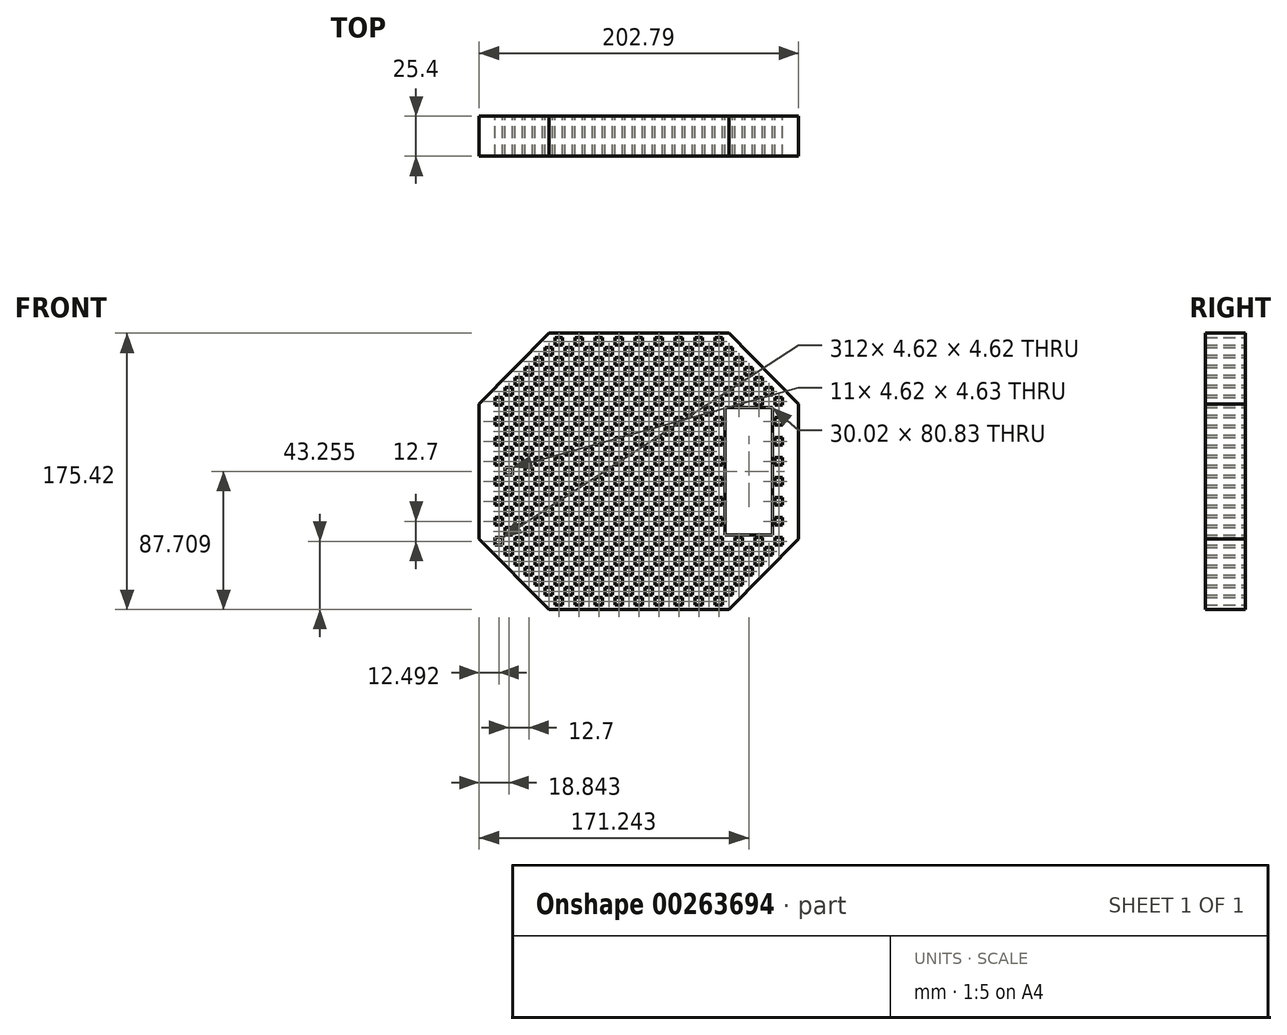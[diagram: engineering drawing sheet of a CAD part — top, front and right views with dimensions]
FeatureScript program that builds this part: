
annotation { "Feature Type Name" : "Feature", "Feature Type Description" : "" }
export const myFeature = defineFeature(function(context is Context, id is Id, definition is map)
    precondition{}
    {
        {
            var Q0;
            Q0=qCreatedBy(makeId("Front.planeOp"),FACE);
            var sketch = newSketch(context, id + "F0", { "sketchPlane" : qUnion([Q0])});
            skPoint(sketch, "E0.orphan", {"position": v(23.5, -32.04) * mm});
            skPoint(sketch, "E1.start.orphan", {"position": v(0, -32.04) * mm});
            skLineSegment(sketch, "E2.2.0.0", {"start": v(51.26, 13.82) * mm, "end": v(51.26, 9.2) * mm});
            skPoint(sketch, "E2.2.0.1", {"position": v(40.87, 11.5) * mm});
            skLineSegment(sketch, "E2.2.0.2", {"start": v(49.53, 2.84) * mm, "end": v(44.91, 2.84) * mm});
            skPoint(sketch, "E2.2.0.3", {"position": v(53.57, 11.5) * mm});
            skLineSegment(sketch, "E2.2.0.4", {"start": v(49.53, 7.47) * mm, "end": v(49.53, 2.84) * mm});
            skPoint(sketch, "E2.2.0.6", {"position": v(40.87, 7.47) * mm});
            skLineSegment(sketch, "E2.2.0.7", {"start": v(38.56, 13.82) * mm, "end": v(38.56, 9.2) * mm});
            skLineSegment(sketch, "E2.2.0.8", {"start": v(47.22, 7.47) * mm, "end": v(49.53, 7.47) * mm});
            skLineSegment(sketch, "E2.2.0.9", {"start": v(55.88, 13.82) * mm, "end": v(55.88, 9.2) * mm});
            skLineSegment(sketch, "E2.2.0.11", {"start": v(43.18, 13.82) * mm, "end": v(38.56, 13.82) * mm});
            skLineSegment(sketch, "E2.2.0.13", {"start": v(43.18, 9.2) * mm, "end": v(38.56, 9.2) * mm});
            skLineSegment(sketch, "E2.2.0.14", {"start": v(51.26, 9.2) * mm, "end": v(55.88, 9.2) * mm});
            skLineSegment(sketch, "E2.2.0.15", {"start": v(43.18, 13.82) * mm, "end": v(43.18, 9.2) * mm});
            skLineSegment(sketch, "E2.2.0.17", {"start": v(44.91, 2.84) * mm, "end": v(44.91, 7.47) * mm});
            skPoint(sketch, "E2.2.0.18", {"position": v(40.87, 15.54) * mm});
            skLineSegment(sketch, "E2.2.0.19", {"start": v(44.91, 7.47) * mm, "end": v(47.22, 7.47) * mm});
            skLineSegment(sketch, "E2.2.0.20", {"start": v(51.26, 13.82) * mm, "end": v(55.88, 13.82) * mm});
            skLineSegment(sketch, "E2.3.0.0", {"start": v(76.66, 13.82) * mm, "end": v(76.66, 9.2) * mm});
            skPoint(sketch, "E2.3.0.1", {"position": v(66.27, 11.5) * mm});
            skLineSegment(sketch, "E2.3.0.2", {"start": v(74.93, 2.84) * mm, "end": v(70.31, 2.84) * mm});
            skPoint(sketch, "E2.3.0.3", {"position": v(78.97, 11.5) * mm});
            skLineSegment(sketch, "E2.3.0.4", {"start": v(74.93, 7.47) * mm, "end": v(74.93, 2.84) * mm});
            skLineSegment(sketch, "E2.3.0.5", {"start": v(59.92, 7.47) * mm, "end": v(62.23, 7.47) * mm});
            skPoint(sketch, "E2.3.0.6", {"position": v(66.27, 7.47) * mm});
            skLineSegment(sketch, "E2.3.0.7", {"start": v(63.96, 13.82) * mm, "end": v(63.96, 9.2) * mm});
            skLineSegment(sketch, "E2.3.0.8", {"start": v(72.62, 7.47) * mm, "end": v(74.93, 7.47) * mm});
            skLineSegment(sketch, "E2.3.0.9", {"start": v(81.28, 13.82) * mm, "end": v(81.28, 9.2) * mm});
            skLineSegment(sketch, "E2.3.0.10", {"start": v(62.23, 2.84) * mm, "end": v(62.23, 7.47) * mm});
            skLineSegment(sketch, "E2.3.0.11", {"start": v(68.58, 13.82) * mm, "end": v(63.96, 13.82) * mm});
            skLineSegment(sketch, "E2.3.0.12", {"start": v(57.61, 2.84) * mm, "end": v(57.61, 7.47) * mm});
            skLineSegment(sketch, "E2.3.0.13", {"start": v(68.58, 9.2) * mm, "end": v(63.96, 9.2) * mm});
            skLineSegment(sketch, "E2.3.0.14", {"start": v(76.66, 9.2) * mm, "end": v(81.28, 9.2) * mm});
            skLineSegment(sketch, "E2.3.0.15", {"start": v(68.58, 13.82) * mm, "end": v(68.58, 9.2) * mm});
            skLineSegment(sketch, "E2.3.0.16", {"start": v(57.61, 2.84) * mm, "end": v(62.23, 2.84) * mm});
            skLineSegment(sketch, "E2.3.0.17", {"start": v(70.31, 2.84) * mm, "end": v(70.31, 7.47) * mm});
            skPoint(sketch, "E2.3.0.18", {"position": v(66.27, 15.54) * mm});
            skLineSegment(sketch, "E2.3.0.19", {"start": v(70.31, 7.47) * mm, "end": v(72.62, 7.47) * mm});
            skLineSegment(sketch, "E2.3.0.20", {"start": v(76.66, 13.82) * mm, "end": v(81.28, 13.82) * mm});
            skLineSegment(sketch, "E2.3.0.21", {"start": v(57.61, 7.47) * mm, "end": v(59.92, 7.47) * mm});
            skPoint(sketch, "E2.4.0.1", {"position": v(91.67, 11.5) * mm});
            skLineSegment(sketch, "E2.4.0.2", {"start": v(100.33, 2.84) * mm, "end": v(95.71, 2.84) * mm});
            skLineSegment(sketch, "E2.4.0.4", {"start": v(100.33, 7.47) * mm, "end": v(100.33, 2.84) * mm});
            skLineSegment(sketch, "E2.4.0.5", {"start": v(85.32, 7.47) * mm, "end": v(87.63, 7.47) * mm});
            skPoint(sketch, "E2.4.0.6", {"position": v(91.67, 7.47) * mm});
            skLineSegment(sketch, "E2.4.0.7", {"start": v(89.36, 13.82) * mm, "end": v(89.36, 9.2) * mm});
            skLineSegment(sketch, "E2.4.0.8", {"start": v(98.02, 7.47) * mm, "end": v(100.33, 7.47) * mm});
            skLineSegment(sketch, "E2.4.0.10", {"start": v(87.63, 2.84) * mm, "end": v(87.63, 7.47) * mm});
            skLineSegment(sketch, "E2.4.0.11", {"start": v(93.98, 13.82) * mm, "end": v(89.36, 13.82) * mm});
            skLineSegment(sketch, "E2.4.0.12", {"start": v(83.01, 2.84) * mm, "end": v(83.01, 7.47) * mm});
            skLineSegment(sketch, "E2.4.0.13", {"start": v(93.98, 9.2) * mm, "end": v(89.36, 9.2) * mm});
            skLineSegment(sketch, "E2.4.0.15", {"start": v(93.98, 13.82) * mm, "end": v(93.98, 9.2) * mm});
            skLineSegment(sketch, "E2.4.0.16", {"start": v(83.01, 2.84) * mm, "end": v(87.63, 2.84) * mm});
            skLineSegment(sketch, "E2.4.0.17", {"start": v(95.71, 2.84) * mm, "end": v(95.71, 7.47) * mm});
            skPoint(sketch, "E2.4.0.18", {"position": v(91.67, 15.54) * mm});
            skLineSegment(sketch, "E2.4.0.19", {"start": v(95.71, 7.47) * mm, "end": v(98.02, 7.47) * mm});
            skLineSegment(sketch, "E2.4.0.21", {"start": v(83.01, 7.47) * mm, "end": v(85.32, 7.47) * mm});
            skPoint(sketch, "E2.9.0.3", {"position": v(231.37, 11.5) * mm});
            skLineSegment(sketch, "E2.direction1", {"start": v(-18.59, 2.84) * mm, "end": v(6.81, 2.84) * mm, "construction": true});
            skPoint(sketch, "E3.0.1.0", {"position": v(40.87, 24.2) * mm});
            skPoint(sketch, "E3.0.1.12", {"position": v(40.87, 20.17) * mm});
            skLineSegment(sketch, "E3.0.1.14", {"start": v(-18.59, 15.54) * mm, "end": v(6.81, 15.54) * mm, "construction": true});
            skLineSegment(sketch, "E3.0.1.15", {"start": v(83.01, 15.54) * mm, "end": v(87.63, 15.54) * mm});
            skLineSegment(sketch, "E3.0.1.17", {"start": v(70.31, 15.54) * mm, "end": v(70.31, 20.17) * mm});
            skLineSegment(sketch, "E3.0.1.18", {"start": v(95.71, 15.54) * mm, "end": v(95.71, 20.17) * mm});
            skLineSegment(sketch, "E3.0.1.19", {"start": v(49.53, 15.54) * mm, "end": v(44.91, 15.54) * mm});
            skLineSegment(sketch, "E3.0.1.21", {"start": v(49.53, 20.17) * mm, "end": v(49.53, 15.54) * mm});
            skPoint(sketch, "E3.0.1.29", {"position": v(40.87, 28.24) * mm});
            skLineSegment(sketch, "E3.0.1.30", {"start": v(74.93, 20.17) * mm, "end": v(74.93, 15.54) * mm});
            skPoint(sketch, "E3.0.1.34", {"position": v(66.27, 24.2) * mm});
            skLineSegment(sketch, "E3.0.1.37", {"start": v(100.33, 15.54) * mm, "end": v(95.71, 15.54) * mm});
            skPoint(sketch, "E3.0.1.41", {"position": v(78.97, 24.2) * mm});
            skLineSegment(sketch, "E3.0.1.43", {"start": v(100.33, 20.17) * mm, "end": v(100.33, 15.54) * mm});
            skPoint(sketch, "E3.0.1.45", {"position": v(66.27, 20.17) * mm});
            skLineSegment(sketch, "E3.0.1.46", {"start": v(36.83, 15.54) * mm, "end": v(36.83, 20.17) * mm});
            skPoint(sketch, "E3.0.1.49", {"position": v(91.67, 24.2) * mm});
            skLineSegment(sketch, "E3.0.1.51", {"start": v(62.23, 15.54) * mm, "end": v(62.23, 20.17) * mm});
            skLineSegment(sketch, "E3.0.1.52", {"start": v(32.21, 15.54) * mm, "end": v(32.21, 20.17) * mm});
            skLineSegment(sketch, "E3.0.1.58", {"start": v(89.36, 26.52) * mm, "end": v(89.36, 21.9) * mm});
            skPoint(sketch, "E3.0.1.65", {"position": v(66.27, 28.24) * mm});
            skPoint(sketch, "E3.0.1.66", {"position": v(91.67, 20.17) * mm});
            skLineSegment(sketch, "E3.0.1.68", {"start": v(87.63, 15.54) * mm, "end": v(87.63, 20.17) * mm});
            skLineSegment(sketch, "E3.0.1.69", {"start": v(57.61, 15.54) * mm, "end": v(57.61, 20.17) * mm});
            skPoint(sketch, "E3.0.1.79", {"position": v(91.67, 28.24) * mm});
            skLineSegment(sketch, "E3.0.1.82", {"start": v(43.18, 26.52) * mm, "end": v(43.18, 21.9) * mm});
            skLineSegment(sketch, "E3.0.1.87", {"start": v(83.01, 15.54) * mm, "end": v(83.01, 20.17) * mm});
            skLineSegment(sketch, "E3.0.1.88", {"start": v(32.21, 15.54) * mm, "end": v(36.83, 15.54) * mm});
            skPoint(sketch, "E3.0.1.92", {"position": v(231.37, 24.2) * mm});
            skLineSegment(sketch, "E3.0.1.93", {"start": v(25.86, 26.52) * mm, "end": v(25.86, 21.9) * mm});
            skLineSegment(sketch, "E3.0.1.94", {"start": v(44.91, 15.54) * mm, "end": v(44.91, 20.17) * mm});
            skLineSegment(sketch, "E3.0.1.95", {"start": v(25.86, 26.52) * mm, "end": v(30.48, 26.52) * mm});
            skLineSegment(sketch, "E3.0.1.99", {"start": v(93.98, 26.52) * mm, "end": v(93.98, 21.9) * mm});
            skLineSegment(sketch, "E3.0.1.105", {"start": v(51.26, 26.52) * mm, "end": v(51.26, 21.9) * mm});
            skLineSegment(sketch, "E3.0.1.106", {"start": v(76.66, 26.52) * mm, "end": v(76.66, 21.9) * mm});
            skLineSegment(sketch, "E3.0.1.109", {"start": v(38.56, 26.52) * mm, "end": v(38.56, 21.9) * mm});
            skLineSegment(sketch, "E3.0.1.110", {"start": v(30.48, 26.52) * mm, "end": v(30.48, 21.9) * mm});
            skLineSegment(sketch, "E3.0.1.115", {"start": v(63.96, 26.52) * mm, "end": v(63.96, 21.9) * mm});
            skLineSegment(sketch, "E3.0.1.116", {"start": v(55.88, 26.52) * mm, "end": v(55.88, 21.9) * mm});
            skLineSegment(sketch, "E3.0.1.122", {"start": v(25.86, 21.9) * mm, "end": v(30.48, 21.9) * mm});
            skLineSegment(sketch, "E3.0.1.123", {"start": v(81.28, 26.52) * mm, "end": v(81.28, 21.9) * mm});
            skLineSegment(sketch, "E3.0.1.124", {"start": v(43.18, 26.52) * mm, "end": v(38.56, 26.52) * mm});
            skLineSegment(sketch, "E3.0.1.127", {"start": v(43.18, 21.9) * mm, "end": v(38.56, 21.9) * mm});
            skLineSegment(sketch, "E3.0.1.139", {"start": v(93.98, 26.52) * mm, "end": v(89.36, 26.52) * mm});
            skLineSegment(sketch, "E3.0.1.141", {"start": v(93.98, 21.9) * mm, "end": v(89.36, 21.9) * mm});
            skLineSegment(sketch, "E3.0.1.142", {"start": v(68.58, 26.52) * mm, "end": v(68.58, 21.9) * mm});
            skLineSegment(sketch, "E3.0.1.146", {"start": v(57.61, 15.54) * mm, "end": v(62.23, 15.54) * mm});
            skLineSegment(sketch, "E3.0.1.151", {"start": v(51.26, 26.52) * mm, "end": v(55.88, 26.52) * mm});
            skLineSegment(sketch, "E3.0.1.152", {"start": v(76.66, 26.52) * mm, "end": v(81.28, 26.52) * mm});
            skLineSegment(sketch, "E3.0.1.153", {"start": v(32.21, 20.17) * mm, "end": v(34.52, 20.17) * mm});
            skLineSegment(sketch, "E3.0.1.154", {"start": v(70.31, 20.17) * mm, "end": v(72.62, 20.17) * mm});
            skLineSegment(sketch, "E3.0.1.156", {"start": v(44.91, 20.17) * mm, "end": v(47.22, 20.17) * mm});
            skLineSegment(sketch, "E3.0.1.162", {"start": v(74.93, 15.54) * mm, "end": v(70.31, 15.54) * mm});
            skLineSegment(sketch, "E3.0.1.163", {"start": v(34.52, 20.17) * mm, "end": v(36.83, 20.17) * mm});
            skLineSegment(sketch, "E3.0.1.166", {"start": v(95.71, 20.17) * mm, "end": v(98.02, 20.17) * mm});
            skLineSegment(sketch, "E3.0.1.167", {"start": v(57.61, 20.17) * mm, "end": v(59.92, 20.17) * mm});
            skLineSegment(sketch, "E3.0.1.170", {"start": v(59.92, 20.17) * mm, "end": v(62.23, 20.17) * mm});
            skLineSegment(sketch, "E3.0.1.171", {"start": v(47.22, 20.17) * mm, "end": v(49.53, 20.17) * mm});
            skLineSegment(sketch, "E3.0.1.173", {"start": v(83.01, 20.17) * mm, "end": v(85.32, 20.17) * mm});
            skLineSegment(sketch, "E3.0.1.178", {"start": v(72.62, 20.17) * mm, "end": v(74.93, 20.17) * mm});
            skLineSegment(sketch, "E3.0.1.182", {"start": v(85.32, 20.17) * mm, "end": v(87.63, 20.17) * mm});
            skLineSegment(sketch, "E3.0.1.184", {"start": v(98.02, 20.17) * mm, "end": v(100.33, 20.17) * mm});
            skLineSegment(sketch, "E3.0.1.192", {"start": v(68.58, 26.52) * mm, "end": v(63.96, 26.52) * mm});
            skLineSegment(sketch, "E3.0.1.194", {"start": v(51.26, 21.9) * mm, "end": v(55.88, 21.9) * mm});
            skLineSegment(sketch, "E3.0.1.208", {"start": v(68.58, 21.9) * mm, "end": v(63.96, 21.9) * mm});
            skLineSegment(sketch, "E3.0.1.211", {"start": v(76.66, 21.9) * mm, "end": v(81.28, 21.9) * mm});
            skPoint(sketch, "E3.0.2.0", {"position": v(40.87, 36.9) * mm});
            skPoint(sketch, "E3.0.2.7", {"position": v(53.57, 36.9) * mm});
            skLineSegment(sketch, "E3.0.2.8", {"start": v(24.13, 32.87) * mm, "end": v(24.13, 28.24) * mm});
            skPoint(sketch, "E3.0.2.11", {"position": v(15.47, 40.94) * mm});
            skPoint(sketch, "E3.0.2.12", {"position": v(40.87, 32.87) * mm});
            skLineSegment(sketch, "E3.0.2.14", {"start": v(-18.59, 28.24) * mm, "end": v(6.81, 28.24) * mm, "construction": true});
            skLineSegment(sketch, "E3.0.2.15", {"start": v(83.01, 28.24) * mm, "end": v(87.63, 28.24) * mm});
            skLineSegment(sketch, "E3.0.2.17", {"start": v(70.31, 28.24) * mm, "end": v(70.31, 32.87) * mm});
            skLineSegment(sketch, "E3.0.2.18", {"start": v(95.71, 28.24) * mm, "end": v(95.71, 32.87) * mm});
            skLineSegment(sketch, "E3.0.2.19", {"start": v(49.53, 28.24) * mm, "end": v(44.91, 28.24) * mm});
            skLineSegment(sketch, "E3.0.2.21", {"start": v(49.53, 32.87) * mm, "end": v(49.53, 28.24) * mm});
            skPoint(sketch, "E3.0.2.29", {"position": v(40.87, 40.94) * mm});
            skLineSegment(sketch, "E3.0.2.30", {"start": v(74.93, 32.87) * mm, "end": v(74.93, 28.24) * mm});
            skLineSegment(sketch, "E3.0.2.37", {"start": v(100.33, 28.24) * mm, "end": v(95.71, 28.24) * mm});
            skPoint(sketch, "E3.0.2.41", {"position": v(78.97, 36.9) * mm});
            skLineSegment(sketch, "E3.0.2.43", {"start": v(100.33, 32.87) * mm, "end": v(100.33, 28.24) * mm});
            skPoint(sketch, "E3.0.2.45", {"position": v(66.27, 32.87) * mm});
            skLineSegment(sketch, "E3.0.2.46", {"start": v(36.83, 28.24) * mm, "end": v(36.83, 32.87) * mm});
            skPoint(sketch, "E3.0.2.49", {"position": v(91.67, 36.9) * mm});
            skLineSegment(sketch, "E3.0.2.51", {"start": v(62.23, 28.24) * mm, "end": v(62.23, 32.87) * mm});
            skLineSegment(sketch, "E3.0.2.52", {"start": v(32.21, 28.24) * mm, "end": v(32.21, 32.87) * mm});
            skLineSegment(sketch, "E3.0.2.58", {"start": v(89.36, 39.22) * mm, "end": v(89.36, 34.6) * mm});
            skPoint(sketch, "E3.0.2.65", {"position": v(66.27, 40.94) * mm});
            skPoint(sketch, "E3.0.2.66", {"position": v(91.67, 32.87) * mm});
            skLineSegment(sketch, "E3.0.2.68", {"start": v(87.63, 28.24) * mm, "end": v(87.63, 32.87) * mm});
            skLineSegment(sketch, "E3.0.2.69", {"start": v(57.61, 28.24) * mm, "end": v(57.61, 32.87) * mm});
            skPoint(sketch, "E3.0.2.79", {"position": v(91.67, 40.94) * mm});
            skLineSegment(sketch, "E3.0.2.82", {"start": v(43.18, 39.22) * mm, "end": v(43.18, 34.6) * mm});
            skLineSegment(sketch, "E3.0.2.83", {"start": v(19.51, 28.24) * mm, "end": v(19.51, 32.87) * mm});
            skPoint(sketch, "E3.0.2.85", {"position": v(15.47, 36.9) * mm});
            skLineSegment(sketch, "E3.0.2.87", {"start": v(83.01, 28.24) * mm, "end": v(83.01, 32.87) * mm});
            skLineSegment(sketch, "E3.0.2.88", {"start": v(32.21, 28.24) * mm, "end": v(36.83, 28.24) * mm});
            skPoint(sketch, "E3.0.2.92", {"position": v(231.37, 36.9) * mm});
            skLineSegment(sketch, "E3.0.2.93", {"start": v(25.86, 39.22) * mm, "end": v(25.86, 34.6) * mm});
            skLineSegment(sketch, "E3.0.2.94", {"start": v(44.91, 28.24) * mm, "end": v(44.91, 32.87) * mm});
            skLineSegment(sketch, "E3.0.2.95", {"start": v(25.86, 39.22) * mm, "end": v(30.48, 39.22) * mm});
            skLineSegment(sketch, "E3.0.2.99", {"start": v(93.98, 39.22) * mm, "end": v(93.98, 34.6) * mm});
            skLineSegment(sketch, "E3.0.2.104", {"start": v(13.16, 39.22) * mm, "end": v(13.16, 34.6) * mm});
            skLineSegment(sketch, "E3.0.2.105", {"start": v(51.26, 39.22) * mm, "end": v(51.26, 34.6) * mm});
            skLineSegment(sketch, "E3.0.2.106", {"start": v(76.66, 39.22) * mm, "end": v(76.66, 34.6) * mm});
            skLineSegment(sketch, "E3.0.2.109", {"start": v(38.56, 39.22) * mm, "end": v(38.56, 34.6) * mm});
            skLineSegment(sketch, "E3.0.2.110", {"start": v(30.48, 39.22) * mm, "end": v(30.48, 34.6) * mm});
            skLineSegment(sketch, "E3.0.2.115", {"start": v(63.96, 39.22) * mm, "end": v(63.96, 34.6) * mm});
            skLineSegment(sketch, "E3.0.2.116", {"start": v(55.88, 39.22) * mm, "end": v(55.88, 34.6) * mm});
            skLineSegment(sketch, "E3.0.2.122", {"start": v(25.86, 34.6) * mm, "end": v(30.48, 34.6) * mm});
            skLineSegment(sketch, "E3.0.2.123", {"start": v(81.28, 39.22) * mm, "end": v(81.28, 34.6) * mm});
            skLineSegment(sketch, "E3.0.2.124", {"start": v(43.18, 39.22) * mm, "end": v(38.56, 39.22) * mm});
            skLineSegment(sketch, "E3.0.2.127", {"start": v(43.18, 34.6) * mm, "end": v(38.56, 34.6) * mm});
            skLineSegment(sketch, "E3.0.2.128", {"start": v(17.78, 39.22) * mm, "end": v(17.78, 34.6) * mm});
            skLineSegment(sketch, "E3.0.2.139", {"start": v(93.98, 39.22) * mm, "end": v(89.36, 39.22) * mm});
            skLineSegment(sketch, "E3.0.2.141", {"start": v(93.98, 34.6) * mm, "end": v(89.36, 34.6) * mm});
            skLineSegment(sketch, "E3.0.2.142", {"start": v(68.58, 39.22) * mm, "end": v(68.58, 34.6) * mm});
            skLineSegment(sketch, "E3.0.2.145", {"start": v(24.13, 28.24) * mm, "end": v(19.51, 28.24) * mm});
            skLineSegment(sketch, "E3.0.2.146", {"start": v(57.61, 28.24) * mm, "end": v(62.23, 28.24) * mm});
            skLineSegment(sketch, "E3.0.2.151", {"start": v(51.26, 39.22) * mm, "end": v(55.88, 39.22) * mm});
            skLineSegment(sketch, "E3.0.2.152", {"start": v(76.66, 39.22) * mm, "end": v(81.28, 39.22) * mm});
            skLineSegment(sketch, "E3.0.2.153", {"start": v(32.21, 32.87) * mm, "end": v(34.52, 32.87) * mm});
            skLineSegment(sketch, "E3.0.2.154", {"start": v(70.31, 32.87) * mm, "end": v(72.62, 32.87) * mm});
            skLineSegment(sketch, "E3.0.2.156", {"start": v(44.91, 32.87) * mm, "end": v(47.22, 32.87) * mm});
            skLineSegment(sketch, "E3.0.2.162", {"start": v(74.93, 28.24) * mm, "end": v(70.31, 28.24) * mm});
            skLineSegment(sketch, "E3.0.2.163", {"start": v(34.52, 32.87) * mm, "end": v(36.83, 32.87) * mm});
            skLineSegment(sketch, "E3.0.2.164", {"start": v(21.82, 32.87) * mm, "end": v(24.13, 32.87) * mm});
            skLineSegment(sketch, "E3.0.2.166", {"start": v(95.71, 32.87) * mm, "end": v(98.02, 32.87) * mm});
            skLineSegment(sketch, "E3.0.2.167", {"start": v(57.61, 32.87) * mm, "end": v(59.92, 32.87) * mm});
            skLineSegment(sketch, "E3.0.2.170", {"start": v(59.92, 32.87) * mm, "end": v(62.23, 32.87) * mm});
            skLineSegment(sketch, "E3.0.2.171", {"start": v(47.22, 32.87) * mm, "end": v(49.53, 32.87) * mm});
            skLineSegment(sketch, "E3.0.2.173", {"start": v(83.01, 32.87) * mm, "end": v(85.32, 32.87) * mm});
            skLineSegment(sketch, "E3.0.2.175", {"start": v(17.78, 39.22) * mm, "end": v(13.16, 39.22) * mm});
            skLineSegment(sketch, "E3.0.2.178", {"start": v(72.62, 32.87) * mm, "end": v(74.93, 32.87) * mm});
            skLineSegment(sketch, "E3.0.2.182", {"start": v(85.32, 32.87) * mm, "end": v(87.63, 32.87) * mm});
            skLineSegment(sketch, "E3.0.2.184", {"start": v(98.02, 32.87) * mm, "end": v(100.33, 32.87) * mm});
            skLineSegment(sketch, "E3.0.2.190", {"start": v(17.78, 34.6) * mm, "end": v(13.16, 34.6) * mm});
            skLineSegment(sketch, "E3.0.2.192", {"start": v(68.58, 39.22) * mm, "end": v(63.96, 39.22) * mm});
            skLineSegment(sketch, "E3.0.2.194", {"start": v(51.26, 34.6) * mm, "end": v(55.88, 34.6) * mm});
            skLineSegment(sketch, "E3.0.2.208", {"start": v(68.58, 34.6) * mm, "end": v(63.96, 34.6) * mm});
            skLineSegment(sketch, "E3.0.2.211", {"start": v(76.66, 34.6) * mm, "end": v(81.28, 34.6) * mm});
            skLineSegment(sketch, "E3.0.2.212", {"start": v(19.51, 32.87) * mm, "end": v(21.82, 32.87) * mm});
            skPoint(sketch, "E3.0.3.0", {"position": v(40.87, 49.6) * mm});
            skPoint(sketch, "E3.0.3.5", {"position": v(15.47, 45.57) * mm});
            skPoint(sketch, "E3.0.3.7", {"position": v(53.57, 49.6) * mm});
            skLineSegment(sketch, "E3.0.3.8", {"start": v(24.13, 45.57) * mm, "end": v(24.13, 40.94) * mm});
            skPoint(sketch, "E3.0.3.11", {"position": v(15.47, 53.64) * mm});
            skPoint(sketch, "E3.0.3.12", {"position": v(40.87, 45.57) * mm});
            skLineSegment(sketch, "E3.0.3.14", {"start": v(-18.59, 40.94) * mm, "end": v(6.81, 40.94) * mm, "construction": true});
            skLineSegment(sketch, "E3.0.3.15", {"start": v(83.01, 40.94) * mm, "end": v(87.63, 40.94) * mm});
            skLineSegment(sketch, "E3.0.3.17", {"start": v(70.31, 40.94) * mm, "end": v(70.31, 45.57) * mm});
            skLineSegment(sketch, "E3.0.3.18", {"start": v(95.71, 40.94) * mm, "end": v(95.71, 45.57) * mm});
            skLineSegment(sketch, "E3.0.3.19", {"start": v(49.53, 40.94) * mm, "end": v(44.91, 40.94) * mm});
            skLineSegment(sketch, "E3.0.3.21", {"start": v(49.53, 45.57) * mm, "end": v(49.53, 40.94) * mm});
            skPoint(sketch, "E3.0.3.29", {"position": v(40.87, 53.64) * mm});
            skLineSegment(sketch, "E3.0.3.30", {"start": v(74.93, 45.57) * mm, "end": v(74.93, 40.94) * mm});
            skPoint(sketch, "E3.0.3.34", {"position": v(66.27, 49.6) * mm});
            skLineSegment(sketch, "E3.0.3.35", {"start": v(11.43, 40.94) * mm, "end": v(11.43, 45.57) * mm});
            skLineSegment(sketch, "E3.0.3.37", {"start": v(100.33, 40.94) * mm, "end": v(95.71, 40.94) * mm});
            skLineSegment(sketch, "E3.0.3.43", {"start": v(100.33, 45.57) * mm, "end": v(100.33, 40.94) * mm});
            skPoint(sketch, "E3.0.3.45", {"position": v(66.27, 45.57) * mm});
            skLineSegment(sketch, "E3.0.3.46", {"start": v(36.83, 40.94) * mm, "end": v(36.83, 45.57) * mm});
            skLineSegment(sketch, "E3.0.3.47", {"start": v(6.81, 40.94) * mm, "end": v(6.81, 45.57) * mm});
            skPoint(sketch, "E3.0.3.49", {"position": v(91.67, 49.6) * mm});
            skLineSegment(sketch, "E3.0.3.51", {"start": v(62.23, 40.94) * mm, "end": v(62.23, 45.57) * mm});
            skLineSegment(sketch, "E3.0.3.52", {"start": v(32.21, 40.94) * mm, "end": v(32.21, 45.57) * mm});
            skLineSegment(sketch, "E3.0.3.58", {"start": v(89.36, 51.92) * mm, "end": v(89.36, 47.3) * mm});
            skPoint(sketch, "E3.0.3.65", {"position": v(66.27, 53.64) * mm});
            skPoint(sketch, "E3.0.3.66", {"position": v(91.67, 45.57) * mm});
            skLineSegment(sketch, "E3.0.3.68", {"start": v(87.63, 40.94) * mm, "end": v(87.63, 45.57) * mm});
            skLineSegment(sketch, "E3.0.3.69", {"start": v(57.61, 40.94) * mm, "end": v(57.61, 45.57) * mm});
            skPoint(sketch, "E3.0.3.79", {"position": v(91.67, 53.64) * mm});
            skLineSegment(sketch, "E3.0.3.82", {"start": v(43.18, 51.92) * mm, "end": v(43.18, 47.3) * mm});
            skLineSegment(sketch, "E3.0.3.83", {"start": v(19.51, 40.94) * mm, "end": v(19.51, 45.57) * mm});
            skPoint(sketch, "E3.0.3.85", {"position": v(15.47, 49.6) * mm});
            skLineSegment(sketch, "E3.0.3.87", {"start": v(83.01, 40.94) * mm, "end": v(83.01, 45.57) * mm});
            skLineSegment(sketch, "E3.0.3.88", {"start": v(32.21, 40.94) * mm, "end": v(36.83, 40.94) * mm});
            skPoint(sketch, "E3.0.3.92", {"position": v(231.37, 49.6) * mm});
            skLineSegment(sketch, "E3.0.3.93", {"start": v(25.86, 51.92) * mm, "end": v(25.86, 47.3) * mm});
            skLineSegment(sketch, "E3.0.3.94", {"start": v(44.91, 40.94) * mm, "end": v(44.91, 45.57) * mm});
            skLineSegment(sketch, "E3.0.3.95", {"start": v(25.86, 51.92) * mm, "end": v(30.48, 51.92) * mm});
            skLineSegment(sketch, "E3.0.3.99", {"start": v(93.98, 51.92) * mm, "end": v(93.98, 47.3) * mm});
            skLineSegment(sketch, "E3.0.3.104", {"start": v(13.16, 51.92) * mm, "end": v(13.16, 47.3) * mm});
            skLineSegment(sketch, "E3.0.3.105", {"start": v(51.26, 51.92) * mm, "end": v(51.26, 47.3) * mm});
            skLineSegment(sketch, "E3.0.3.106", {"start": v(76.66, 51.92) * mm, "end": v(76.66, 47.3) * mm});
            skLineSegment(sketch, "E3.0.3.109", {"start": v(38.56, 51.92) * mm, "end": v(38.56, 47.3) * mm});
            skLineSegment(sketch, "E3.0.3.110", {"start": v(30.48, 51.92) * mm, "end": v(30.48, 47.3) * mm});
            skLineSegment(sketch, "E3.0.3.115", {"start": v(63.96, 51.92) * mm, "end": v(63.96, 47.3) * mm});
            skLineSegment(sketch, "E3.0.3.116", {"start": v(55.88, 51.92) * mm, "end": v(55.88, 47.3) * mm});
            skLineSegment(sketch, "E3.0.3.122", {"start": v(25.86, 47.3) * mm, "end": v(30.48, 47.3) * mm});
            skLineSegment(sketch, "E3.0.3.123", {"start": v(81.28, 51.92) * mm, "end": v(81.28, 47.3) * mm});
            skLineSegment(sketch, "E3.0.3.124", {"start": v(43.18, 51.92) * mm, "end": v(38.56, 51.92) * mm});
            skLineSegment(sketch, "E3.0.3.127", {"start": v(43.18, 47.3) * mm, "end": v(38.56, 47.3) * mm});
            skLineSegment(sketch, "E3.0.3.128", {"start": v(17.78, 51.92) * mm, "end": v(17.78, 47.3) * mm});
            skLineSegment(sketch, "E3.0.3.139", {"start": v(93.98, 51.92) * mm, "end": v(89.36, 51.92) * mm});
            skLineSegment(sketch, "E3.0.3.141", {"start": v(93.98, 47.3) * mm, "end": v(89.36, 47.3) * mm});
            skLineSegment(sketch, "E3.0.3.142", {"start": v(68.58, 51.92) * mm, "end": v(68.58, 47.3) * mm});
            skLineSegment(sketch, "E3.0.3.145", {"start": v(24.13, 40.94) * mm, "end": v(19.51, 40.94) * mm});
            skLineSegment(sketch, "E3.0.3.146", {"start": v(57.61, 40.94) * mm, "end": v(62.23, 40.94) * mm});
            skLineSegment(sketch, "E3.0.3.147", {"start": v(9.12, 45.57) * mm, "end": v(11.43, 45.57) * mm});
            skLineSegment(sketch, "E3.0.3.149", {"start": v(6.81, 45.57) * mm, "end": v(9.12, 45.57) * mm});
            skLineSegment(sketch, "E3.0.3.151", {"start": v(51.26, 51.92) * mm, "end": v(55.88, 51.92) * mm});
            skLineSegment(sketch, "E3.0.3.152", {"start": v(76.66, 51.92) * mm, "end": v(81.28, 51.92) * mm});
            skLineSegment(sketch, "E3.0.3.153", {"start": v(32.21, 45.57) * mm, "end": v(34.52, 45.57) * mm});
            skLineSegment(sketch, "E3.0.3.154", {"start": v(70.31, 45.57) * mm, "end": v(72.62, 45.57) * mm});
            skLineSegment(sketch, "E3.0.3.156", {"start": v(44.91, 45.57) * mm, "end": v(47.22, 45.57) * mm});
            skLineSegment(sketch, "E3.0.3.162", {"start": v(74.93, 40.94) * mm, "end": v(70.31, 40.94) * mm});
            skLineSegment(sketch, "E3.0.3.163", {"start": v(34.52, 45.57) * mm, "end": v(36.83, 45.57) * mm});
            skLineSegment(sketch, "E3.0.3.164", {"start": v(21.82, 45.57) * mm, "end": v(24.13, 45.57) * mm});
            skLineSegment(sketch, "E3.0.3.166", {"start": v(95.71, 45.57) * mm, "end": v(98.02, 45.57) * mm});
            skLineSegment(sketch, "E3.0.3.167", {"start": v(57.61, 45.57) * mm, "end": v(59.92, 45.57) * mm});
            skLineSegment(sketch, "E3.0.3.170", {"start": v(59.92, 45.57) * mm, "end": v(62.23, 45.57) * mm});
            skLineSegment(sketch, "E3.0.3.171", {"start": v(47.22, 45.57) * mm, "end": v(49.53, 45.57) * mm});
            skLineSegment(sketch, "E3.0.3.173", {"start": v(83.01, 45.57) * mm, "end": v(85.32, 45.57) * mm});
            skLineSegment(sketch, "E3.0.3.175", {"start": v(17.78, 51.92) * mm, "end": v(13.16, 51.92) * mm});
            skLineSegment(sketch, "E3.0.3.178", {"start": v(72.62, 45.57) * mm, "end": v(74.93, 45.57) * mm});
            skLineSegment(sketch, "E3.0.3.182", {"start": v(85.32, 45.57) * mm, "end": v(87.63, 45.57) * mm});
            skLineSegment(sketch, "E3.0.3.184", {"start": v(98.02, 45.57) * mm, "end": v(100.33, 45.57) * mm});
            skLineSegment(sketch, "E3.0.3.190", {"start": v(17.78, 47.3) * mm, "end": v(13.16, 47.3) * mm});
            skLineSegment(sketch, "E3.0.3.192", {"start": v(68.58, 51.92) * mm, "end": v(63.96, 51.92) * mm});
            skLineSegment(sketch, "E3.0.3.194", {"start": v(51.26, 47.3) * mm, "end": v(55.88, 47.3) * mm});
            skLineSegment(sketch, "E3.0.3.195", {"start": v(6.81, 40.94) * mm, "end": v(11.43, 40.94) * mm});
            skLineSegment(sketch, "E3.0.3.208", {"start": v(68.58, 47.3) * mm, "end": v(63.96, 47.3) * mm});
            skLineSegment(sketch, "E3.0.3.211", {"start": v(76.66, 47.3) * mm, "end": v(81.28, 47.3) * mm});
            skLineSegment(sketch, "E3.0.3.212", {"start": v(19.51, 45.57) * mm, "end": v(21.82, 45.57) * mm});
            skPoint(sketch, "E3.0.4.0", {"position": v(40.87, 62.3) * mm});
            skPoint(sketch, "E3.0.4.5", {"position": v(15.47, 58.27) * mm});
            skPoint(sketch, "E3.0.4.7", {"position": v(53.57, 62.3) * mm});
            skLineSegment(sketch, "E3.0.4.8", {"start": v(24.13, 58.27) * mm, "end": v(24.13, 53.64) * mm});
            skLineSegment(sketch, "E3.0.4.14", {"start": v(-18.59, 53.64) * mm, "end": v(6.81, 53.64) * mm, "construction": true});
            skLineSegment(sketch, "E3.0.4.15", {"start": v(83.01, 53.64) * mm, "end": v(87.63, 53.64) * mm});
            skLineSegment(sketch, "E3.0.4.17", {"start": v(70.31, 53.64) * mm, "end": v(70.31, 58.27) * mm});
            skLineSegment(sketch, "E3.0.4.18", {"start": v(95.71, 53.64) * mm, "end": v(95.71, 58.27) * mm});
            skLineSegment(sketch, "E3.0.4.19", {"start": v(49.53, 53.64) * mm, "end": v(44.91, 53.64) * mm});
            skLineSegment(sketch, "E3.0.4.21", {"start": v(49.53, 58.27) * mm, "end": v(49.53, 53.64) * mm});
            skLineSegment(sketch, "E3.0.4.30", {"start": v(74.93, 58.27) * mm, "end": v(74.93, 53.64) * mm});
            skLineSegment(sketch, "E3.0.4.35", {"start": v(11.43, 53.64) * mm, "end": v(11.43, 58.27) * mm});
            skLineSegment(sketch, "E3.0.4.37", {"start": v(100.33, 53.64) * mm, "end": v(95.71, 53.64) * mm});
            skPoint(sketch, "E3.0.4.41", {"position": v(78.97, 62.3) * mm});
            skLineSegment(sketch, "E3.0.4.43", {"start": v(100.33, 58.27) * mm, "end": v(100.33, 53.64) * mm});
            skPoint(sketch, "E3.0.4.45", {"position": v(66.27, 58.27) * mm});
            skLineSegment(sketch, "E3.0.4.46", {"start": v(36.83, 53.64) * mm, "end": v(36.83, 58.27) * mm});
            skLineSegment(sketch, "E3.0.4.47", {"start": v(6.81, 53.64) * mm, "end": v(6.81, 58.27) * mm});
            skPoint(sketch, "E3.0.4.49", {"position": v(91.67, 62.3) * mm});
            skLineSegment(sketch, "E3.0.4.51", {"start": v(62.23, 53.64) * mm, "end": v(62.23, 58.27) * mm});
            skLineSegment(sketch, "E3.0.4.52", {"start": v(32.21, 53.64) * mm, "end": v(32.21, 58.27) * mm});
            skLineSegment(sketch, "E3.0.4.58", {"start": v(89.36, 64.62) * mm, "end": v(89.36, 60) * mm});
            skPoint(sketch, "E3.0.4.65", {"position": v(66.27, 66.34) * mm});
            skPoint(sketch, "E3.0.4.66", {"position": v(91.67, 58.27) * mm});
            skLineSegment(sketch, "E3.0.4.68", {"start": v(87.63, 53.64) * mm, "end": v(87.63, 58.27) * mm});
            skLineSegment(sketch, "E3.0.4.69", {"start": v(57.61, 53.64) * mm, "end": v(57.61, 58.27) * mm});
            skPoint(sketch, "E3.0.4.79", {"position": v(91.67, 66.34) * mm});
            skLineSegment(sketch, "E3.0.4.82", {"start": v(43.18, 64.62) * mm, "end": v(43.18, 60) * mm});
            skLineSegment(sketch, "E3.0.4.83", {"start": v(19.51, 53.64) * mm, "end": v(19.51, 58.27) * mm});
            skPoint(sketch, "E3.0.4.85", {"position": v(15.47, 62.3) * mm});
            skLineSegment(sketch, "E3.0.4.87", {"start": v(83.01, 53.64) * mm, "end": v(83.01, 58.27) * mm});
            skLineSegment(sketch, "E3.0.4.88", {"start": v(32.21, 53.64) * mm, "end": v(36.83, 53.64) * mm});
            skPoint(sketch, "E3.0.4.92", {"position": v(231.37, 62.3) * mm});
            skLineSegment(sketch, "E3.0.4.93", {"start": v(25.86, 64.62) * mm, "end": v(25.86, 60) * mm});
            skLineSegment(sketch, "E3.0.4.94", {"start": v(44.91, 53.64) * mm, "end": v(44.91, 58.27) * mm});
            skLineSegment(sketch, "E3.0.4.95", {"start": v(25.86, 64.62) * mm, "end": v(30.48, 64.62) * mm});
            skLineSegment(sketch, "E3.0.4.99", {"start": v(93.98, 64.62) * mm, "end": v(93.98, 60) * mm});
            skLineSegment(sketch, "E3.0.4.104", {"start": v(13.16, 64.62) * mm, "end": v(13.16, 60) * mm});
            skLineSegment(sketch, "E3.0.4.105", {"start": v(51.26, 64.62) * mm, "end": v(51.26, 60) * mm});
            skLineSegment(sketch, "E3.0.4.106", {"start": v(76.66, 64.62) * mm, "end": v(76.66, 60) * mm});
            skLineSegment(sketch, "E3.0.4.109", {"start": v(38.56, 64.62) * mm, "end": v(38.56, 60) * mm});
            skLineSegment(sketch, "E3.0.4.110", {"start": v(30.48, 64.62) * mm, "end": v(30.48, 60) * mm});
            skLineSegment(sketch, "E3.0.4.115", {"start": v(63.96, 64.62) * mm, "end": v(63.96, 60) * mm});
            skLineSegment(sketch, "E3.0.4.116", {"start": v(55.88, 64.62) * mm, "end": v(55.88, 60) * mm});
            skLineSegment(sketch, "E3.0.4.122", {"start": v(25.86, 60) * mm, "end": v(30.48, 60) * mm});
            skLineSegment(sketch, "E3.0.4.123", {"start": v(81.28, 64.62) * mm, "end": v(81.28, 60) * mm});
            skLineSegment(sketch, "E3.0.4.124", {"start": v(43.18, 64.62) * mm, "end": v(38.56, 64.62) * mm});
            skLineSegment(sketch, "E3.0.4.127", {"start": v(43.18, 60) * mm, "end": v(38.56, 60) * mm});
            skLineSegment(sketch, "E3.0.4.128", {"start": v(17.78, 64.62) * mm, "end": v(17.78, 60) * mm});
            skLineSegment(sketch, "E3.0.4.139", {"start": v(93.98, 64.62) * mm, "end": v(89.36, 64.62) * mm});
            skLineSegment(sketch, "E3.0.4.141", {"start": v(93.98, 60) * mm, "end": v(89.36, 60) * mm});
            skLineSegment(sketch, "E3.0.4.142", {"start": v(68.58, 64.62) * mm, "end": v(68.58, 60) * mm});
            skLineSegment(sketch, "E3.0.4.145", {"start": v(24.13, 53.64) * mm, "end": v(19.51, 53.64) * mm});
            skLineSegment(sketch, "E3.0.4.146", {"start": v(57.61, 53.64) * mm, "end": v(62.23, 53.64) * mm});
            skLineSegment(sketch, "E3.0.4.147", {"start": v(9.12, 58.27) * mm, "end": v(11.43, 58.27) * mm});
            skLineSegment(sketch, "E3.0.4.149", {"start": v(6.81, 58.27) * mm, "end": v(9.12, 58.27) * mm});
            skLineSegment(sketch, "E3.0.4.151", {"start": v(51.26, 64.62) * mm, "end": v(55.88, 64.62) * mm});
            skLineSegment(sketch, "E3.0.4.152", {"start": v(76.66, 64.62) * mm, "end": v(81.28, 64.62) * mm});
            skLineSegment(sketch, "E3.0.4.153", {"start": v(32.21, 58.27) * mm, "end": v(34.52, 58.27) * mm});
            skLineSegment(sketch, "E3.0.4.154", {"start": v(70.31, 58.27) * mm, "end": v(72.62, 58.27) * mm});
            skLineSegment(sketch, "E3.0.4.156", {"start": v(44.91, 58.27) * mm, "end": v(47.22, 58.27) * mm});
            skLineSegment(sketch, "E3.0.4.162", {"start": v(74.93, 53.64) * mm, "end": v(70.31, 53.64) * mm});
            skLineSegment(sketch, "E3.0.4.163", {"start": v(34.52, 58.27) * mm, "end": v(36.83, 58.27) * mm});
            skLineSegment(sketch, "E3.0.4.164", {"start": v(21.82, 58.27) * mm, "end": v(24.13, 58.27) * mm});
            skLineSegment(sketch, "E3.0.4.166", {"start": v(95.71, 58.27) * mm, "end": v(98.02, 58.27) * mm});
            skLineSegment(sketch, "E3.0.4.167", {"start": v(57.61, 58.27) * mm, "end": v(59.92, 58.27) * mm});
            skLineSegment(sketch, "E3.0.4.170", {"start": v(59.92, 58.27) * mm, "end": v(62.23, 58.27) * mm});
            skLineSegment(sketch, "E3.0.4.171", {"start": v(47.22, 58.27) * mm, "end": v(49.53, 58.27) * mm});
            skLineSegment(sketch, "E3.0.4.173", {"start": v(83.01, 58.27) * mm, "end": v(85.32, 58.27) * mm});
            skLineSegment(sketch, "E3.0.4.175", {"start": v(17.78, 64.62) * mm, "end": v(13.16, 64.62) * mm});
            skLineSegment(sketch, "E3.0.4.178", {"start": v(72.62, 58.27) * mm, "end": v(74.93, 58.27) * mm});
            skLineSegment(sketch, "E3.0.4.182", {"start": v(85.32, 58.27) * mm, "end": v(87.63, 58.27) * mm});
            skLineSegment(sketch, "E3.0.4.184", {"start": v(98.02, 58.27) * mm, "end": v(100.33, 58.27) * mm});
            skLineSegment(sketch, "E3.0.4.190", {"start": v(17.78, 60) * mm, "end": v(13.16, 60) * mm});
            skLineSegment(sketch, "E3.0.4.192", {"start": v(68.58, 64.62) * mm, "end": v(63.96, 64.62) * mm});
            skLineSegment(sketch, "E3.0.4.194", {"start": v(51.26, 60) * mm, "end": v(55.88, 60) * mm});
            skLineSegment(sketch, "E3.0.4.195", {"start": v(6.81, 53.64) * mm, "end": v(11.43, 53.64) * mm});
            skLineSegment(sketch, "E3.0.4.208", {"start": v(68.58, 60) * mm, "end": v(63.96, 60) * mm});
            skLineSegment(sketch, "E3.0.4.211", {"start": v(76.66, 60) * mm, "end": v(81.28, 60) * mm});
            skLineSegment(sketch, "E3.0.4.212", {"start": v(19.51, 58.27) * mm, "end": v(21.82, 58.27) * mm});
            skPoint(sketch, "E3.0.5.0", {"position": v(40.87, 75) * mm});
            skPoint(sketch, "E3.0.5.5", {"position": v(15.47, 70.97) * mm});
            skPoint(sketch, "E3.0.5.7", {"position": v(53.57, 75) * mm});
            skLineSegment(sketch, "E3.0.5.8", {"start": v(24.13, 70.97) * mm, "end": v(24.13, 66.34) * mm});
            skPoint(sketch, "E3.0.5.11", {"position": v(15.47, 79.04) * mm});
            skPoint(sketch, "E3.0.5.12", {"position": v(40.87, 70.97) * mm});
            skLineSegment(sketch, "E3.0.5.14", {"start": v(-18.59, 66.34) * mm, "end": v(6.81, 66.34) * mm, "construction": true});
            skLineSegment(sketch, "E3.0.5.15", {"start": v(83.01, 66.34) * mm, "end": v(87.63, 66.34) * mm});
            skLineSegment(sketch, "E3.0.5.17", {"start": v(70.31, 66.34) * mm, "end": v(70.31, 70.97) * mm});
            skLineSegment(sketch, "E3.0.5.18", {"start": v(95.71, 66.34) * mm, "end": v(95.71, 70.97) * mm});
            skLineSegment(sketch, "E3.0.5.19", {"start": v(49.53, 66.34) * mm, "end": v(44.91, 66.34) * mm});
            skLineSegment(sketch, "E3.0.5.21", {"start": v(49.53, 70.97) * mm, "end": v(49.53, 66.34) * mm});
            skPoint(sketch, "E3.0.5.29", {"position": v(40.87, 79.04) * mm});
            skLineSegment(sketch, "E3.0.5.30", {"start": v(74.93, 70.97) * mm, "end": v(74.93, 66.34) * mm});
            skPoint(sketch, "E3.0.5.34", {"position": v(66.27, 75) * mm});
            skLineSegment(sketch, "E3.0.5.35", {"start": v(11.43, 66.34) * mm, "end": v(11.43, 70.97) * mm});
            skLineSegment(sketch, "E3.0.5.37", {"start": v(100.33, 66.34) * mm, "end": v(95.71, 66.34) * mm});
            skPoint(sketch, "E3.0.5.41", {"position": v(78.97, 75) * mm});
            skLineSegment(sketch, "E3.0.5.43", {"start": v(100.33, 70.97) * mm, "end": v(100.33, 66.34) * mm});
            skPoint(sketch, "E3.0.5.45", {"position": v(66.27, 70.97) * mm});
            skLineSegment(sketch, "E3.0.5.46", {"start": v(36.83, 66.34) * mm, "end": v(36.83, 70.97) * mm});
            skLineSegment(sketch, "E3.0.5.47", {"start": v(6.81, 66.34) * mm, "end": v(6.81, 70.97) * mm});
            skPoint(sketch, "E3.0.5.49", {"position": v(91.67, 75) * mm});
            skLineSegment(sketch, "E3.0.5.51", {"start": v(62.23, 66.34) * mm, "end": v(62.23, 70.97) * mm});
            skLineSegment(sketch, "E3.0.5.52", {"start": v(32.21, 66.34) * mm, "end": v(32.21, 70.97) * mm});
            skLineSegment(sketch, "E3.0.5.58", {"start": v(89.36, 77.32) * mm, "end": v(89.36, 72.7) * mm});
            skPoint(sketch, "E3.0.5.65", {"position": v(66.27, 79.04) * mm});
            skPoint(sketch, "E3.0.5.66", {"position": v(91.67, 70.97) * mm});
            skLineSegment(sketch, "E3.0.5.68", {"start": v(87.63, 66.34) * mm, "end": v(87.63, 70.97) * mm});
            skLineSegment(sketch, "E3.0.5.69", {"start": v(57.61, 66.34) * mm, "end": v(57.61, 70.97) * mm});
            skPoint(sketch, "E3.0.5.79", {"position": v(91.67, 79.04) * mm});
            skLineSegment(sketch, "E3.0.5.82", {"start": v(43.18, 77.32) * mm, "end": v(43.18, 72.7) * mm});
            skLineSegment(sketch, "E3.0.5.83", {"start": v(19.51, 66.34) * mm, "end": v(19.51, 70.97) * mm});
            skPoint(sketch, "E3.0.5.85", {"position": v(15.47, 75) * mm});
            skLineSegment(sketch, "E3.0.5.87", {"start": v(83.01, 66.34) * mm, "end": v(83.01, 70.97) * mm});
            skLineSegment(sketch, "E3.0.5.88", {"start": v(32.21, 66.34) * mm, "end": v(36.83, 66.34) * mm});
            skPoint(sketch, "E3.0.5.92", {"position": v(231.37, 75) * mm});
            skLineSegment(sketch, "E3.0.5.93", {"start": v(25.86, 77.32) * mm, "end": v(25.86, 72.7) * mm});
            skLineSegment(sketch, "E3.0.5.94", {"start": v(44.91, 66.34) * mm, "end": v(44.91, 70.97) * mm});
            skLineSegment(sketch, "E3.0.5.95", {"start": v(25.86, 77.32) * mm, "end": v(30.48, 77.32) * mm});
            skLineSegment(sketch, "E3.0.5.99", {"start": v(93.98, 77.32) * mm, "end": v(93.98, 72.7) * mm});
            skLineSegment(sketch, "E3.0.5.104", {"start": v(13.16, 77.32) * mm, "end": v(13.16, 72.7) * mm});
            skLineSegment(sketch, "E3.0.5.105", {"start": v(51.26, 77.32) * mm, "end": v(51.26, 72.7) * mm});
            skLineSegment(sketch, "E3.0.5.106", {"start": v(76.66, 77.32) * mm, "end": v(76.66, 72.7) * mm});
            skLineSegment(sketch, "E3.0.5.109", {"start": v(38.56, 77.32) * mm, "end": v(38.56, 72.7) * mm});
            skLineSegment(sketch, "E3.0.5.110", {"start": v(30.48, 77.32) * mm, "end": v(30.48, 72.7) * mm});
            skLineSegment(sketch, "E3.0.5.115", {"start": v(63.96, 77.32) * mm, "end": v(63.96, 72.7) * mm});
            skLineSegment(sketch, "E3.0.5.116", {"start": v(55.88, 77.32) * mm, "end": v(55.88, 72.7) * mm});
            skLineSegment(sketch, "E3.0.5.122", {"start": v(25.86, 72.7) * mm, "end": v(30.48, 72.7) * mm});
            skLineSegment(sketch, "E3.0.5.123", {"start": v(81.28, 77.32) * mm, "end": v(81.28, 72.7) * mm});
            skLineSegment(sketch, "E3.0.5.124", {"start": v(43.18, 77.32) * mm, "end": v(38.56, 77.32) * mm});
            skLineSegment(sketch, "E3.0.5.127", {"start": v(43.18, 72.7) * mm, "end": v(38.56, 72.7) * mm});
            skLineSegment(sketch, "E3.0.5.128", {"start": v(17.78, 77.32) * mm, "end": v(17.78, 72.7) * mm});
            skLineSegment(sketch, "E3.0.5.139", {"start": v(93.98, 77.32) * mm, "end": v(89.36, 77.32) * mm});
            skLineSegment(sketch, "E3.0.5.141", {"start": v(93.98, 72.7) * mm, "end": v(89.36, 72.7) * mm});
            skLineSegment(sketch, "E3.0.5.142", {"start": v(68.58, 77.32) * mm, "end": v(68.58, 72.7) * mm});
            skLineSegment(sketch, "E3.0.5.145", {"start": v(24.13, 66.34) * mm, "end": v(19.51, 66.34) * mm});
            skLineSegment(sketch, "E3.0.5.146", {"start": v(57.61, 66.34) * mm, "end": v(62.23, 66.34) * mm});
            skLineSegment(sketch, "E3.0.5.147", {"start": v(9.12, 70.97) * mm, "end": v(11.43, 70.97) * mm});
            skLineSegment(sketch, "E3.0.5.149", {"start": v(6.81, 70.97) * mm, "end": v(9.12, 70.97) * mm});
            skLineSegment(sketch, "E3.0.5.151", {"start": v(51.26, 77.32) * mm, "end": v(55.88, 77.32) * mm});
            skLineSegment(sketch, "E3.0.5.152", {"start": v(76.66, 77.32) * mm, "end": v(81.28, 77.32) * mm});
            skLineSegment(sketch, "E3.0.5.153", {"start": v(32.21, 70.97) * mm, "end": v(34.52, 70.97) * mm});
            skLineSegment(sketch, "E3.0.5.154", {"start": v(70.31, 70.97) * mm, "end": v(72.62, 70.97) * mm});
            skLineSegment(sketch, "E3.0.5.156", {"start": v(44.91, 70.97) * mm, "end": v(47.22, 70.97) * mm});
            skLineSegment(sketch, "E3.0.5.162", {"start": v(74.93, 66.34) * mm, "end": v(70.31, 66.34) * mm});
            skLineSegment(sketch, "E3.0.5.163", {"start": v(34.52, 70.97) * mm, "end": v(36.83, 70.97) * mm});
            skLineSegment(sketch, "E3.0.5.164", {"start": v(21.82, 70.97) * mm, "end": v(24.13, 70.97) * mm});
            skLineSegment(sketch, "E3.0.5.166", {"start": v(95.71, 70.97) * mm, "end": v(98.02, 70.97) * mm});
            skLineSegment(sketch, "E3.0.5.167", {"start": v(57.61, 70.97) * mm, "end": v(59.92, 70.97) * mm});
            skLineSegment(sketch, "E3.0.5.170", {"start": v(59.92, 70.97) * mm, "end": v(62.23, 70.97) * mm});
            skLineSegment(sketch, "E3.0.5.171", {"start": v(47.22, 70.97) * mm, "end": v(49.53, 70.97) * mm});
            skLineSegment(sketch, "E3.0.5.173", {"start": v(83.01, 70.97) * mm, "end": v(85.32, 70.97) * mm});
            skLineSegment(sketch, "E3.0.5.175", {"start": v(17.78, 77.32) * mm, "end": v(13.16, 77.32) * mm});
            skLineSegment(sketch, "E3.0.5.178", {"start": v(72.62, 70.97) * mm, "end": v(74.93, 70.97) * mm});
            skLineSegment(sketch, "E3.0.5.182", {"start": v(85.32, 70.97) * mm, "end": v(87.63, 70.97) * mm});
            skLineSegment(sketch, "E3.0.5.184", {"start": v(98.02, 70.97) * mm, "end": v(100.33, 70.97) * mm});
            skLineSegment(sketch, "E3.0.5.190", {"start": v(17.78, 72.7) * mm, "end": v(13.16, 72.7) * mm});
            skLineSegment(sketch, "E3.0.5.192", {"start": v(68.58, 77.32) * mm, "end": v(63.96, 77.32) * mm});
            skLineSegment(sketch, "E3.0.5.194", {"start": v(51.26, 72.7) * mm, "end": v(55.88, 72.7) * mm});
            skLineSegment(sketch, "E3.0.5.195", {"start": v(6.81, 66.34) * mm, "end": v(11.43, 66.34) * mm});
            skLineSegment(sketch, "E3.0.5.208", {"start": v(68.58, 72.7) * mm, "end": v(63.96, 72.7) * mm});
            skLineSegment(sketch, "E3.0.5.211", {"start": v(76.66, 72.7) * mm, "end": v(81.28, 72.7) * mm});
            skLineSegment(sketch, "E3.0.5.212", {"start": v(19.51, 70.97) * mm, "end": v(21.82, 70.97) * mm});
            skPoint(sketch, "E3.0.6.0", {"position": v(40.87, 87.7) * mm});
            skPoint(sketch, "E3.0.6.5", {"position": v(15.47, 83.67) * mm});
            skPoint(sketch, "E3.0.6.7", {"position": v(53.57, 87.7) * mm});
            skLineSegment(sketch, "E3.0.6.8", {"start": v(24.13, 83.67) * mm, "end": v(24.13, 79.04) * mm});
            skPoint(sketch, "E3.0.6.12", {"position": v(40.87, 83.67) * mm});
            skLineSegment(sketch, "E3.0.6.14", {"start": v(-18.59, 79.04) * mm, "end": v(6.81, 79.04) * mm, "construction": true});
            skLineSegment(sketch, "E3.0.6.15", {"start": v(83.01, 79.04) * mm, "end": v(87.63, 79.04) * mm});
            skLineSegment(sketch, "E3.0.6.17", {"start": v(70.31, 79.04) * mm, "end": v(70.31, 83.67) * mm});
            skLineSegment(sketch, "E3.0.6.18", {"start": v(95.71, 79.04) * mm, "end": v(95.71, 83.67) * mm});
            skLineSegment(sketch, "E3.0.6.19", {"start": v(49.53, 79.04) * mm, "end": v(44.91, 79.04) * mm});
            skLineSegment(sketch, "E3.0.6.21", {"start": v(49.53, 83.67) * mm, "end": v(49.53, 79.04) * mm});
            skLineSegment(sketch, "E3.0.6.30", {"start": v(74.93, 83.67) * mm, "end": v(74.93, 79.04) * mm});
            skPoint(sketch, "E3.0.6.34", {"position": v(66.27, 87.7) * mm});
            skLineSegment(sketch, "E3.0.6.35", {"start": v(11.43, 79.04) * mm, "end": v(11.43, 83.67) * mm});
            skLineSegment(sketch, "E3.0.6.37", {"start": v(100.33, 79.04) * mm, "end": v(95.71, 79.04) * mm});
            skPoint(sketch, "E3.0.6.41", {"position": v(78.97, 87.7) * mm});
            skLineSegment(sketch, "E3.0.6.43", {"start": v(100.33, 83.67) * mm, "end": v(100.33, 79.04) * mm});
            skPoint(sketch, "E3.0.6.45", {"position": v(66.27, 83.67) * mm});
            skLineSegment(sketch, "E3.0.6.46", {"start": v(36.83, 79.04) * mm, "end": v(36.83, 83.67) * mm});
            skLineSegment(sketch, "E3.0.6.47", {"start": v(6.81, 79.04) * mm, "end": v(6.81, 83.67) * mm});
            skPoint(sketch, "E3.0.6.49", {"position": v(91.67, 87.7) * mm});
            skLineSegment(sketch, "E3.0.6.51", {"start": v(62.23, 79.04) * mm, "end": v(62.23, 83.67) * mm});
            skLineSegment(sketch, "E3.0.6.52", {"start": v(32.21, 79.04) * mm, "end": v(32.21, 83.67) * mm});
            skLineSegment(sketch, "E3.0.6.58", {"start": v(89.36, 90.02) * mm, "end": v(89.36, 85.4) * mm});
            skPoint(sketch, "E3.0.6.66", {"position": v(91.67, 83.67) * mm});
            skLineSegment(sketch, "E3.0.6.68", {"start": v(87.63, 79.04) * mm, "end": v(87.63, 83.67) * mm});
            skLineSegment(sketch, "E3.0.6.69", {"start": v(57.61, 79.04) * mm, "end": v(57.61, 83.67) * mm});
            skLineSegment(sketch, "E3.0.6.82", {"start": v(43.18, 90.02) * mm, "end": v(43.18, 85.4) * mm});
            skLineSegment(sketch, "E3.0.6.83", {"start": v(19.51, 79.04) * mm, "end": v(19.51, 83.67) * mm});
            skPoint(sketch, "E3.0.6.85", {"position": v(15.47, 87.7) * mm});
            skLineSegment(sketch, "E3.0.6.87", {"start": v(83.01, 79.04) * mm, "end": v(83.01, 83.67) * mm});
            skLineSegment(sketch, "E3.0.6.88", {"start": v(32.21, 79.04) * mm, "end": v(36.83, 79.04) * mm});
            skPoint(sketch, "E3.0.6.92", {"position": v(231.37, 87.7) * mm});
            skLineSegment(sketch, "E3.0.6.93", {"start": v(25.86, 90.02) * mm, "end": v(25.86, 85.4) * mm});
            skLineSegment(sketch, "E3.0.6.94", {"start": v(44.91, 79.04) * mm, "end": v(44.91, 83.67) * mm});
            skLineSegment(sketch, "E3.0.6.95", {"start": v(25.86, 90.02) * mm, "end": v(30.48, 90.02) * mm});
            skLineSegment(sketch, "E3.0.6.99", {"start": v(93.98, 90.02) * mm, "end": v(93.98, 85.4) * mm});
            skLineSegment(sketch, "E3.0.6.104", {"start": v(13.16, 90.02) * mm, "end": v(13.16, 85.4) * mm});
            skLineSegment(sketch, "E3.0.6.105", {"start": v(51.26, 90.02) * mm, "end": v(51.26, 85.4) * mm});
            skLineSegment(sketch, "E3.0.6.106", {"start": v(76.66, 90.02) * mm, "end": v(76.66, 85.4) * mm});
            skLineSegment(sketch, "E3.0.6.109", {"start": v(38.56, 90.02) * mm, "end": v(38.56, 85.4) * mm});
            skLineSegment(sketch, "E3.0.6.110", {"start": v(30.48, 90.02) * mm, "end": v(30.48, 85.4) * mm});
            skLineSegment(sketch, "E3.0.6.115", {"start": v(63.96, 90.02) * mm, "end": v(63.96, 85.4) * mm});
            skLineSegment(sketch, "E3.0.6.116", {"start": v(55.88, 90.02) * mm, "end": v(55.88, 85.4) * mm});
            skLineSegment(sketch, "E3.0.6.122", {"start": v(25.86, 85.4) * mm, "end": v(30.48, 85.4) * mm});
            skLineSegment(sketch, "E3.0.6.123", {"start": v(81.28, 90.02) * mm, "end": v(81.28, 85.4) * mm});
            skLineSegment(sketch, "E3.0.6.124", {"start": v(43.18, 90.02) * mm, "end": v(38.56, 90.02) * mm});
            skLineSegment(sketch, "E3.0.6.127", {"start": v(43.18, 85.4) * mm, "end": v(38.56, 85.4) * mm});
            skLineSegment(sketch, "E3.0.6.128", {"start": v(17.78, 90.02) * mm, "end": v(17.78, 85.4) * mm});
            skLineSegment(sketch, "E3.0.6.139", {"start": v(93.98, 90.02) * mm, "end": v(89.36, 90.02) * mm});
            skLineSegment(sketch, "E3.0.6.141", {"start": v(93.98, 85.4) * mm, "end": v(89.36, 85.4) * mm});
            skLineSegment(sketch, "E3.0.6.142", {"start": v(68.58, 90.02) * mm, "end": v(68.58, 85.4) * mm});
            skLineSegment(sketch, "E3.0.6.145", {"start": v(24.13, 79.04) * mm, "end": v(19.51, 79.04) * mm});
            skLineSegment(sketch, "E3.0.6.146", {"start": v(57.61, 79.04) * mm, "end": v(62.23, 79.04) * mm});
            skLineSegment(sketch, "E3.0.6.147", {"start": v(9.12, 83.67) * mm, "end": v(11.43, 83.67) * mm});
            skLineSegment(sketch, "E3.0.6.149", {"start": v(6.81, 83.67) * mm, "end": v(9.12, 83.67) * mm});
            skLineSegment(sketch, "E3.0.6.151", {"start": v(51.26, 90.02) * mm, "end": v(55.88, 90.02) * mm});
            skLineSegment(sketch, "E3.0.6.152", {"start": v(76.66, 90.02) * mm, "end": v(81.28, 90.02) * mm});
            skLineSegment(sketch, "E3.0.6.153", {"start": v(32.21, 83.67) * mm, "end": v(34.52, 83.67) * mm});
            skLineSegment(sketch, "E3.0.6.154", {"start": v(70.31, 83.67) * mm, "end": v(72.62, 83.67) * mm});
            skLineSegment(sketch, "E3.0.6.156", {"start": v(44.91, 83.67) * mm, "end": v(47.22, 83.67) * mm});
            skLineSegment(sketch, "E3.0.6.162", {"start": v(74.93, 79.04) * mm, "end": v(70.31, 79.04) * mm});
            skLineSegment(sketch, "E3.0.6.163", {"start": v(34.52, 83.67) * mm, "end": v(36.83, 83.67) * mm});
            skLineSegment(sketch, "E3.0.6.164", {"start": v(21.82, 83.67) * mm, "end": v(24.13, 83.67) * mm});
            skLineSegment(sketch, "E3.0.6.166", {"start": v(95.71, 83.67) * mm, "end": v(98.02, 83.67) * mm});
            skLineSegment(sketch, "E3.0.6.167", {"start": v(57.61, 83.67) * mm, "end": v(59.92, 83.67) * mm});
            skLineSegment(sketch, "E3.0.6.170", {"start": v(59.92, 83.67) * mm, "end": v(62.23, 83.67) * mm});
            skLineSegment(sketch, "E3.0.6.171", {"start": v(47.22, 83.67) * mm, "end": v(49.53, 83.67) * mm});
            skLineSegment(sketch, "E3.0.6.173", {"start": v(83.01, 83.67) * mm, "end": v(85.32, 83.67) * mm});
            skLineSegment(sketch, "E3.0.6.175", {"start": v(17.78, 90.02) * mm, "end": v(13.16, 90.02) * mm});
            skLineSegment(sketch, "E3.0.6.178", {"start": v(72.62, 83.67) * mm, "end": v(74.93, 83.67) * mm});
            skLineSegment(sketch, "E3.0.6.182", {"start": v(85.32, 83.67) * mm, "end": v(87.63, 83.67) * mm});
            skLineSegment(sketch, "E3.0.6.184", {"start": v(98.02, 83.67) * mm, "end": v(100.33, 83.67) * mm});
            skLineSegment(sketch, "E3.0.6.190", {"start": v(17.78, 85.4) * mm, "end": v(13.16, 85.4) * mm});
            skLineSegment(sketch, "E3.0.6.192", {"start": v(68.58, 90.02) * mm, "end": v(63.96, 90.02) * mm});
            skLineSegment(sketch, "E3.0.6.194", {"start": v(51.26, 85.4) * mm, "end": v(55.88, 85.4) * mm});
            skLineSegment(sketch, "E3.0.6.195", {"start": v(6.81, 79.04) * mm, "end": v(11.43, 79.04) * mm});
            skLineSegment(sketch, "E3.0.6.208", {"start": v(68.58, 85.4) * mm, "end": v(63.96, 85.4) * mm});
            skLineSegment(sketch, "E3.0.6.211", {"start": v(76.66, 85.4) * mm, "end": v(81.28, 85.4) * mm});
            skLineSegment(sketch, "E3.0.6.212", {"start": v(19.51, 83.67) * mm, "end": v(21.82, 83.67) * mm});
            skPoint(sketch, "E3.0.7.92", {"position": v(231.37, 100.4) * mm});
            skPoint(sketch, "E3.0.8.92", {"position": v(231.37, 113.1) * mm});
            skLineSegment(sketch, "E4", {"start": v(98.02, 0) * mm, "end": v(40.87, 0) * mm});
            skLineSegment(sketch, "E5", {"start": v(40.87, 0) * mm, "end": v(-3.37, 44.86) * mm});
            skLineSegment(sketch, "E6", {"start": v(-3.37, 44.86) * mm, "end": v(-3.37, 49.6) * mm});
            skLineSegment(sketch, "E7.MirrorCS", {"start": v(32.21, 104.45) * mm, "end": v(34.52, 104.45) * mm});
            skLineSegment(sketch, "E8.MirrorCS", {"start": v(32.21, 91.75) * mm, "end": v(34.52, 91.75) * mm});
            skLineSegment(sketch, "E9.MirrorCS", {"start": v(47.22, 142.55) * mm, "end": v(49.53, 142.55) * mm});
            skLineSegment(sketch, "E10.MirrorCS", {"start": v(95.71, 167.95) * mm, "end": v(98.02, 167.95) * mm});
            skLineSegment(sketch, "E11.MirrorCS", {"start": v(95.71, 155.25) * mm, "end": v(98.02, 155.25) * mm});
            skLineSegment(sketch, "E12.MirrorCS", {"start": v(57.61, 142.55) * mm, "end": v(59.92, 142.55) * mm});
            skLineSegment(sketch, "E13.MirrorCS", {"start": v(70.31, 117.15) * mm, "end": v(72.62, 117.15) * mm});
            skLineSegment(sketch, "E14.MirrorCS", {"start": v(34.52, 91.75) * mm, "end": v(36.83, 91.75) * mm});
            skLineSegment(sketch, "E15.MirrorCS", {"start": v(70.31, 104.45) * mm, "end": v(72.62, 104.45) * mm});
            skLineSegment(sketch, "E16.MirrorCS", {"start": v(83.01, 155.25) * mm, "end": v(85.32, 155.25) * mm});
            skLineSegment(sketch, "E17.MirrorCS", {"start": v(21.82, 117.15) * mm, "end": v(24.13, 117.15) * mm});
            skLineSegment(sketch, "E18.MirrorCS", {"start": v(21.82, 104.45) * mm, "end": v(24.13, 104.45) * mm});
            skLineSegment(sketch, "E19.MirrorCS", {"start": v(72.62, 155.25) * mm, "end": v(74.93, 155.25) * mm});
            skLineSegment(sketch, "E20.MirrorCS", {"start": v(72.62, 142.55) * mm, "end": v(74.93, 142.55) * mm});
            skLineSegment(sketch, "E21.MirrorCS", {"start": v(34.52, 129.85) * mm, "end": v(36.83, 129.85) * mm});
            skLineSegment(sketch, "E22.MirrorCS", {"start": v(83.01, 142.55) * mm, "end": v(85.32, 142.55) * mm});
            skLineSegment(sketch, "E23.MirrorCS", {"start": v(95.71, 117.15) * mm, "end": v(98.02, 117.15) * mm});
            skLineSegment(sketch, "E24.MirrorCS", {"start": v(95.71, 104.45) * mm, "end": v(98.02, 104.45) * mm});
            skLineSegment(sketch, "E25.MirrorCS", {"start": v(34.52, 117.15) * mm, "end": v(36.83, 117.15) * mm});
            skLineSegment(sketch, "E26.MirrorCS", {"start": v(34.52, 104.45) * mm, "end": v(36.83, 104.45) * mm});
            skLineSegment(sketch, "E27.MirrorCS", {"start": v(95.71, 91.75) * mm, "end": v(98.02, 91.75) * mm});
            skLineSegment(sketch, "E28.MirrorCS", {"start": v(59.92, 167.95) * mm, "end": v(62.23, 167.95) * mm});
            skLineSegment(sketch, "E29.MirrorCS", {"start": v(85.32, 142.55) * mm, "end": v(87.63, 142.55) * mm});
            skLineSegment(sketch, "E30.MirrorCS", {"start": v(21.82, 129.85) * mm, "end": v(24.13, 129.85) * mm});
            skLineSegment(sketch, "E31.MirrorCS", {"start": v(57.61, 117.15) * mm, "end": v(59.92, 117.15) * mm});
            skLineSegment(sketch, "E32.MirrorCS", {"start": v(57.61, 104.45) * mm, "end": v(59.92, 104.45) * mm});
            skLineSegment(sketch, "E33.MirrorCS", {"start": v(57.61, 91.75) * mm, "end": v(59.92, 91.75) * mm});
            skLineSegment(sketch, "E34.MirrorCS", {"start": v(85.32, 155.25) * mm, "end": v(87.63, 155.25) * mm});
            skLineSegment(sketch, "E35.MirrorCS", {"start": v(95.71, 129.85) * mm, "end": v(98.02, 129.85) * mm});
            skLineSegment(sketch, "E36.MirrorCS", {"start": v(19.51, 117.15) * mm, "end": v(21.82, 117.15) * mm});
            skLineSegment(sketch, "E37.MirrorCS", {"start": v(59.92, 117.15) * mm, "end": v(62.23, 117.15) * mm});
            skLineSegment(sketch, "E38.MirrorCS", {"start": v(59.92, 104.45) * mm, "end": v(62.23, 104.45) * mm});
            skLineSegment(sketch, "E39.MirrorCS", {"start": v(19.51, 104.45) * mm, "end": v(21.82, 104.45) * mm});
            skLineSegment(sketch, "E40.MirrorCS", {"start": v(70.31, 91.75) * mm, "end": v(72.62, 91.75) * mm});
            skLineSegment(sketch, "E41.MirrorCS", {"start": v(59.92, 91.75) * mm, "end": v(62.23, 91.75) * mm});
            skLineSegment(sketch, "E42.MirrorCS", {"start": v(19.51, 91.75) * mm, "end": v(21.82, 91.75) * mm});
            skLineSegment(sketch, "E43.MirrorCS", {"start": v(72.62, 167.95) * mm, "end": v(74.93, 167.95) * mm});
            skLineSegment(sketch, "E44.MirrorCS", {"start": v(98.02, 155.25) * mm, "end": v(100.33, 155.25) * mm});
            skLineSegment(sketch, "E45.MirrorCS", {"start": v(98.02, 142.55) * mm, "end": v(100.33, 142.55) * mm});
            skLineSegment(sketch, "E46.MirrorCS", {"start": v(85.32, 167.95) * mm, "end": v(87.63, 167.95) * mm});
            skLineSegment(sketch, "E47.MirrorCS", {"start": v(47.22, 117.15) * mm, "end": v(49.53, 117.15) * mm});
            skLineSegment(sketch, "E48.MirrorCS", {"start": v(83.01, 167.95) * mm, "end": v(85.32, 167.95) * mm});
            skLineSegment(sketch, "E49.MirrorCS", {"start": v(47.22, 104.45) * mm, "end": v(49.53, 104.45) * mm});
            skLineSegment(sketch, "E50.MirrorCS", {"start": v(72.62, 129.85) * mm, "end": v(74.93, 129.85) * mm});
            skLineSegment(sketch, "E51.MirrorCS", {"start": v(19.51, 142.55) * mm, "end": v(21.82, 142.55) * mm});
            skLineSegment(sketch, "E52.MirrorCS", {"start": v(47.22, 91.75) * mm, "end": v(49.53, 91.75) * mm});
            skLineSegment(sketch, "E53.MirrorCS", {"start": v(6.81, 129.85) * mm, "end": v(9.12, 129.85) * mm});
            skLineSegment(sketch, "E54.MirrorCS", {"start": v(70.31, 167.95) * mm, "end": v(72.62, 167.95) * mm});
            skLineSegment(sketch, "E55.MirrorCS", {"start": v(98.02, 167.95) * mm, "end": v(100.33, 167.95) * mm});
            skLineSegment(sketch, "E56.MirrorCS", {"start": v(9.12, 91.75) * mm, "end": v(11.43, 91.75) * mm});
            skLineSegment(sketch, "E57.MirrorCS", {"start": v(32.21, 155.25) * mm, "end": v(34.52, 155.25) * mm});
            skLineSegment(sketch, "E58.MirrorCS", {"start": v(57.61, 155.25) * mm, "end": v(59.92, 155.25) * mm});
            skLineSegment(sketch, "E59.MirrorCS", {"start": v(57.61, 129.85) * mm, "end": v(59.92, 129.85) * mm});
            skLineSegment(sketch, "E60.MirrorCS", {"start": v(83.01, 104.45) * mm, "end": v(85.32, 104.45) * mm});
            skLineSegment(sketch, "E61.MirrorCS", {"start": v(83.01, 91.75) * mm, "end": v(85.32, 91.75) * mm});
            skLineSegment(sketch, "E62.MirrorCS", {"start": v(32.21, 142.55) * mm, "end": v(34.52, 142.55) * mm});
            skLineSegment(sketch, "E63.MirrorCS", {"start": v(34.52, 155.25) * mm, "end": v(36.83, 155.25) * mm});
            skLineSegment(sketch, "E64.MirrorCS", {"start": v(19.51, 129.85) * mm, "end": v(21.82, 129.85) * mm});
            skLineSegment(sketch, "E65.MirrorCS", {"start": v(59.92, 129.85) * mm, "end": v(62.23, 129.85) * mm});
            skLineSegment(sketch, "E66.MirrorCS", {"start": v(83.01, 117.15) * mm, "end": v(85.32, 117.15) * mm});
            skLineSegment(sketch, "E67.MirrorCS", {"start": v(59.92, 142.55) * mm, "end": v(62.23, 142.55) * mm});
            skLineSegment(sketch, "E68.MirrorCS", {"start": v(95.71, 142.55) * mm, "end": v(98.02, 142.55) * mm});
            skLineSegment(sketch, "E69.MirrorCS", {"start": v(98.02, 129.85) * mm, "end": v(100.33, 129.85) * mm});
            skLineSegment(sketch, "E70.MirrorCS", {"start": v(44.91, 167.95) * mm, "end": v(47.22, 167.95) * mm});
            skLineSegment(sketch, "E71.MirrorCS", {"start": v(32.21, 117.15) * mm, "end": v(34.52, 117.15) * mm});
            skLineSegment(sketch, "E72.MirrorCS", {"start": v(44.91, 91.75) * mm, "end": v(47.22, 91.75) * mm});
            skLineSegment(sketch, "E73.MirrorCS", {"start": v(70.31, 142.55) * mm, "end": v(72.62, 142.55) * mm});
            skLineSegment(sketch, "E74.MirrorCS", {"start": v(47.22, 129.85) * mm, "end": v(49.53, 129.85) * mm});
            skLineSegment(sketch, "E75.MirrorCS", {"start": v(72.62, 91.75) * mm, "end": v(74.93, 91.75) * mm});
            skLineSegment(sketch, "E76.MirrorCS", {"start": v(32.21, 129.85) * mm, "end": v(34.52, 129.85) * mm});
            skLineSegment(sketch, "E77.MirrorCS", {"start": v(44.91, 142.55) * mm, "end": v(47.22, 142.55) * mm});
            skLineSegment(sketch, "E78.MirrorCS", {"start": v(83.01, 129.85) * mm, "end": v(85.32, 129.85) * mm});
            skLineSegment(sketch, "E79.MirrorCS", {"start": v(72.62, 117.15) * mm, "end": v(74.93, 117.15) * mm});
            skLineSegment(sketch, "E80.MirrorCS", {"start": v(9.12, 117.15) * mm, "end": v(11.43, 117.15) * mm});
            skLineSegment(sketch, "E81.MirrorCS", {"start": v(72.62, 104.45) * mm, "end": v(74.93, 104.45) * mm});
            skLineSegment(sketch, "E82.MirrorCS", {"start": v(9.12, 104.45) * mm, "end": v(11.43, 104.45) * mm});
            skLineSegment(sketch, "E83.MirrorCS", {"start": v(70.31, 155.25) * mm, "end": v(72.62, 155.25) * mm});
            skLineSegment(sketch, "E84.MirrorCS", {"start": v(85.32, 117.15) * mm, "end": v(87.63, 117.15) * mm});
            skLineSegment(sketch, "E85.MirrorCS", {"start": v(44.91, 117.15) * mm, "end": v(47.22, 117.15) * mm});
            skLineSegment(sketch, "E86.MirrorCS", {"start": v(6.81, 117.15) * mm, "end": v(9.12, 117.15) * mm});
            skLineSegment(sketch, "E87.MirrorCS", {"start": v(6.81, 104.45) * mm, "end": v(9.12, 104.45) * mm});
            skLineSegment(sketch, "E88.MirrorCS", {"start": v(85.32, 104.45) * mm, "end": v(87.63, 104.45) * mm});
            skLineSegment(sketch, "E89.MirrorCS", {"start": v(85.32, 91.75) * mm, "end": v(87.63, 91.75) * mm});
            skLineSegment(sketch, "E90.MirrorCS", {"start": v(6.81, 91.75) * mm, "end": v(9.12, 91.75) * mm});
            skLineSegment(sketch, "E91.MirrorCS", {"start": v(47.22, 167.95) * mm, "end": v(49.53, 167.95) * mm});
            skLineSegment(sketch, "E92.MirrorCS", {"start": v(59.92, 155.25) * mm, "end": v(62.23, 155.25) * mm});
            skLineSegment(sketch, "E93.MirrorCS", {"start": v(44.91, 155.25) * mm, "end": v(47.22, 155.25) * mm});
            skLineSegment(sketch, "E94.MirrorCS", {"start": v(34.52, 142.55) * mm, "end": v(36.83, 142.55) * mm});
            skLineSegment(sketch, "E95.MirrorCS", {"start": v(44.91, 104.45) * mm, "end": v(47.22, 104.45) * mm});
            skLineSegment(sketch, "E96.MirrorCS", {"start": v(70.31, 129.85) * mm, "end": v(72.62, 129.85) * mm});
            skLineSegment(sketch, "E97.MirrorCS", {"start": v(9.12, 129.85) * mm, "end": v(11.43, 129.85) * mm});
            skLineSegment(sketch, "E98.MirrorCS", {"start": v(98.02, 117.15) * mm, "end": v(100.33, 117.15) * mm});
            skLineSegment(sketch, "E99.MirrorCS", {"start": v(98.02, 104.45) * mm, "end": v(100.33, 104.45) * mm});
            skLineSegment(sketch, "E100.MirrorCS", {"start": v(98.02, 91.75) * mm, "end": v(100.33, 91.75) * mm});
            skLineSegment(sketch, "E101.MirrorCS", {"start": v(57.61, 167.95) * mm, "end": v(59.92, 167.95) * mm});
            skLineSegment(sketch, "E102.MirrorCS", {"start": v(21.82, 142.55) * mm, "end": v(24.13, 142.55) * mm});
            skLineSegment(sketch, "E103.MirrorCS", {"start": v(47.22, 155.25) * mm, "end": v(49.53, 155.25) * mm});
            skLineSegment(sketch, "E104.MirrorCS", {"start": v(44.91, 129.85) * mm, "end": v(47.22, 129.85) * mm});
            skLineSegment(sketch, "E105.MirrorCS", {"start": v(85.32, 129.85) * mm, "end": v(87.63, 129.85) * mm});
            skLineSegment(sketch, "E106.MirrorCS", {"start": v(21.82, 91.75) * mm, "end": v(24.13, 91.75) * mm});
            skLineSegment(sketch, "E107.MirrorCS", {"start": v(93.98, 136.2) * mm, "end": v(89.36, 136.2) * mm});
            skLineSegment(sketch, "E108.MirrorCS", {"start": v(17.78, 102.72) * mm, "end": v(13.16, 102.72) * mm});
            skLineSegment(sketch, "E109.MirrorCS", {"start": v(43.18, 140.82) * mm, "end": v(38.56, 140.82) * mm});
            skLineSegment(sketch, "E110.MirrorCS", {"start": v(68.58, 110.8) * mm, "end": v(63.96, 110.8) * mm});
            skLineSegment(sketch, "E111.MirrorCS", {"start": v(43.18, 110.8) * mm, "end": v(38.56, 110.8) * mm});
            skLineSegment(sketch, "E112.MirrorCS", {"start": v(43.18, 148.9) * mm, "end": v(38.56, 148.9) * mm});
            skLineSegment(sketch, "E113.MirrorCS", {"start": v(43.18, 98.1) * mm, "end": v(38.56, 98.1) * mm});
            skLineSegment(sketch, "E114.MirrorCS", {"start": v(17.78, 136.2) * mm, "end": v(13.16, 136.2) * mm});
            skLineSegment(sketch, "E115.MirrorCS", {"start": v(68.58, 115.42) * mm, "end": v(63.96, 115.42) * mm});
            skLineSegment(sketch, "E116.MirrorCS", {"start": v(93.98, 110.8) * mm, "end": v(89.36, 110.8) * mm});
            skLineSegment(sketch, "E117.MirrorCS", {"start": v(68.58, 102.72) * mm, "end": v(63.96, 102.72) * mm});
            skLineSegment(sketch, "E118.MirrorCS", {"start": v(93.98, 98.1) * mm, "end": v(89.36, 98.1) * mm});
            skLineSegment(sketch, "E119.MirrorCS", {"start": v(43.18, 128.12) * mm, "end": v(38.56, 128.12) * mm});
            skLineSegment(sketch, "E120.MirrorCS", {"start": v(93.98, 148.9) * mm, "end": v(89.36, 148.9) * mm});
            skLineSegment(sketch, "E121.MirrorCS", {"start": v(93.98, 85.4) * mm, "end": v(93.98, 90.02) * mm});
            skLineSegment(sketch, "E122.MirrorCS", {"start": v(93.98, 153.52) * mm, "end": v(89.36, 153.52) * mm});
            skLineSegment(sketch, "E123.MirrorCS", {"start": v(68.58, 128.12) * mm, "end": v(63.96, 128.12) * mm});
            skLineSegment(sketch, "E124.MirrorCS", {"start": v(68.58, 98.1) * mm, "end": v(63.96, 98.1) * mm});
            skLineSegment(sketch, "E125.MirrorCS", {"start": v(93.98, 115.42) * mm, "end": v(89.36, 115.42) * mm});
            skLineSegment(sketch, "E126.MirrorCS", {"start": v(93.98, 102.72) * mm, "end": v(89.36, 102.72) * mm});
            skLineSegment(sketch, "E127.MirrorCS", {"start": v(93.98, 123.5) * mm, "end": v(89.36, 123.5) * mm});
            skLineSegment(sketch, "E128.MirrorCS", {"start": v(68.58, 166.22) * mm, "end": v(63.96, 166.22) * mm});
            skLineSegment(sketch, "E129.MirrorCS", {"start": v(17.78, 123.5) * mm, "end": v(13.16, 123.5) * mm});
            skLineSegment(sketch, "E130.MirrorCS", {"start": v(68.58, 148.9) * mm, "end": v(63.96, 148.9) * mm});
            skLineSegment(sketch, "E131.MirrorCS", {"start": v(93.98, 128.12) * mm, "end": v(89.36, 128.12) * mm});
            skLineSegment(sketch, "E132.MirrorCS", {"start": v(43.18, 136.2) * mm, "end": v(38.56, 136.2) * mm});
            skLineSegment(sketch, "E133.MirrorCS", {"start": v(17.78, 115.42) * mm, "end": v(13.16, 115.42) * mm});
            skLineSegment(sketch, "E134.MirrorCS", {"start": v(68.58, 161.6) * mm, "end": v(63.96, 161.6) * mm});
            skLineSegment(sketch, "E135.MirrorCS", {"start": v(17.78, 128.12) * mm, "end": v(13.16, 128.12) * mm});
            skLineSegment(sketch, "E136.MirrorCS", {"start": v(93.98, 161.6) * mm, "end": v(89.36, 161.6) * mm});
            skLineSegment(sketch, "E137.MirrorCS", {"start": v(68.58, 136.2) * mm, "end": v(63.96, 136.2) * mm});
            skLineSegment(sketch, "E138.MirrorCS", {"start": v(17.78, 110.8) * mm, "end": v(13.16, 110.8) * mm});
            skLineSegment(sketch, "E139.MirrorCS", {"start": v(17.78, 98.1) * mm, "end": v(13.16, 98.1) * mm});
            skLineSegment(sketch, "E140.MirrorCS", {"start": v(68.58, 153.52) * mm, "end": v(63.96, 153.52) * mm});
            skLineSegment(sketch, "E141.MirrorCS", {"start": v(93.98, 166.22) * mm, "end": v(89.36, 166.22) * mm});
            skLineSegment(sketch, "E142.MirrorCS", {"start": v(68.58, 140.82) * mm, "end": v(63.96, 140.82) * mm});
            skLineSegment(sketch, "E143.MirrorCS", {"start": v(17.78, 85.4) * mm, "end": v(17.78, 90.02) * mm});
            skLineSegment(sketch, "E144.MirrorCS", {"start": v(43.18, 115.42) * mm, "end": v(38.56, 115.42) * mm});
            skLineSegment(sketch, "E145.MirrorCS", {"start": v(68.58, 123.5) * mm, "end": v(63.96, 123.5) * mm});
            skLineSegment(sketch, "E146.MirrorCS", {"start": v(43.18, 102.72) * mm, "end": v(38.56, 102.72) * mm});
            skLineSegment(sketch, "E147.MirrorCS", {"start": v(43.18, 161.6) * mm, "end": v(38.56, 161.6) * mm});
            skLineSegment(sketch, "E148.MirrorCS", {"start": v(25.86, 85.4) * mm, "end": v(25.86, 90.02) * mm});
            skLineSegment(sketch, "E149.MirrorCS", {"start": v(93.98, 140.82) * mm, "end": v(89.36, 140.82) * mm});
            skLineSegment(sketch, "E150.MirrorCS", {"start": v(43.18, 166.22) * mm, "end": v(38.56, 166.22) * mm});
            skLineSegment(sketch, "E151.MirrorCS", {"start": v(43.18, 123.5) * mm, "end": v(38.56, 123.5) * mm});
            skLineSegment(sketch, "E152.MirrorCS", {"start": v(43.18, 153.52) * mm, "end": v(38.56, 153.52) * mm});
            skPoint(sketch, "E153.MirrorP", {"position": v(15.47, 121.77) * mm});
            skPoint(sketch, "E154.MirrorP", {"position": v(91.67, 109.07) * mm});
            skLineSegment(sketch, "E155.MirrorCS", {"start": v(81.28, 148.9) * mm, "end": v(81.28, 153.52) * mm});
            skPoint(sketch, "E156.MirrorP", {"position": v(53.57, 151.21) * mm});
            skPoint(sketch, "E157.MirrorP", {"position": v(91.67, 113.11) * mm});
            skLineSegment(sketch, "E158.MirrorCS", {"start": v(81.28, 98.1) * mm, "end": v(81.28, 102.72) * mm});
            skLineSegment(sketch, "E159.MirrorCS", {"start": v(43.18, 98.1) * mm, "end": v(43.18, 102.72) * mm});
            skLineSegment(sketch, "E160.MirrorCS", {"start": v(43.18, 123.5) * mm, "end": v(43.18, 128.12) * mm});
            skLineSegment(sketch, "E161.MirrorCS", {"start": v(95.71, 109.07) * mm, "end": v(95.71, 104.45) * mm});
            skLineSegment(sketch, "E162.MirrorCS", {"start": v(95.71, 96.37) * mm, "end": v(95.71, 91.75) * mm});
            skPoint(sketch, "E163.MirrorP", {"position": v(91.67, 96.37) * mm});
            skLineSegment(sketch, "E164.MirrorCS", {"start": v(81.28, 85.4) * mm, "end": v(81.28, 90.02) * mm});
            skPoint(sketch, "E165.MirrorP", {"position": v(91.67, 100.41) * mm});
            skLineSegment(sketch, "E166.MirrorCS", {"start": v(32.21, 121.77) * mm, "end": v(36.83, 121.77) * mm});
            skLineSegment(sketch, "E167.MirrorCS", {"start": v(43.18, 85.4) * mm, "end": v(43.18, 90.02) * mm});
            skPoint(sketch, "E168.MirrorP", {"position": v(91.67, 142.55) * mm});
            skLineSegment(sketch, "E169.MirrorCS", {"start": v(32.21, 159.87) * mm, "end": v(32.21, 155.25) * mm});
            skLineSegment(sketch, "E170.MirrorCS", {"start": v(70.31, 172.57) * mm, "end": v(70.31, 167.95) * mm});
            skLineSegment(sketch, "E171.MirrorCS", {"start": v(83.01, 147.17) * mm, "end": v(83.01, 142.55) * mm});
            skLineSegment(sketch, "E172.MirrorCS", {"start": v(83.01, 147.17) * mm, "end": v(87.63, 147.17) * mm});
            skLineSegment(sketch, "E173.MirrorCS", {"start": v(55.88, 148.9) * mm, "end": v(55.88, 153.52) * mm});
            skLineSegment(sketch, "E174.MirrorCS", {"start": v(87.63, 134.47) * mm, "end": v(87.63, 129.85) * mm});
            skLineSegment(sketch, "E175.MirrorCS", {"start": v(24.13, 129.85) * mm, "end": v(24.13, 134.47) * mm});
            skLineSegment(sketch, "E176.MirrorCS", {"start": v(49.53, 121.77) * mm, "end": v(44.91, 121.77) * mm});
            skLineSegment(sketch, "E177.MirrorCS", {"start": v(76.66, 123.5) * mm, "end": v(81.28, 123.5) * mm});
            skLineSegment(sketch, "E178.MirrorCS", {"start": v(55.88, 123.5) * mm, "end": v(55.88, 128.12) * mm});
            skPoint(sketch, "E179.MirrorP", {"position": v(40.87, 91.75) * mm});
            skLineSegment(sketch, "E180.MirrorCS", {"start": v(17.78, 110.8) * mm, "end": v(17.78, 115.42) * mm});
            skPoint(sketch, "E181.MirrorP", {"position": v(91.67, 151.21) * mm});
            skPoint(sketch, "E182.MirrorP", {"position": v(66.27, 142.55) * mm});
            skLineSegment(sketch, "E183.MirrorCS", {"start": v(68.58, 136.2) * mm, "end": v(68.58, 140.82) * mm});
            skLineSegment(sketch, "E184.MirrorCS", {"start": v(49.53, 142.55) * mm, "end": v(49.53, 147.17) * mm});
            skLineSegment(sketch, "E185.MirrorCS", {"start": v(19.51, 121.77) * mm, "end": v(19.51, 117.15) * mm});
            skPoint(sketch, "E186.MirrorP", {"position": v(40.87, 96.37) * mm});
            skPoint(sketch, "E187.MirrorP", {"position": v(15.47, 138.51) * mm});
            skLineSegment(sketch, "E188.MirrorCS", {"start": v(57.61, 159.87) * mm, "end": v(57.61, 155.25) * mm});
            skLineSegment(sketch, "E189.MirrorCS", {"start": v(19.51, 109.07) * mm, "end": v(19.51, 104.45) * mm});
            skLineSegment(sketch, "E190.MirrorCS", {"start": v(49.53, 109.07) * mm, "end": v(44.91, 109.07) * mm});
            skLineSegment(sketch, "E191.MirrorCS", {"start": v(25.86, 136.2) * mm, "end": v(30.48, 136.2) * mm});
            skLineSegment(sketch, "E192.MirrorCS", {"start": v(83.01, 134.47) * mm, "end": v(83.01, 129.85) * mm});
            skLineSegment(sketch, "E193.MirrorCS", {"start": v(95.71, 134.47) * mm, "end": v(95.71, 129.85) * mm});
            skLineSegment(sketch, "E194.MirrorCS", {"start": v(44.91, 121.77) * mm, "end": v(44.91, 117.15) * mm});
            skPoint(sketch, "E195.MirrorP", {"position": v(78.97, 87.71) * mm});
            skPoint(sketch, "E196.MirrorP", {"position": v(91.67, 121.77) * mm});
            skLineSegment(sketch, "E197.MirrorCS", {"start": v(100.33, 121.77) * mm, "end": v(95.71, 121.77) * mm});
            skLineSegment(sketch, "E198.MirrorCS", {"start": v(6.81, 134.47) * mm, "end": v(11.43, 134.47) * mm});
            skLineSegment(sketch, "E199.MirrorCS", {"start": v(74.93, 134.47) * mm, "end": v(70.31, 134.47) * mm});
            skLineSegment(sketch, "E200.MirrorCS", {"start": v(100.33, 109.07) * mm, "end": v(95.71, 109.07) * mm});
            skLineSegment(sketch, "E201.MirrorCS", {"start": v(44.91, 109.07) * mm, "end": v(44.91, 104.45) * mm});
            skLineSegment(sketch, "E202.MirrorCS", {"start": v(100.33, 96.37) * mm, "end": v(95.71, 96.37) * mm});
            skPoint(sketch, "E203.MirrorP", {"position": v(53.57, 100.41) * mm});
            skPoint(sketch, "E204.MirrorP", {"position": v(53.57, 87.71) * mm});
            skPoint(sketch, "E205.MirrorP", {"position": v(91.67, 125.81) * mm});
            skLineSegment(sketch, "E206.MirrorCS", {"start": v(24.13, 147.17) * mm, "end": v(19.51, 147.17) * mm});
            skLineSegment(sketch, "E207.MirrorCS", {"start": v(93.98, 136.2) * mm, "end": v(93.98, 140.82) * mm});
            skLineSegment(sketch, "E208.MirrorCS", {"start": v(32.21, 134.47) * mm, "end": v(36.83, 134.47) * mm});
            skLineSegment(sketch, "E209.MirrorCS", {"start": v(17.78, 123.5) * mm, "end": v(17.78, 128.12) * mm});
            skLineSegment(sketch, "E210.MirrorCS", {"start": v(49.53, 134.47) * mm, "end": v(44.91, 134.47) * mm});
            skLineSegment(sketch, "E211.MirrorCS", {"start": v(25.86, 110.8) * mm, "end": v(30.48, 110.8) * mm});
            skLineSegment(sketch, "E212.MirrorCS", {"start": v(17.78, 98.1) * mm, "end": v(17.78, 102.72) * mm});
            skLineSegment(sketch, "E213.MirrorCS", {"start": v(49.53, 147.17) * mm, "end": v(44.91, 147.17) * mm});
            skLineSegment(sketch, "E214.MirrorCS", {"start": v(100.33, 117.15) * mm, "end": v(100.33, 121.77) * mm});
            skLineSegment(sketch, "E215.MirrorCS", {"start": v(70.31, 134.47) * mm, "end": v(70.31, 129.85) * mm});
            skPoint(sketch, "E216.MirrorP", {"position": v(40.87, 129.85) * mm});
            skPoint(sketch, "E217.MirrorP", {"position": v(66.27, 96.37) * mm});
            skPoint(sketch, "E218.MirrorP", {"position": v(15.47, 125.81) * mm});
            skLineSegment(sketch, "E219.MirrorCS", {"start": v(100.33, 104.45) * mm, "end": v(100.33, 109.07) * mm});
            skPoint(sketch, "E220.MirrorP", {"position": v(40.87, 138.51) * mm});
            skPoint(sketch, "E221.MirrorP", {"position": v(40.87, 155.25) * mm});
            skLineSegment(sketch, "E222.MirrorCS", {"start": v(25.86, 98.1) * mm, "end": v(30.48, 98.1) * mm});
            skLineSegment(sketch, "E223.MirrorCS", {"start": v(100.33, 91.75) * mm, "end": v(100.33, 96.37) * mm});
            skLineSegment(sketch, "E224.MirrorCS", {"start": v(32.21, 109.07) * mm, "end": v(36.83, 109.07) * mm});
            skPoint(sketch, "E225.MirrorP", {"position": v(78.97, 151.21) * mm});
            skPoint(sketch, "E226.MirrorP", {"position": v(66.27, 134.47) * mm});
            skPoint(sketch, "E227.MirrorP", {"position": v(40.87, 104.45) * mm});
            skPoint(sketch, "E228.MirrorP", {"position": v(66.27, 109.07) * mm});
            skPoint(sketch, "E229.MirrorP", {"position": v(91.67, 138.51) * mm});
            skPoint(sketch, "E230.MirrorP", {"position": v(91.67, 134.47) * mm});
            skPoint(sketch, "E231.MirrorP", {"position": v(53.57, 113.11) * mm});
            skLineSegment(sketch, "E232.MirrorCS", {"start": v(83.01, 159.87) * mm, "end": v(83.01, 155.25) * mm});
            skLineSegment(sketch, "E233.MirrorCS", {"start": v(100.33, 167.95) * mm, "end": v(100.33, 172.57) * mm});
            skPoint(sketch, "E234.MirrorP", {"position": v(40.87, 159.87) * mm});
            skPoint(sketch, "E235.MirrorP", {"position": v(40.87, 125.81) * mm});
            skPoint(sketch, "E236.MirrorP", {"position": v(40.87, 113.11) * mm});
            skLineSegment(sketch, "E237.MirrorCS", {"start": v(49.53, 129.85) * mm, "end": v(49.53, 134.47) * mm});
            skLineSegment(sketch, "E238.MirrorCS", {"start": v(93.98, 110.8) * mm, "end": v(93.98, 115.42) * mm});
            skLineSegment(sketch, "E239.MirrorCS", {"start": v(36.83, 121.77) * mm, "end": v(36.83, 117.15) * mm});
            skLineSegment(sketch, "E240.MirrorCS", {"start": v(36.83, 109.07) * mm, "end": v(36.83, 104.45) * mm});
            skLineSegment(sketch, "E241.MirrorCS", {"start": v(76.66, 115.42) * mm, "end": v(81.28, 115.42) * mm});
            skLineSegment(sketch, "E242.MirrorCS", {"start": v(76.66, 102.72) * mm, "end": v(81.28, 102.72) * mm});
            skLineSegment(sketch, "E243.MirrorCS", {"start": v(93.98, 98.1) * mm, "end": v(93.98, 102.72) * mm});
            skLineSegment(sketch, "E244.MirrorCS", {"start": v(36.83, 96.37) * mm, "end": v(36.83, 91.75) * mm});
            skPoint(sketch, "E245.MirrorP", {"position": v(91.67, 129.85) * mm});
            skPoint(sketch, "E246.MirrorP", {"position": v(66.27, 117.15) * mm});
            skPoint(sketch, "E247.MirrorP", {"position": v(66.27, 121.77) * mm});
            skPoint(sketch, "E248.MirrorP", {"position": v(66.27, 104.45) * mm});
            skLineSegment(sketch, "E249.MirrorCS", {"start": v(63.96, 161.6) * mm, "end": v(63.96, 166.22) * mm});
            skLineSegment(sketch, "E250.MirrorCS", {"start": v(32.21, 159.87) * mm, "end": v(36.83, 159.87) * mm});
            skLineSegment(sketch, "E251.MirrorCS", {"start": v(83.01, 159.87) * mm, "end": v(87.63, 159.87) * mm});
            skLineSegment(sketch, "E252.MirrorCS", {"start": v(57.61, 147.17) * mm, "end": v(62.23, 147.17) * mm});
            skLineSegment(sketch, "E253.MirrorCS", {"start": v(100.33, 147.17) * mm, "end": v(95.71, 147.17) * mm});
            skPoint(sketch, "E254.MirrorP", {"position": v(40.87, 167.95) * mm});
            skLineSegment(sketch, "E255.MirrorCS", {"start": v(49.53, 96.37) * mm, "end": v(44.91, 96.37) * mm});
            skLineSegment(sketch, "E256.MirrorCS", {"start": v(74.93, 142.55) * mm, "end": v(74.93, 147.17) * mm});
            skPoint(sketch, "E257.MirrorP", {"position": v(66.27, 163.91) * mm});
            skLineSegment(sketch, "E258.MirrorCS", {"start": v(6.81, 121.77) * mm, "end": v(6.81, 117.15) * mm});
            skLineSegment(sketch, "E259.MirrorCS", {"start": v(6.81, 109.07) * mm, "end": v(6.81, 104.45) * mm});
            skLineSegment(sketch, "E260.MirrorCS", {"start": v(6.81, 109.07) * mm, "end": v(11.43, 109.07) * mm});
            skLineSegment(sketch, "E261.MirrorCS", {"start": v(13.16, 98.1) * mm, "end": v(13.16, 102.72) * mm});
            skPoint(sketch, "E262.MirrorP", {"position": v(53.57, 125.81) * mm});
            skLineSegment(sketch, "E263.MirrorCS", {"start": v(6.81, 96.37) * mm, "end": v(6.81, 91.75) * mm});
            skLineSegment(sketch, "E264.MirrorCS", {"start": v(19.51, 96.37) * mm, "end": v(19.51, 91.75) * mm});
            skLineSegment(sketch, "E265.MirrorCS", {"start": v(13.16, 85.4) * mm, "end": v(13.16, 90.02) * mm});
            skLineSegment(sketch, "E266.MirrorCS", {"start": v(83.01, 96.37) * mm, "end": v(83.01, 91.75) * mm});
            skPoint(sketch, "E267.MirrorP", {"position": v(66.27, 129.85) * mm});
            skPoint(sketch, "E268.MirrorP", {"position": v(78.97, 138.51) * mm});
            skPoint(sketch, "E269.MirrorP", {"position": v(15.47, 91.75) * mm});
            skPoint(sketch, "E270.MirrorP", {"position": v(15.47, 104.45) * mm});
            skLineSegment(sketch, "E271.MirrorCS", {"start": v(68.58, 148.9) * mm, "end": v(68.58, 153.52) * mm});
            skLineSegment(sketch, "E272.MirrorCS", {"start": v(25.86, 148.9) * mm, "end": v(25.86, 153.52) * mm});
            skLineSegment(sketch, "E273.MirrorCS", {"start": v(70.31, 159.87) * mm, "end": v(70.31, 155.25) * mm});
            skLineSegment(sketch, "E274.MirrorCS", {"start": v(89.36, 161.6) * mm, "end": v(89.36, 166.22) * mm});
            skLineSegment(sketch, "E275.MirrorCS", {"start": v(51.26, 136.2) * mm, "end": v(55.88, 136.2) * mm});
            skLineSegment(sketch, "E276.MirrorCS", {"start": v(100.33, 142.55) * mm, "end": v(100.33, 147.17) * mm});
            skLineSegment(sketch, "E277.MirrorCS", {"start": v(51.26, 136.2) * mm, "end": v(51.26, 140.82) * mm});
            skLineSegment(sketch, "E278.MirrorCS", {"start": v(89.36, 148.9) * mm, "end": v(89.36, 153.52) * mm});
            skLineSegment(sketch, "E279.MirrorCS", {"start": v(44.91, 134.47) * mm, "end": v(44.91, 129.85) * mm});
            skLineSegment(sketch, "E280.MirrorCS", {"start": v(74.93, 129.85) * mm, "end": v(74.93, 134.47) * mm});
            skPoint(sketch, "E281.MirrorP", {"position": v(66.27, 87.71) * mm});
            skLineSegment(sketch, "E282.MirrorCS", {"start": v(25.86, 123.5) * mm, "end": v(25.86, 128.12) * mm});
            skLineSegment(sketch, "E283.MirrorCS", {"start": v(13.16, 136.2) * mm, "end": v(13.16, 140.82) * mm});
            skPoint(sketch, "E284.MirrorP", {"position": v(78.97, 163.91) * mm});
            skLineSegment(sketch, "E285.MirrorCS", {"start": v(13.16, 110.8) * mm, "end": v(13.16, 115.42) * mm});
            skLineSegment(sketch, "E286.MirrorCS", {"start": v(38.56, 98.1) * mm, "end": v(38.56, 102.72) * mm});
            skLineSegment(sketch, "E287.MirrorCS", {"start": v(13.16, 123.5) * mm, "end": v(13.16, 128.12) * mm});
            skLineSegment(sketch, "E288.MirrorCS", {"start": v(62.23, 109.07) * mm, "end": v(62.23, 104.45) * mm});
            skLineSegment(sketch, "E289.MirrorCS", {"start": v(57.61, 121.77) * mm, "end": v(62.23, 121.77) * mm});
            skLineSegment(sketch, "E290.MirrorCS", {"start": v(63.96, 136.2) * mm, "end": v(63.96, 140.82) * mm});
            skLineSegment(sketch, "E291.MirrorCS", {"start": v(68.58, 110.8) * mm, "end": v(68.58, 115.42) * mm});
            skLineSegment(sketch, "E292.MirrorCS", {"start": v(49.53, 167.95) * mm, "end": v(49.53, 172.57) * mm});
            skLineSegment(sketch, "E293.MirrorCS", {"start": v(68.58, 98.1) * mm, "end": v(68.58, 102.72) * mm});
            skPoint(sketch, "E294.MirrorP", {"position": v(91.67, 87.71) * mm});
            skLineSegment(sketch, "E295.MirrorCS", {"start": v(25.86, 140.82) * mm, "end": v(30.48, 140.82) * mm});
            skLineSegment(sketch, "E296.MirrorCS", {"start": v(51.26, 110.8) * mm, "end": v(55.88, 110.8) * mm});
            skLineSegment(sketch, "E297.MirrorCS", {"start": v(51.26, 98.1) * mm, "end": v(51.26, 102.72) * mm});
            skPoint(sketch, "E298.MirrorP", {"position": v(66.27, 138.51) * mm});
            skLineSegment(sketch, "E299.MirrorCS", {"start": v(98.02, 175.42) * mm, "end": v(40.87, 175.42) * mm});
            skLineSegment(sketch, "E300.MirrorCS", {"start": v(68.58, 85.4) * mm, "end": v(68.58, 90.02) * mm});
            skLineSegment(sketch, "E301.MirrorCS", {"start": v(51.26, 85.4) * mm, "end": v(51.26, 90.02) * mm});
            skLineSegment(sketch, "E302.MirrorCS", {"start": v(62.23, 96.37) * mm, "end": v(62.23, 91.75) * mm});
            skPoint(sketch, "E303.MirrorP", {"position": v(91.67, 91.75) * mm});
            skPoint(sketch, "E304.MirrorP", {"position": v(15.47, 129.85) * mm});
            skPoint(sketch, "E305.MirrorP", {"position": v(15.47, 117.15) * mm});
            skLineSegment(sketch, "E306.MirrorCS", {"start": v(30.48, 123.5) * mm, "end": v(30.48, 128.12) * mm});
            skPoint(sketch, "E307.MirrorP", {"position": v(40.87, 87.71) * mm});
            skLineSegment(sketch, "E308.MirrorCS", {"start": v(81.28, 161.6) * mm, "end": v(81.28, 166.22) * mm});
            skLineSegment(sketch, "E309.MirrorCS", {"start": v(57.61, 159.87) * mm, "end": v(62.23, 159.87) * mm});
            skLineSegment(sketch, "E310.MirrorCS", {"start": v(32.21, 147.17) * mm, "end": v(36.83, 147.17) * mm});
            skLineSegment(sketch, "E311.MirrorCS", {"start": v(44.91, 159.87) * mm, "end": v(44.91, 155.25) * mm});
            skLineSegment(sketch, "E312.MirrorCS", {"start": v(95.71, 159.87) * mm, "end": v(95.71, 155.25) * mm});
            skLineSegment(sketch, "E313.MirrorCS", {"start": v(70.31, 147.17) * mm, "end": v(70.31, 142.55) * mm});
            skLineSegment(sketch, "E314.MirrorCS", {"start": v(76.66, 136.2) * mm, "end": v(81.28, 136.2) * mm});
            skLineSegment(sketch, "E315.MirrorCS", {"start": v(76.66, 136.2) * mm, "end": v(76.66, 140.82) * mm});
            skPoint(sketch, "E316.MirrorP", {"position": v(40.87, 151.21) * mm});
            skLineSegment(sketch, "E317.MirrorCS", {"start": v(36.83, 147.17) * mm, "end": v(36.83, 142.55) * mm});
            skLineSegment(sketch, "E318.MirrorCS", {"start": v(57.61, 172.57) * mm, "end": v(57.61, 167.95) * mm});
            skLineSegment(sketch, "E319.MirrorCS", {"start": v(51.26, 148.9) * mm, "end": v(51.26, 153.52) * mm});
            skLineSegment(sketch, "E320.MirrorCS", {"start": v(51.26, 123.5) * mm, "end": v(51.26, 128.12) * mm});
            skLineSegment(sketch, "E321.MirrorCS", {"start": v(36.83, 134.47) * mm, "end": v(36.83, 129.85) * mm});
            skLineSegment(sketch, "E322.MirrorCS", {"start": v(25.86, 153.52) * mm, "end": v(30.48, 153.52) * mm});
            skLineSegment(sketch, "E323.MirrorCS", {"start": v(25.86, 123.5) * mm, "end": v(30.48, 123.5) * mm});
            skLineSegment(sketch, "E324.MirrorCS", {"start": v(11.43, 134.47) * mm, "end": v(11.43, 129.85) * mm});
            skLineSegment(sketch, "E325.MirrorCS", {"start": v(51.26, 110.8) * mm, "end": v(51.26, 115.42) * mm});
            skLineSegment(sketch, "E326.MirrorCS", {"start": v(62.23, 121.77) * mm, "end": v(62.23, 117.15) * mm});
            skLineSegment(sketch, "E327.MirrorCS", {"start": v(76.66, 128.12) * mm, "end": v(81.28, 128.12) * mm});
            skPoint(sketch, "E328.MirrorP", {"position": v(91.67, 167.95) * mm});
            skLineSegment(sketch, "E329.MirrorCS", {"start": v(44.91, 172.57) * mm, "end": v(44.91, 167.95) * mm});
            skPoint(sketch, "E330.MirrorP", {"position": v(66.27, 167.95) * mm});
            skLineSegment(sketch, "E331.MirrorCS", {"start": v(57.61, 121.77) * mm, "end": v(57.61, 117.15) * mm});
            skLineSegment(sketch, "E332.MirrorCS", {"start": v(57.61, 172.57) * mm, "end": v(62.23, 172.57) * mm});
            skLineSegment(sketch, "E333.MirrorCS", {"start": v(24.13, 109.07) * mm, "end": v(19.51, 109.07) * mm});
            skLineSegment(sketch, "E334.MirrorCS", {"start": v(76.66, 98.1) * mm, "end": v(76.66, 102.72) * mm});
            skLineSegment(sketch, "E335.MirrorCS", {"start": v(76.66, 85.4) * mm, "end": v(76.66, 90.02) * mm});
            skLineSegment(sketch, "E336.MirrorCS", {"start": v(32.21, 96.37) * mm, "end": v(32.21, 91.75) * mm});
            skLineSegment(sketch, "E337.MirrorCS", {"start": v(24.13, 96.37) * mm, "end": v(19.51, 96.37) * mm});
            skLineSegment(sketch, "E338.MirrorCS", {"start": v(40.87, 175.42) * mm, "end": v(-3.37, 130.56) * mm});
            skPoint(sketch, "E339.MirrorP", {"position": v(15.47, 87.71) * mm});
            skLineSegment(sketch, "E340.MirrorCS", {"start": v(62.23, 172.57) * mm, "end": v(62.23, 167.95) * mm});
            skLineSegment(sketch, "E341.MirrorCS", {"start": v(51.26, 148.9) * mm, "end": v(55.88, 148.9) * mm});
            skLineSegment(sketch, "E342.MirrorCS", {"start": v(25.86, 148.9) * mm, "end": v(30.48, 148.9) * mm});
            skLineSegment(sketch, "E343.MirrorCS", {"start": v(87.63, 172.57) * mm, "end": v(87.63, 167.95) * mm});
            skLineSegment(sketch, "E344.MirrorCS", {"start": v(19.51, 147.17) * mm, "end": v(19.51, 142.55) * mm});
            skLineSegment(sketch, "E345.MirrorCS", {"start": v(38.56, 136.2) * mm, "end": v(38.56, 140.82) * mm});
            skLineSegment(sketch, "E346.MirrorCS", {"start": v(49.53, 159.87) * mm, "end": v(44.91, 159.87) * mm});
            skLineSegment(sketch, "E347.MirrorCS", {"start": v(62.23, 147.17) * mm, "end": v(62.23, 142.55) * mm});
            skLineSegment(sketch, "E348.MirrorCS", {"start": v(93.98, 123.5) * mm, "end": v(93.98, 128.12) * mm});
            skLineSegment(sketch, "E349.MirrorCS", {"start": v(57.61, 134.47) * mm, "end": v(57.61, 129.85) * mm});
            skLineSegment(sketch, "E350.MirrorCS", {"start": v(100.33, 134.47) * mm, "end": v(95.71, 134.47) * mm});
            skLineSegment(sketch, "E351.MirrorCS", {"start": v(17.78, 140.82) * mm, "end": v(13.16, 140.82) * mm});
            skLineSegment(sketch, "E352.MirrorCS", {"start": v(32.21, 121.77) * mm, "end": v(32.21, 117.15) * mm});
            skLineSegment(sketch, "E353.MirrorCS", {"start": v(76.66, 110.8) * mm, "end": v(76.66, 115.42) * mm});
            skLineSegment(sketch, "E354.MirrorCS", {"start": v(32.21, 109.07) * mm, "end": v(32.21, 104.45) * mm});
            skLineSegment(sketch, "E355.MirrorCS", {"start": v(63.96, 148.9) * mm, "end": v(63.96, 153.52) * mm});
            skLineSegment(sketch, "E356.MirrorCS", {"start": v(24.13, 121.77) * mm, "end": v(19.51, 121.77) * mm});
            skPoint(sketch, "E357.MirrorP", {"position": v(78.97, 100.41) * mm});
            skLineSegment(sketch, "E358.MirrorCS", {"start": v(89.36, 123.5) * mm, "end": v(89.36, 128.12) * mm});
            skLineSegment(sketch, "E359.MirrorCS", {"start": v(17.78, 136.2) * mm, "end": v(17.78, 140.82) * mm});
            skLineSegment(sketch, "E360.MirrorCS", {"start": v(49.53, 117.15) * mm, "end": v(49.53, 121.77) * mm});
            skLineSegment(sketch, "E361.MirrorCS", {"start": v(95.71, 121.77) * mm, "end": v(95.71, 117.15) * mm});
            skPoint(sketch, "E362.MirrorP", {"position": v(66.27, 159.87) * mm});
            skPoint(sketch, "E363.MirrorP", {"position": v(53.57, 138.51) * mm});
            skLineSegment(sketch, "E364.MirrorCS", {"start": v(51.26, 123.5) * mm, "end": v(55.88, 123.5) * mm});
            skLineSegment(sketch, "E365.MirrorCS", {"start": v(63.96, 123.5) * mm, "end": v(63.96, 128.12) * mm});
            skLineSegment(sketch, "E366.MirrorCS", {"start": v(76.66, 161.6) * mm, "end": v(76.66, 166.22) * mm});
            skLineSegment(sketch, "E367.MirrorCS", {"start": v(38.56, 85.4) * mm, "end": v(38.56, 90.02) * mm});
            skLineSegment(sketch, "E368.MirrorCS", {"start": v(81.28, 110.8) * mm, "end": v(81.28, 115.42) * mm});
            skLineSegment(sketch, "E369.MirrorCS", {"start": v(89.36, 85.4) * mm, "end": v(89.36, 90.02) * mm});
            skLineSegment(sketch, "E370.MirrorCS", {"start": v(57.61, 96.37) * mm, "end": v(62.23, 96.37) * mm});
            skLineSegment(sketch, "E371.MirrorCS", {"start": v(-3.37, 130.56) * mm, "end": v(-3.37, 125.8) * mm});
            skLineSegment(sketch, "E372.MirrorCS", {"start": v(76.66, 148.9) * mm, "end": v(81.28, 148.9) * mm});
            skLineSegment(sketch, "E373.MirrorCS", {"start": v(49.53, 155.25) * mm, "end": v(49.53, 159.87) * mm});
            skLineSegment(sketch, "E374.MirrorCS", {"start": v(93.98, 148.9) * mm, "end": v(93.98, 153.52) * mm});
            skLineSegment(sketch, "E375.MirrorCS", {"start": v(74.93, 172.57) * mm, "end": v(70.31, 172.57) * mm});
            skLineSegment(sketch, "E376.MirrorCS", {"start": v(30.48, 136.2) * mm, "end": v(30.48, 140.82) * mm});
            skLineSegment(sketch, "E377.MirrorCS", {"start": v(32.21, 147.17) * mm, "end": v(32.21, 142.55) * mm});
            skLineSegment(sketch, "E378.MirrorCS", {"start": v(51.26, 153.52) * mm, "end": v(55.88, 153.52) * mm});
            skLineSegment(sketch, "E379.MirrorCS", {"start": v(74.93, 167.95) * mm, "end": v(74.93, 172.57) * mm});
            skLineSegment(sketch, "E380.MirrorCS", {"start": v(68.58, 123.5) * mm, "end": v(68.58, 128.12) * mm});
            skLineSegment(sketch, "E381.MirrorCS", {"start": v(100.33, 129.85) * mm, "end": v(100.33, 134.47) * mm});
            skLineSegment(sketch, "E382.MirrorCS", {"start": v(89.36, 110.8) * mm, "end": v(89.36, 115.42) * mm});
            skLineSegment(sketch, "E383.MirrorCS", {"start": v(38.56, 110.8) * mm, "end": v(38.56, 115.42) * mm});
            skLineSegment(sketch, "E384.MirrorCS", {"start": v(89.36, 98.1) * mm, "end": v(89.36, 102.72) * mm});
            skLineSegment(sketch, "E385.MirrorCS", {"start": v(57.61, 109.07) * mm, "end": v(62.23, 109.07) * mm});
            skPoint(sketch, "E386.MirrorP", {"position": v(91.67, 163.91) * mm});
            skLineSegment(sketch, "E387.MirrorCS", {"start": v(30.48, 85.4) * mm, "end": v(30.48, 90.02) * mm});
            skLineSegment(sketch, "E388.MirrorCS", {"start": v(87.63, 96.37) * mm, "end": v(87.63, 91.75) * mm});
            skLineSegment(sketch, "E389.MirrorCS", {"start": v(74.93, 155.25) * mm, "end": v(74.93, 159.87) * mm});
            skLineSegment(sketch, "E390.MirrorCS", {"start": v(51.26, 161.6) * mm, "end": v(55.88, 161.6) * mm});
            skLineSegment(sketch, "E391.MirrorCS", {"start": v(43.18, 110.8) * mm, "end": v(43.18, 115.42) * mm});
            skLineSegment(sketch, "E392.MirrorCS", {"start": v(83.01, 172.57) * mm, "end": v(83.01, 167.95) * mm});
            skLineSegment(sketch, "E393.MirrorCS", {"start": v(89.36, 136.2) * mm, "end": v(89.36, 140.82) * mm});
            skPoint(sketch, "E394.MirrorP", {"position": v(91.67, 147.17) * mm});
            skLineSegment(sketch, "E395.MirrorCS", {"start": v(24.13, 134.47) * mm, "end": v(19.51, 134.47) * mm});
            skLineSegment(sketch, "E396.MirrorCS", {"start": v(25.86, 128.12) * mm, "end": v(30.48, 128.12) * mm});
            skLineSegment(sketch, "E397.MirrorCS", {"start": v(51.26, 140.82) * mm, "end": v(55.88, 140.82) * mm});
            skLineSegment(sketch, "E398.MirrorCS", {"start": v(87.63, 121.77) * mm, "end": v(87.63, 117.15) * mm});
            skLineSegment(sketch, "E399.MirrorCS", {"start": v(30.48, 110.8) * mm, "end": v(30.48, 115.42) * mm});
            skLineSegment(sketch, "E400.MirrorCS", {"start": v(24.13, 117.15) * mm, "end": v(24.13, 121.77) * mm});
            skLineSegment(sketch, "E401.MirrorCS", {"start": v(51.26, 161.6) * mm, "end": v(51.26, 166.22) * mm});
            skLineSegment(sketch, "E402.MirrorCS", {"start": v(87.63, 109.07) * mm, "end": v(87.63, 104.45) * mm});
            skLineSegment(sketch, "E403.MirrorCS", {"start": v(51.26, 115.42) * mm, "end": v(55.88, 115.42) * mm});
            skLineSegment(sketch, "E404.MirrorCS", {"start": v(24.13, 104.45) * mm, "end": v(24.13, 109.07) * mm});
            skLineSegment(sketch, "E405.MirrorCS", {"start": v(24.13, 91.75) * mm, "end": v(24.13, 96.37) * mm});
            skLineSegment(sketch, "E406.MirrorCS", {"start": v(30.48, 98.1) * mm, "end": v(30.48, 102.72) * mm});
            skPoint(sketch, "E407.MirrorP", {"position": v(40.87, 100.41) * mm});
            skLineSegment(sketch, "E408.MirrorCS", {"start": v(100.33, 159.87) * mm, "end": v(95.71, 159.87) * mm});
            skLineSegment(sketch, "E409.MirrorCS", {"start": v(87.63, 147.17) * mm, "end": v(87.63, 142.55) * mm});
            skLineSegment(sketch, "E410.MirrorCS", {"start": v(76.66, 153.52) * mm, "end": v(81.28, 153.52) * mm});
            skLineSegment(sketch, "E411.MirrorCS", {"start": v(76.66, 148.9) * mm, "end": v(76.66, 153.52) * mm});
            skPoint(sketch, "E412.MirrorP", {"position": v(66.27, 91.75) * mm});
            skLineSegment(sketch, "E413.MirrorCS", {"start": v(6.81, 134.47) * mm, "end": v(6.81, 129.85) * mm});
            skLineSegment(sketch, "E414.MirrorCS", {"start": v(74.93, 147.17) * mm, "end": v(70.31, 147.17) * mm});
            skLineSegment(sketch, "E415.MirrorCS", {"start": v(55.88, 136.2) * mm, "end": v(55.88, 140.82) * mm});
            skLineSegment(sketch, "E416.MirrorCS", {"start": v(57.61, 134.47) * mm, "end": v(62.23, 134.47) * mm});
            skLineSegment(sketch, "E417.MirrorCS", {"start": v(76.66, 123.5) * mm, "end": v(76.66, 128.12) * mm});
            skLineSegment(sketch, "E418.MirrorCS", {"start": v(32.21, 96.37) * mm, "end": v(36.83, 96.37) * mm});
            skLineSegment(sketch, "E419.MirrorCS", {"start": v(6.81, 96.37) * mm, "end": v(11.43, 96.37) * mm});
            skLineSegment(sketch, "E420.MirrorCS", {"start": v(49.53, 172.57) * mm, "end": v(44.91, 172.57) * mm});
            skLineSegment(sketch, "E421.MirrorCS", {"start": v(63.96, 110.8) * mm, "end": v(63.96, 115.42) * mm});
            skLineSegment(sketch, "E422.MirrorCS", {"start": v(63.96, 98.1) * mm, "end": v(63.96, 102.72) * mm});
            skLineSegment(sketch, "E423.MirrorCS", {"start": v(57.61, 109.07) * mm, "end": v(57.61, 104.45) * mm});
            skPoint(sketch, "E424.MirrorP", {"position": v(78.97, 113.11) * mm});
            skLineSegment(sketch, "E425.MirrorCS", {"start": v(63.96, 85.4) * mm, "end": v(63.96, 90.02) * mm});
            skLineSegment(sketch, "E426.MirrorCS", {"start": v(57.61, 96.37) * mm, "end": v(57.61, 91.75) * mm});
            skPoint(sketch, "E427.MirrorP", {"position": v(66.27, 147.17) * mm});
            skPoint(sketch, "E428.MirrorP", {"position": v(40.87, 142.55) * mm});
            skPoint(sketch, "E429.MirrorP", {"position": v(40.87, 121.77) * mm});
            skLineSegment(sketch, "E430.MirrorCS", {"start": v(87.63, 159.87) * mm, "end": v(87.63, 155.25) * mm});
            skLineSegment(sketch, "E431.MirrorCS", {"start": v(100.33, 155.25) * mm, "end": v(100.33, 159.87) * mm});
            skLineSegment(sketch, "E432.MirrorCS", {"start": v(76.66, 161.6) * mm, "end": v(81.28, 161.6) * mm});
            skLineSegment(sketch, "E433.MirrorCS", {"start": v(93.98, 161.6) * mm, "end": v(93.98, 166.22) * mm});
            skLineSegment(sketch, "E434.MirrorCS", {"start": v(38.56, 161.6) * mm, "end": v(38.56, 166.22) * mm});
            skLineSegment(sketch, "E435.MirrorCS", {"start": v(76.66, 166.22) * mm, "end": v(81.28, 166.22) * mm});
            skLineSegment(sketch, "E436.MirrorCS", {"start": v(25.86, 136.2) * mm, "end": v(25.86, 140.82) * mm});
            skPoint(sketch, "E437.MirrorP", {"position": v(15.47, 113.11) * mm});
            skLineSegment(sketch, "E438.MirrorCS", {"start": v(95.71, 147.17) * mm, "end": v(95.71, 142.55) * mm});
            skLineSegment(sketch, "E439.MirrorCS", {"start": v(57.61, 147.17) * mm, "end": v(57.61, 142.55) * mm});
            skLineSegment(sketch, "E440.MirrorCS", {"start": v(81.28, 123.5) * mm, "end": v(81.28, 128.12) * mm});
            skLineSegment(sketch, "E441.MirrorCS", {"start": v(38.56, 148.9) * mm, "end": v(38.56, 153.52) * mm});
            skLineSegment(sketch, "E442.MirrorCS", {"start": v(83.01, 134.47) * mm, "end": v(87.63, 134.47) * mm});
            skLineSegment(sketch, "E443.MirrorCS", {"start": v(76.66, 140.82) * mm, "end": v(81.28, 140.82) * mm});
            skLineSegment(sketch, "E444.MirrorCS", {"start": v(62.23, 134.47) * mm, "end": v(62.23, 129.85) * mm});
            skPoint(sketch, "E445.MirrorP", {"position": v(91.67, 117.15) * mm});
            skPoint(sketch, "E446.MirrorP", {"position": v(15.47, 100.41) * mm});
            skLineSegment(sketch, "E447.MirrorCS", {"start": v(74.93, 117.15) * mm, "end": v(74.93, 121.77) * mm});
            skPoint(sketch, "E448.MirrorP", {"position": v(66.27, 113.11) * mm});
            skPoint(sketch, "E449.MirrorP", {"position": v(91.67, 159.87) * mm});
            skPoint(sketch, "E450.MirrorP", {"position": v(91.67, 155.25) * mm});
            skLineSegment(sketch, "E451.MirrorCS", {"start": v(83.01, 121.77) * mm, "end": v(87.63, 121.77) * mm});
            skLineSegment(sketch, "E452.MirrorCS", {"start": v(83.01, 121.77) * mm, "end": v(83.01, 117.15) * mm});
            skLineSegment(sketch, "E453.MirrorCS", {"start": v(38.56, 123.5) * mm, "end": v(38.56, 128.12) * mm});
            skLineSegment(sketch, "E454.MirrorCS", {"start": v(55.88, 161.6) * mm, "end": v(55.88, 166.22) * mm});
            skLineSegment(sketch, "E455.MirrorCS", {"start": v(74.93, 109.07) * mm, "end": v(70.31, 109.07) * mm});
            skLineSegment(sketch, "E456.MirrorCS", {"start": v(55.88, 110.8) * mm, "end": v(55.88, 115.42) * mm});
            skLineSegment(sketch, "E457.MirrorCS", {"start": v(74.93, 104.45) * mm, "end": v(74.93, 109.07) * mm});
            skLineSegment(sketch, "E458.MirrorCS", {"start": v(6.81, 121.77) * mm, "end": v(11.43, 121.77) * mm});
            skLineSegment(sketch, "E459.MirrorCS", {"start": v(51.26, 98.1) * mm, "end": v(55.88, 98.1) * mm});
            skLineSegment(sketch, "E460.MirrorCS", {"start": v(55.88, 98.1) * mm, "end": v(55.88, 102.72) * mm});
            skLineSegment(sketch, "E461.MirrorCS", {"start": v(83.01, 109.07) * mm, "end": v(87.63, 109.07) * mm});
            skLineSegment(sketch, "E462.MirrorCS", {"start": v(74.93, 121.77) * mm, "end": v(70.31, 121.77) * mm});
            skLineSegment(sketch, "E463.MirrorCS", {"start": v(83.01, 96.37) * mm, "end": v(87.63, 96.37) * mm});
            skLineSegment(sketch, "E464.MirrorCS", {"start": v(83.01, 109.07) * mm, "end": v(83.01, 104.45) * mm});
            skPoint(sketch, "E465.MirrorP", {"position": v(66.27, 100.41) * mm});
            skPoint(sketch, "E466.MirrorP", {"position": v(40.87, 117.15) * mm});
            skLineSegment(sketch, "E467.MirrorCS", {"start": v(55.88, 85.4) * mm, "end": v(55.88, 90.02) * mm});
            skPoint(sketch, "E468.MirrorP", {"position": v(91.67, 104.45) * mm});
            skLineSegment(sketch, "E469.MirrorCS", {"start": v(36.83, 159.87) * mm, "end": v(36.83, 155.25) * mm});
            skLineSegment(sketch, "E470.MirrorCS", {"start": v(83.01, 172.57) * mm, "end": v(87.63, 172.57) * mm});
            skLineSegment(sketch, "E471.MirrorCS", {"start": v(68.58, 161.6) * mm, "end": v(68.58, 166.22) * mm});
            skLineSegment(sketch, "E472.MirrorCS", {"start": v(43.18, 136.2) * mm, "end": v(43.18, 140.82) * mm});
            skPoint(sketch, "E473.MirrorP", {"position": v(40.87, 163.91) * mm});
            skLineSegment(sketch, "E474.MirrorCS", {"start": v(24.13, 142.55) * mm, "end": v(24.13, 147.17) * mm});
            skPoint(sketch, "E475.MirrorP", {"position": v(66.27, 151.21) * mm});
            skLineSegment(sketch, "E476.MirrorCS", {"start": v(11.43, 96.37) * mm, "end": v(11.43, 91.75) * mm});
            skLineSegment(sketch, "E477.MirrorCS", {"start": v(74.93, 159.87) * mm, "end": v(70.31, 159.87) * mm});
            skLineSegment(sketch, "E478.MirrorCS", {"start": v(44.91, 147.17) * mm, "end": v(44.91, 142.55) * mm});
            skLineSegment(sketch, "E479.MirrorCS", {"start": v(32.21, 134.47) * mm, "end": v(32.21, 129.85) * mm});
            skLineSegment(sketch, "E480.MirrorCS", {"start": v(30.48, 148.9) * mm, "end": v(30.48, 153.52) * mm});
            skLineSegment(sketch, "E481.MirrorCS", {"start": v(49.53, 104.45) * mm, "end": v(49.53, 109.07) * mm});
            skLineSegment(sketch, "E482.MirrorCS", {"start": v(81.28, 136.2) * mm, "end": v(81.28, 140.82) * mm});
            skLineSegment(sketch, "E483.MirrorCS", {"start": v(19.51, 134.47) * mm, "end": v(19.51, 129.85) * mm});
            skPoint(sketch, "E484.MirrorP", {"position": v(40.87, 147.17) * mm});
            skLineSegment(sketch, "E485.MirrorCS", {"start": v(70.31, 121.77) * mm, "end": v(70.31, 117.15) * mm});
            skPoint(sketch, "E486.MirrorP", {"position": v(40.87, 134.47) * mm});
            skLineSegment(sketch, "E487.MirrorCS", {"start": v(25.86, 110.8) * mm, "end": v(25.86, 115.42) * mm});
            skLineSegment(sketch, "E488.MirrorCS", {"start": v(11.43, 121.77) * mm, "end": v(11.43, 117.15) * mm});
            skLineSegment(sketch, "E489.MirrorCS", {"start": v(51.26, 166.22) * mm, "end": v(55.88, 166.22) * mm});
            skLineSegment(sketch, "E490.MirrorCS", {"start": v(51.26, 128.12) * mm, "end": v(55.88, 128.12) * mm});
            skLineSegment(sketch, "E491.MirrorCS", {"start": v(11.43, 109.07) * mm, "end": v(11.43, 104.45) * mm});
            skPoint(sketch, "E492.MirrorP", {"position": v(66.27, 125.81) * mm});
            skLineSegment(sketch, "E493.MirrorCS", {"start": v(49.53, 91.75) * mm, "end": v(49.53, 96.37) * mm});
            skLineSegment(sketch, "E494.MirrorCS", {"start": v(51.26, 102.72) * mm, "end": v(55.88, 102.72) * mm});
            skLineSegment(sketch, "E495.MirrorCS", {"start": v(25.86, 98.1) * mm, "end": v(25.86, 102.72) * mm});
            skPoint(sketch, "E496.MirrorP", {"position": v(15.47, 109.07) * mm});
            skLineSegment(sketch, "E497.MirrorCS", {"start": v(76.66, 110.8) * mm, "end": v(81.28, 110.8) * mm});
            skLineSegment(sketch, "E498.MirrorCS", {"start": v(25.86, 115.42) * mm, "end": v(30.48, 115.42) * mm});
            skLineSegment(sketch, "E499.MirrorCS", {"start": v(76.66, 98.1) * mm, "end": v(81.28, 98.1) * mm});
            skLineSegment(sketch, "E500.MirrorCS", {"start": v(43.18, 161.6) * mm, "end": v(43.18, 166.22) * mm});
            skLineSegment(sketch, "E501.MirrorCS", {"start": v(25.86, 102.72) * mm, "end": v(30.48, 102.72) * mm});
            skLineSegment(sketch, "E502.MirrorCS", {"start": v(70.31, 109.07) * mm, "end": v(70.31, 104.45) * mm});
            skPoint(sketch, "E503.MirrorP", {"position": v(66.27, 155.25) * mm});
            skPoint(sketch, "E504.MirrorP", {"position": v(78.97, 125.81) * mm});
            skLineSegment(sketch, "E505.MirrorCS", {"start": v(70.31, 96.37) * mm, "end": v(70.31, 91.75) * mm});
            skPoint(sketch, "E506.MirrorP", {"position": v(15.47, 96.37) * mm});
            skLineSegment(sketch, "E507.MirrorCS", {"start": v(62.23, 159.87) * mm, "end": v(62.23, 155.25) * mm});
            skLineSegment(sketch, "E508.MirrorCS", {"start": v(95.71, 172.57) * mm, "end": v(95.71, 167.95) * mm});
            skPoint(sketch, "E509.MirrorP", {"position": v(53.57, 163.91) * mm});
            skLineSegment(sketch, "E510.MirrorCS", {"start": v(98.02, 151.21) * mm, "end": v(98.02, 175.42) * mm});
            skLineSegment(sketch, "E511.MirrorCS", {"start": v(44.91, 96.37) * mm, "end": v(44.91, 91.75) * mm});
            skPoint(sketch, "E512.MirrorP", {"position": v(15.47, 134.47) * mm});
            skPoint(sketch, "E513.MirrorP", {"position": v(40.87, 109.07) * mm});
            skLineSegment(sketch, "E514.MirrorCS", {"start": v(43.18, 148.9) * mm, "end": v(43.18, 153.52) * mm});
            skLineSegment(sketch, "E515.MirrorCS", {"start": v(100.33, 172.57) * mm, "end": v(95.71, 172.57) * mm});
            skLineSegment(sketch, "E516.MirrorCS", {"start": v(74.93, 91.75) * mm, "end": v(74.93, 96.37) * mm});
            skLineSegment(sketch, "E517.MirrorCS", {"start": v(74.93, 96.37) * mm, "end": v(70.31, 96.37) * mm});
            skLineSegment(sketch, "E518.MirrorCS", {"start": v(127.46, 90.02) * mm, "end": v(132.08, 90.02) * mm});
            skLineSegment(sketch, "E519.MirrorCS", {"start": v(102.06, 90.02) * mm, "end": v(102.06, 85.4) * mm});
            skLineSegment(sketch, "E520.MirrorCS", {"start": v(102.06, 85.4) * mm, "end": v(106.68, 85.4) * mm});
            skLineSegment(sketch, "E521.MirrorCS", {"start": v(132.08, 90.02) * mm, "end": v(132.08, 85.4) * mm});
            skLineSegment(sketch, "E522.MirrorCS", {"start": v(127.46, 85.4) * mm, "end": v(132.08, 85.4) * mm});
            skLineSegment(sketch, "E523.MirrorCS", {"start": v(102.06, 90.02) * mm, "end": v(106.68, 90.02) * mm});
            skLineSegment(sketch, "E524.MirrorCS", {"start": v(144.78, 90.02) * mm, "end": v(144.78, 85.4) * mm});
            skLineSegment(sketch, "E525.MirrorCS", {"start": v(119.38, 90.02) * mm, "end": v(119.38, 85.4) * mm});
            skLineSegment(sketch, "E526.MirrorCS", {"start": v(119.38, 90.02) * mm, "end": v(114.76, 90.02) * mm});
            skLineSegment(sketch, "E527.MirrorCS", {"start": v(182.88, 85.4) * mm, "end": v(182.88, 90.02) * mm});
            skLineSegment(sketch, "E528.MirrorCS", {"start": v(152.86, 90.02) * mm, "end": v(152.86, 85.4) * mm});
            skLineSegment(sketch, "E529.MirrorCS", {"start": v(114.76, 90.02) * mm, "end": v(114.76, 85.4) * mm});
            skLineSegment(sketch, "E530.MirrorCS", {"start": v(127.46, 90.02) * mm, "end": v(127.46, 85.4) * mm});
            skLineSegment(sketch, "E531.MirrorCS", {"start": v(144.78, 85.4) * mm, "end": v(140.16, 85.4) * mm});
            skLineSegment(sketch, "E532.MirrorCS", {"start": v(140.16, 90.02) * mm, "end": v(140.16, 85.4) * mm});
            skLineSegment(sketch, "E533.MirrorCS", {"start": v(144.78, 90.02) * mm, "end": v(140.16, 90.02) * mm});
            skLineSegment(sketch, "E534.MirrorCS", {"start": v(106.68, 90.02) * mm, "end": v(106.68, 85.4) * mm});
            skLineSegment(sketch, "E535.MirrorCS", {"start": v(102.06, 85.4) * mm, "end": v(102.06, 90.02) * mm});
            skLineSegment(sketch, "E536.MirrorCS", {"start": v(119.38, 85.4) * mm, "end": v(114.76, 85.4) * mm});
            skLineSegment(sketch, "E537.MirrorCS", {"start": v(182.88, 90.02) * mm, "end": v(182.88, 85.4) * mm});
            skLineSegment(sketch, "E538.MirrorCS", {"start": v(113.03, 167.95) * mm, "end": v(110.72, 167.95) * mm});
            skLineSegment(sketch, "E539.MirrorCS", {"start": v(144.78, 85.4) * mm, "end": v(144.78, 90.02) * mm});
            skLineSegment(sketch, "E540.MirrorCS", {"start": v(140.16, 85.4) * mm, "end": v(140.16, 90.02) * mm});
            skLineSegment(sketch, "E541.MirrorCS", {"start": v(152.86, 85.4) * mm, "end": v(152.86, 90.02) * mm});
            skLineSegment(sketch, "E542.MirrorCS", {"start": v(127.46, 85.4) * mm, "end": v(127.46, 90.02) * mm});
            skLineSegment(sketch, "E543.MirrorCS", {"start": v(110.72, 142.55) * mm, "end": v(108.41, 142.55) * mm});
            skLineSegment(sketch, "E544.MirrorCS", {"start": v(119.38, 166.22) * mm, "end": v(114.76, 166.22) * mm});
            skLineSegment(sketch, "E545.MirrorCS", {"start": v(132.08, 85.4) * mm, "end": v(132.08, 90.02) * mm});
            skLineSegment(sketch, "E546.MirrorCS", {"start": v(138.43, 117.15) * mm, "end": v(136.12, 117.15) * mm});
            skLineSegment(sketch, "E547.MirrorCS", {"start": v(114.76, 85.4) * mm, "end": v(114.76, 90.02) * mm});
            skLineSegment(sketch, "E548.MirrorCS", {"start": v(123.42, 167.95) * mm, "end": v(121.11, 167.95) * mm});
            skLineSegment(sketch, "E549.MirrorCS", {"start": v(136.12, 117.15) * mm, "end": v(133.81, 117.15) * mm});
            skLineSegment(sketch, "E550.MirrorCS", {"start": v(125.73, 167.95) * mm, "end": v(123.42, 167.95) * mm});
            skLineSegment(sketch, "E551.MirrorCS", {"start": v(125.73, 155.25) * mm, "end": v(123.42, 155.25) * mm});
            skLineSegment(sketch, "E552.MirrorCS", {"start": v(136.12, 91.75) * mm, "end": v(133.81, 91.75) * mm});
            skLineSegment(sketch, "E553.MirrorCS", {"start": v(186.92, 58.27) * mm, "end": v(184.61, 58.27) * mm});
            skLineSegment(sketch, "E554.MirrorCS", {"start": v(123.42, 129.85) * mm, "end": v(121.11, 129.85) * mm});
            skLineSegment(sketch, "E555.MirrorCS", {"start": v(119.38, 85.4) * mm, "end": v(119.38, 90.02) * mm});
            skLineSegment(sketch, "E556.MirrorCS", {"start": v(106.68, 85.4) * mm, "end": v(106.68, 90.02) * mm});
            skLineSegment(sketch, "E557.MirrorCS", {"start": v(125.73, 129.85) * mm, "end": v(123.42, 129.85) * mm});
            skLineSegment(sketch, "E558.MirrorCS", {"start": v(113.03, 142.55) * mm, "end": v(110.72, 142.55) * mm});
            skLineSegment(sketch, "E559.MirrorCS", {"start": v(123.42, 155.25) * mm, "end": v(121.11, 155.25) * mm});
            skLineSegment(sketch, "E560.MirrorCS", {"start": v(176.53, 129.85) * mm, "end": v(174.22, 129.85) * mm});
            skLineSegment(sketch, "E561.MirrorCS", {"start": v(182.88, 77.32) * mm, "end": v(182.88, 72.7) * mm});
            skLineSegment(sketch, "E562.MirrorCS", {"start": v(113.03, 129.85) * mm, "end": v(110.72, 129.85) * mm});
            skLineSegment(sketch, "E563.MirrorCS", {"start": v(136.12, 58.27) * mm, "end": v(133.81, 58.27) * mm});
            skLineSegment(sketch, "E564.MirrorCS", {"start": v(110.72, 83.67) * mm, "end": v(108.41, 83.67) * mm});
            skLineSegment(sketch, "E565.MirrorCS", {"start": v(110.72, 70.97) * mm, "end": v(108.41, 70.97) * mm});
            skLineSegment(sketch, "E566.MirrorCS", {"start": v(163.83, 32.87) * mm, "end": v(161.52, 32.87) * mm});
            skLineSegment(sketch, "E567.MirrorCS", {"start": v(161.52, 142.55) * mm, "end": v(159.21, 142.55) * mm});
            skLineSegment(sketch, "E568.MirrorCS", {"start": v(138.43, 45.57) * mm, "end": v(136.12, 45.57) * mm});
            skLineSegment(sketch, "E569.MirrorCS", {"start": v(123.42, 142.55) * mm, "end": v(121.11, 142.55) * mm});
            skLineSegment(sketch, "E570.MirrorCS", {"start": v(148.82, 167.95) * mm, "end": v(146.51, 167.95) * mm});
            skLineSegment(sketch, "E571.MirrorCS", {"start": v(123.42, 91.75) * mm, "end": v(121.11, 91.75) * mm});
            skLineSegment(sketch, "E572.MirrorCS", {"start": v(138.43, 91.75) * mm, "end": v(136.12, 91.75) * mm});
            skLineSegment(sketch, "E573.MirrorCS", {"start": v(176.53, 45.57) * mm, "end": v(174.22, 45.57) * mm});
            skLineSegment(sketch, "E574.MirrorCS", {"start": v(136.12, 45.57) * mm, "end": v(133.81, 45.57) * mm});
            skLineSegment(sketch, "E575.MirrorCS", {"start": v(125.73, 91.75) * mm, "end": v(123.42, 91.75) * mm});
            skLineSegment(sketch, "E576.MirrorCS", {"start": v(151.13, 91.75) * mm, "end": v(148.82, 91.75) * mm});
            skLineSegment(sketch, "E577.MirrorCS", {"start": v(148.82, 155.25) * mm, "end": v(146.51, 155.25) * mm});
            skLineSegment(sketch, "E578.MirrorCS", {"start": v(113.03, 58.27) * mm, "end": v(110.72, 58.27) * mm});
            skLineSegment(sketch, "E579.MirrorCS", {"start": v(151.13, 83.67) * mm, "end": v(148.82, 83.67) * mm});
            skLineSegment(sketch, "E580.MirrorCS", {"start": v(100.33, 104.45) * mm, "end": v(98.02, 104.45) * mm});
            skLineSegment(sketch, "E581.MirrorCS", {"start": v(163.83, 142.55) * mm, "end": v(161.52, 142.55) * mm});
            skLineSegment(sketch, "E582.MirrorCS", {"start": v(136.12, 7.47) * mm, "end": v(133.81, 7.47) * mm});
            skLineSegment(sketch, "E583.MirrorCS", {"start": v(125.73, 7.47) * mm, "end": v(123.42, 7.47) * mm});
            skLineSegment(sketch, "E584.MirrorCS", {"start": v(136.12, 129.85) * mm, "end": v(133.81, 129.85) * mm});
            skLineSegment(sketch, "E585.MirrorCS", {"start": v(100.33, 121.77) * mm, "end": v(100.33, 117.15) * mm});
            skLineSegment(sketch, "E586.MirrorCS", {"start": v(189.23, 104.45) * mm, "end": v(186.92, 104.45) * mm});
            skLineSegment(sketch, "E587.MirrorCS", {"start": v(125.73, 117.15) * mm, "end": v(123.42, 117.15) * mm});
            skLineSegment(sketch, "E588.MirrorCS", {"start": v(102.06, 77.32) * mm, "end": v(106.68, 77.32) * mm});
            skLineSegment(sketch, "E589.MirrorCS", {"start": v(100.33, 58.27) * mm, "end": v(98.02, 58.27) * mm});
            skLineSegment(sketch, "E590.MirrorCS", {"start": v(161.52, 45.57) * mm, "end": v(159.21, 45.57) * mm});
            skLineSegment(sketch, "E591.MirrorCS", {"start": v(110.72, 32.87) * mm, "end": v(108.41, 32.87) * mm});
            skLineSegment(sketch, "E592.MirrorCS", {"start": v(151.13, 70.97) * mm, "end": v(148.82, 70.97) * mm});
            skLineSegment(sketch, "E593.MirrorCS", {"start": v(123.42, 20.17) * mm, "end": v(121.11, 20.17) * mm});
            skLineSegment(sketch, "E594.MirrorCS", {"start": v(127.46, 77.32) * mm, "end": v(127.46, 72.7) * mm});
            skLineSegment(sketch, "E595.MirrorCS", {"start": v(148.82, 70.97) * mm, "end": v(146.51, 70.97) * mm});
            skLineSegment(sketch, "E596.MirrorCS", {"start": v(151.13, 58.27) * mm, "end": v(148.82, 58.27) * mm});
            skLineSegment(sketch, "E597.MirrorCS", {"start": v(163.83, 45.57) * mm, "end": v(161.52, 45.57) * mm});
            skLineSegment(sketch, "E598.MirrorCS", {"start": v(123.42, 117.15) * mm, "end": v(121.11, 117.15) * mm});
            skLineSegment(sketch, "E599.MirrorCS", {"start": v(136.12, 167.95) * mm, "end": v(133.81, 167.95) * mm});
            skLineSegment(sketch, "E600.MirrorCS", {"start": v(163.83, 20.17) * mm, "end": v(161.52, 20.17) * mm});
            skLineSegment(sketch, "E601.MirrorCS", {"start": v(100.33, 40.94) * mm, "end": v(100.33, 45.57) * mm});
            skLineSegment(sketch, "E602.MirrorCS", {"start": v(127.46, 77.32) * mm, "end": v(132.08, 77.32) * mm});
            skLineSegment(sketch, "E603.MirrorCS", {"start": v(151.13, 104.45) * mm, "end": v(148.82, 104.45) * mm});
            skLineSegment(sketch, "E604.MirrorCS", {"start": v(138.43, 129.85) * mm, "end": v(136.12, 129.85) * mm});
            skLineSegment(sketch, "E605.MirrorCS", {"start": v(125.73, 83.67) * mm, "end": v(123.42, 83.67) * mm});
            skLineSegment(sketch, "E606.MirrorCS", {"start": v(189.23, 91.75) * mm, "end": v(186.92, 91.75) * mm});
            skLineSegment(sketch, "E607.MirrorCS", {"start": v(113.03, 155.25) * mm, "end": v(110.72, 155.25) * mm});
            skLineSegment(sketch, "E608.MirrorCS", {"start": v(113.03, 91.75) * mm, "end": v(110.72, 91.75) * mm});
            skLineSegment(sketch, "E609.MirrorCS", {"start": v(151.13, 45.57) * mm, "end": v(148.82, 45.57) * mm});
            skLineSegment(sketch, "E610.MirrorCS", {"start": v(125.73, 70.97) * mm, "end": v(123.42, 70.97) * mm});
            skLineSegment(sketch, "E611.MirrorCS", {"start": v(113.03, 32.87) * mm, "end": v(110.72, 32.87) * mm});
            skLineSegment(sketch, "E612.MirrorCS", {"start": v(125.73, 58.27) * mm, "end": v(123.42, 58.27) * mm});
            skLineSegment(sketch, "E613.MirrorCS", {"start": v(148.82, 58.27) * mm, "end": v(146.51, 58.27) * mm});
            skLineSegment(sketch, "E614.MirrorCS", {"start": v(138.43, 7.47) * mm, "end": v(136.12, 7.47) * mm});
            skLineSegment(sketch, "E615.MirrorCS", {"start": v(189.23, 40.94) * mm, "end": v(189.23, 45.57) * mm});
            skLineSegment(sketch, "E616.MirrorCS", {"start": v(110.72, 91.75) * mm, "end": v(108.41, 91.75) * mm});
            skLineSegment(sketch, "E617.MirrorCS", {"start": v(110.72, 129.85) * mm, "end": v(108.41, 129.85) * mm});
            skLineSegment(sketch, "E618.MirrorCS", {"start": v(148.82, 129.85) * mm, "end": v(146.51, 129.85) * mm});
            skLineSegment(sketch, "E619.MirrorCS", {"start": v(186.92, 129.85) * mm, "end": v(184.61, 129.85) * mm});
            skLineSegment(sketch, "E620.MirrorCS", {"start": v(100.33, 7.47) * mm, "end": v(98.02, 7.47) * mm});
            skLineSegment(sketch, "E621.MirrorCS", {"start": v(151.13, 109.07) * mm, "end": v(151.13, 104.45) * mm});
            skLineSegment(sketch, "E622.MirrorCS", {"start": v(138.43, 155.25) * mm, "end": v(136.12, 155.25) * mm});
            skLineSegment(sketch, "E623.MirrorCS", {"start": v(151.13, 117.15) * mm, "end": v(148.82, 117.15) * mm});
            skLineSegment(sketch, "E624.MirrorCS", {"start": v(138.43, 167.95) * mm, "end": v(136.12, 167.95) * mm});
            skLineSegment(sketch, "E625.MirrorCS", {"start": v(184.61, 121.77) * mm, "end": v(184.61, 117.15) * mm});
            skLineSegment(sketch, "E626.MirrorCS", {"start": v(100.33, 91.75) * mm, "end": v(98.02, 91.75) * mm});
            skLineSegment(sketch, "E627.MirrorCS", {"start": v(100.33, 155.25) * mm, "end": v(98.02, 155.25) * mm});
            skLineSegment(sketch, "E628.MirrorCS", {"start": v(161.52, 129.85) * mm, "end": v(159.21, 129.85) * mm});
            skLineSegment(sketch, "E629.MirrorCS", {"start": v(152.86, 77.32) * mm, "end": v(152.86, 72.7) * mm});
            skLineSegment(sketch, "E630.MirrorCS", {"start": v(125.73, 45.57) * mm, "end": v(123.42, 45.57) * mm});
            skLineSegment(sketch, "E631.MirrorCS", {"start": v(148.82, 32.87) * mm, "end": v(146.51, 32.87) * mm});
            skLineSegment(sketch, "E632.MirrorCS", {"start": v(152.86, 13.82) * mm, "end": v(152.86, 9.2) * mm});
            skLineSegment(sketch, "E633.MirrorCS", {"start": v(123.42, 104.45) * mm, "end": v(121.11, 104.45) * mm});
            skLineSegment(sketch, "E634.MirrorCS", {"start": v(100.33, 117.15) * mm, "end": v(98.02, 117.15) * mm});
            skLineSegment(sketch, "E635.MirrorCS", {"start": v(125.73, 142.55) * mm, "end": v(123.42, 142.55) * mm});
            skLineSegment(sketch, "E636.MirrorCS", {"start": v(151.13, 129.85) * mm, "end": v(148.82, 129.85) * mm});
            skLineSegment(sketch, "E637.MirrorCS", {"start": v(110.72, 104.45) * mm, "end": v(108.41, 104.45) * mm});
            skLineSegment(sketch, "E638.MirrorCS", {"start": v(110.72, 167.95) * mm, "end": v(108.41, 167.95) * mm});
            skLineSegment(sketch, "E639.MirrorCS", {"start": v(113.03, 104.45) * mm, "end": v(110.72, 104.45) * mm});
            skLineSegment(sketch, "E640.MirrorCS", {"start": v(189.23, 79.04) * mm, "end": v(184.61, 79.04) * mm});
            skLineSegment(sketch, "E641.MirrorCS", {"start": v(127.46, 9.2) * mm, "end": v(132.08, 9.2) * mm});
            skLineSegment(sketch, "E642.MirrorCS", {"start": v(98.02, 45.57) * mm, "end": v(95.71, 45.57) * mm});
            skLineSegment(sketch, "E643.MirrorCS", {"start": v(148.82, 91.75) * mm, "end": v(146.51, 91.75) * mm});
            skLineSegment(sketch, "E644.MirrorCS", {"start": v(161.52, 20.17) * mm, "end": v(159.21, 20.17) * mm});
            skLineSegment(sketch, "E645.MirrorCS", {"start": v(161.52, 32.87) * mm, "end": v(159.21, 32.87) * mm});
            skLineSegment(sketch, "E646.MirrorCS", {"start": v(186.92, 104.45) * mm, "end": v(184.61, 104.45) * mm});
            skLineSegment(sketch, "E647.MirrorCS", {"start": v(98.02, 117.15) * mm, "end": v(95.71, 117.15) * mm});
            skLineSegment(sketch, "E648.MirrorCS", {"start": v(163.83, 155.25) * mm, "end": v(161.52, 155.25) * mm});
            skLineSegment(sketch, "E649.MirrorCS", {"start": v(151.13, 167.95) * mm, "end": v(148.82, 167.95) * mm});
            skLineSegment(sketch, "E650.MirrorCS", {"start": v(98.02, 91.75) * mm, "end": v(95.71, 91.75) * mm});
            skLineSegment(sketch, "E651.MirrorCS", {"start": v(100.33, 167.95) * mm, "end": v(98.02, 167.95) * mm});
            skLineSegment(sketch, "E652.MirrorCS", {"start": v(136.12, 142.55) * mm, "end": v(133.81, 142.55) * mm});
            skLineSegment(sketch, "E653.MirrorCS", {"start": v(186.92, 83.67) * mm, "end": v(184.61, 83.67) * mm});
            skLineSegment(sketch, "E654.MirrorCS", {"start": v(132.08, 136.2) * mm, "end": v(132.08, 140.82) * mm});
            skLineSegment(sketch, "E655.MirrorCS", {"start": v(189.23, 45.57) * mm, "end": v(186.92, 45.57) * mm});
            skLineSegment(sketch, "E656.MirrorCS", {"start": v(110.72, 45.57) * mm, "end": v(108.41, 45.57) * mm});
            skLineSegment(sketch, "E657.MirrorCS", {"start": v(110.72, 58.27) * mm, "end": v(108.41, 58.27) * mm});
            skLineSegment(sketch, "E658.MirrorCS", {"start": v(186.92, 91.75) * mm, "end": v(184.61, 91.75) * mm});
            skLineSegment(sketch, "E659.MirrorCS", {"start": v(98.02, 129.85) * mm, "end": v(95.71, 129.85) * mm});
            skLineSegment(sketch, "E660.MirrorCS", {"start": v(98.02, 104.45) * mm, "end": v(95.71, 104.45) * mm});
            skLineSegment(sketch, "E661.MirrorCS", {"start": v(113.03, 70.97) * mm, "end": v(110.72, 70.97) * mm});
            skLineSegment(sketch, "E662.MirrorCS", {"start": v(159.21, 28.24) * mm, "end": v(159.21, 32.87) * mm});
            skLineSegment(sketch, "E663.MirrorCS", {"start": v(125.73, 20.17) * mm, "end": v(123.42, 20.17) * mm});
            skLineSegment(sketch, "E664.MirrorCS", {"start": v(151.13, 7.47) * mm, "end": v(148.82, 7.47) * mm});
            skLineSegment(sketch, "E665.MirrorCS", {"start": v(113.03, 83.67) * mm, "end": v(110.72, 83.67) * mm});
            skLineSegment(sketch, "E666.MirrorCS", {"start": v(152.86, 13.82) * mm, "end": v(157.48, 13.82) * mm});
            skLineSegment(sketch, "E667.MirrorCS", {"start": v(151.13, 20.17) * mm, "end": v(148.82, 20.17) * mm});
            skLineSegment(sketch, "E668.MirrorCS", {"start": v(189.23, 129.85) * mm, "end": v(186.92, 129.85) * mm});
            skLineSegment(sketch, "E669.MirrorCS", {"start": v(151.13, 142.55) * mm, "end": v(148.82, 142.55) * mm});
            skLineSegment(sketch, "E670.MirrorCS", {"start": v(151.13, 155.25) * mm, "end": v(148.82, 155.25) * mm});
            skLineSegment(sketch, "E671.MirrorCS", {"start": v(102.06, 9.2) * mm, "end": v(106.68, 9.2) * mm});
            skLineSegment(sketch, "E672.MirrorCS", {"start": v(151.13, 121.77) * mm, "end": v(151.13, 117.15) * mm});
            skLineSegment(sketch, "E673.MirrorCS", {"start": v(98.02, 58.27) * mm, "end": v(95.71, 58.27) * mm});
            skLineSegment(sketch, "E674.MirrorCS", {"start": v(186.92, 45.57) * mm, "end": v(184.61, 45.57) * mm});
            skLineSegment(sketch, "E675.MirrorCS", {"start": v(123.42, 45.57) * mm, "end": v(121.11, 45.57) * mm});
            skLineSegment(sketch, "E676.MirrorCS", {"start": v(113.03, 45.57) * mm, "end": v(110.72, 45.57) * mm});
            skLineSegment(sketch, "E677.MirrorCS", {"start": v(100.33, 45.57) * mm, "end": v(98.02, 45.57) * mm});
            skLineSegment(sketch, "E678.MirrorCS", {"start": v(163.83, 129.85) * mm, "end": v(161.52, 129.85) * mm});
            skLineSegment(sketch, "E679.MirrorCS", {"start": v(136.12, 155.25) * mm, "end": v(133.81, 155.25) * mm});
            skLineSegment(sketch, "E680.MirrorCS", {"start": v(132.08, 77.32) * mm, "end": v(132.08, 72.7) * mm});
            skLineSegment(sketch, "E681.MirrorCS", {"start": v(102.06, 166.22) * mm, "end": v(106.68, 166.22) * mm});
            skLineSegment(sketch, "E682.MirrorCS", {"start": v(100.33, 109.07) * mm, "end": v(100.33, 104.45) * mm});
            skLineSegment(sketch, "E683.MirrorCS", {"start": v(148.82, 83.67) * mm, "end": v(146.51, 83.67) * mm});
            skLineSegment(sketch, "E684.MirrorCS", {"start": v(152.86, 136.2) * mm, "end": v(152.86, 140.82) * mm});
            skLineSegment(sketch, "E685.MirrorCS", {"start": v(110.72, 155.25) * mm, "end": v(108.41, 155.25) * mm});
            skLineSegment(sketch, "E686.MirrorCS", {"start": v(161.52, 155.25) * mm, "end": v(159.21, 155.25) * mm});
            skLineSegment(sketch, "E687.MirrorCS", {"start": v(151.13, 32.87) * mm, "end": v(148.82, 32.87) * mm});
            skLineSegment(sketch, "E688.MirrorCS", {"start": v(138.43, 58.27) * mm, "end": v(136.12, 58.27) * mm});
            skLineSegment(sketch, "E689.MirrorCS", {"start": v(174.22, 45.57) * mm, "end": v(171.91, 45.57) * mm});
            skLineSegment(sketch, "E690.MirrorCS", {"start": v(152.86, 153.52) * mm, "end": v(157.48, 153.52) * mm});
            skLineSegment(sketch, "E691.MirrorCS", {"start": v(106.68, 77.32) * mm, "end": v(106.68, 72.7) * mm});
            skLineSegment(sketch, "E692.MirrorCS", {"start": v(148.82, 45.57) * mm, "end": v(146.51, 45.57) * mm});
            skLineSegment(sketch, "E693.MirrorCS", {"start": v(125.73, 32.87) * mm, "end": v(123.42, 32.87) * mm});
            skLineSegment(sketch, "E694.MirrorCS", {"start": v(133.81, 109.07) * mm, "end": v(133.81, 104.45) * mm});
            skLineSegment(sketch, "E695.MirrorCS", {"start": v(186.92, 70.97) * mm, "end": v(184.61, 70.97) * mm});
            skLineSegment(sketch, "E696.MirrorCS", {"start": v(186.92, 117.15) * mm, "end": v(184.61, 117.15) * mm});
            skLineSegment(sketch, "E697.MirrorCS", {"start": v(136.12, 104.45) * mm, "end": v(133.81, 104.45) * mm});
            skLineSegment(sketch, "E698.MirrorCS", {"start": v(123.42, 58.27) * mm, "end": v(121.11, 58.27) * mm});
            skLineSegment(sketch, "E699.MirrorCS", {"start": v(100.33, 129.85) * mm, "end": v(98.02, 129.85) * mm});
            skLineSegment(sketch, "E700.MirrorCS", {"start": v(95.71, 121.77) * mm, "end": v(100.33, 121.77) * mm});
            skLineSegment(sketch, "E701.MirrorCS", {"start": v(119.38, 47.3) * mm, "end": v(114.76, 47.3) * mm});
            skLineSegment(sketch, "E702.MirrorCS", {"start": v(178.26, 140.82) * mm, "end": v(182.88, 140.82) * mm});
            skLineSegment(sketch, "E703.MirrorCS", {"start": v(102.06, 60) * mm, "end": v(106.68, 60) * mm});
            skLineSegment(sketch, "E704.MirrorCS", {"start": v(108.41, 66.34) * mm, "end": v(108.41, 70.97) * mm});
            skLineSegment(sketch, "E705.MirrorCS", {"start": v(127.46, 26.52) * mm, "end": v(132.08, 26.52) * mm});
            skLineSegment(sketch, "E706.MirrorCS", {"start": v(189.23, 66.34) * mm, "end": v(189.23, 70.97) * mm});
            skLineSegment(sketch, "E707.MirrorCS", {"start": v(152.86, 140.82) * mm, "end": v(157.48, 140.82) * mm});
            skLineSegment(sketch, "E708.MirrorCS", {"start": v(127.46, 47.3) * mm, "end": v(132.08, 47.3) * mm});
            skLineSegment(sketch, "E709.MirrorCS", {"start": v(106.68, 110.8) * mm, "end": v(106.68, 115.42) * mm});
            skLineSegment(sketch, "E710.MirrorCS", {"start": v(138.43, 53.64) * mm, "end": v(133.81, 53.64) * mm});
            skLineSegment(sketch, "E711.MirrorCS", {"start": v(189.23, 83.67) * mm, "end": v(186.92, 83.67) * mm});
            skLineSegment(sketch, "E712.MirrorCS", {"start": v(163.83, 147.17) * mm, "end": v(159.21, 147.17) * mm});
            skLineSegment(sketch, "E713.MirrorCS", {"start": v(133.81, 121.77) * mm, "end": v(133.81, 117.15) * mm});
            skLineSegment(sketch, "E714.MirrorCS", {"start": v(119.38, 39.22) * mm, "end": v(114.76, 39.22) * mm});
            skLineSegment(sketch, "E715.MirrorCS", {"start": v(102.06, 47.3) * mm, "end": v(106.68, 47.3) * mm});
            skLineSegment(sketch, "E716.MirrorCS", {"start": v(184.61, 40.94) * mm, "end": v(184.61, 45.57) * mm});
            skLineSegment(sketch, "E717.MirrorCS", {"start": v(102.06, 136.2) * mm, "end": v(106.68, 136.2) * mm});
            skLineSegment(sketch, "E718.MirrorCS", {"start": v(102.06, 51.92) * mm, "end": v(102.06, 47.3) * mm});
            skLineSegment(sketch, "E719.MirrorCS", {"start": v(146.51, 15.54) * mm, "end": v(151.13, 15.54) * mm});
            skLineSegment(sketch, "E720.MirrorCS", {"start": v(95.71, 40.94) * mm, "end": v(100.33, 40.94) * mm});
            skLineSegment(sketch, "E721.MirrorCS", {"start": v(95.71, 28.24) * mm, "end": v(100.33, 28.24) * mm});
            skLineSegment(sketch, "E722.MirrorCS", {"start": v(178.26, 34.6) * mm, "end": v(182.88, 34.6) * mm});
            skLineSegment(sketch, "E723.MirrorCS", {"start": v(119.38, 64.62) * mm, "end": v(119.38, 60) * mm});
            skLineSegment(sketch, "E724.MirrorCS", {"start": v(138.43, 28.24) * mm, "end": v(133.81, 28.24) * mm});
            skLineSegment(sketch, "E725.MirrorCS", {"start": v(110.72, 7.47) * mm, "end": v(108.41, 7.47) * mm});
            skLineSegment(sketch, "E726.MirrorCS", {"start": v(133.81, 172.57) * mm, "end": v(133.81, 167.95) * mm});
            skLineSegment(sketch, "E727.MirrorCS", {"start": v(138.43, 79.04) * mm, "end": v(138.43, 83.67) * mm});
            skLineSegment(sketch, "E728.MirrorCS", {"start": v(133.81, 2.84) * mm, "end": v(133.81, 7.47) * mm});
            skLineSegment(sketch, "E729.MirrorCS", {"start": v(182.88, 136.2) * mm, "end": v(182.88, 140.82) * mm});
            skLineSegment(sketch, "E730.MirrorCS", {"start": v(138.43, 159.87) * mm, "end": v(138.43, 155.25) * mm});
            skLineSegment(sketch, "E731.MirrorCS", {"start": v(171.91, 147.17) * mm, "end": v(176.53, 147.17) * mm});
            skLineSegment(sketch, "E732.MirrorCS", {"start": v(127.46, 102.72) * mm, "end": v(132.08, 102.72) * mm});
            skLineSegment(sketch, "E733.MirrorCS", {"start": v(127.46, 123.5) * mm, "end": v(132.08, 123.5) * mm});
            skLineSegment(sketch, "E734.MirrorCS", {"start": v(98.02, 142.55) * mm, "end": v(95.71, 142.55) * mm});
            skLineSegment(sketch, "E735.MirrorCS", {"start": v(113.03, 79.04) * mm, "end": v(113.03, 83.67) * mm});
            skLineSegment(sketch, "E736.MirrorCS", {"start": v(125.73, 121.77) * mm, "end": v(125.73, 117.15) * mm});
            skLineSegment(sketch, "E737.MirrorCS", {"start": v(152.86, 161.6) * mm, "end": v(152.86, 166.22) * mm});
            skLineSegment(sketch, "E738.MirrorCS", {"start": v(121.11, 91.75) * mm, "end": v(121.11, 96.37) * mm});
            skLineSegment(sketch, "E739.MirrorCS", {"start": v(102.06, 148.9) * mm, "end": v(106.68, 148.9) * mm});
            skLineSegment(sketch, "E740.MirrorCS", {"start": v(108.41, 147.17) * mm, "end": v(108.41, 142.55) * mm});
            skLineSegment(sketch, "E741.MirrorCS", {"start": v(102.06, 51.92) * mm, "end": v(106.68, 51.92) * mm});
            skLineSegment(sketch, "E742.MirrorCS", {"start": v(176.53, 142.55) * mm, "end": v(174.22, 142.55) * mm});
            skLineSegment(sketch, "E743.MirrorCS", {"start": v(95.71, 7.47) * mm, "end": v(95.71, 2.84) * mm});
            skLineSegment(sketch, "E744.MirrorCS", {"start": v(113.03, 15.54) * mm, "end": v(113.03, 20.17) * mm});
            skLineSegment(sketch, "E745.MirrorCS", {"start": v(127.46, 136.2) * mm, "end": v(132.08, 136.2) * mm});
            skLineSegment(sketch, "E746.MirrorCS", {"start": v(170.18, 21.9) * mm, "end": v(165.56, 21.9) * mm});
            skLineSegment(sketch, "E747.MirrorCS", {"start": v(114.76, 148.9) * mm, "end": v(114.76, 153.52) * mm});
            skLineSegment(sketch, "E748.MirrorCS", {"start": v(102.06, 26.52) * mm, "end": v(106.68, 26.52) * mm});
            skLineSegment(sketch, "E749.MirrorCS", {"start": v(146.51, 121.77) * mm, "end": v(151.13, 121.77) * mm});
            skLineSegment(sketch, "E750.MirrorCS", {"start": v(144.78, 128.12) * mm, "end": v(140.16, 128.12) * mm});
            skLineSegment(sketch, "E751.MirrorCS", {"start": v(125.73, 28.24) * mm, "end": v(125.73, 32.87) * mm});
            skLineSegment(sketch, "E752.MirrorCS", {"start": v(121.11, 20.17) * mm, "end": v(121.11, 15.54) * mm});
            skLineSegment(sketch, "E753.MirrorCS", {"start": v(125.73, 109.07) * mm, "end": v(125.73, 104.45) * mm});
            skLineSegment(sketch, "E754.MirrorCS", {"start": v(163.83, 28.24) * mm, "end": v(159.21, 28.24) * mm});
            skLineSegment(sketch, "E755.MirrorCS", {"start": v(102.06, 161.6) * mm, "end": v(102.06, 166.22) * mm});
            skLineSegment(sketch, "E756.MirrorCS", {"start": v(121.11, 147.17) * mm, "end": v(125.73, 147.17) * mm});
            skLineSegment(sketch, "E757.MirrorCS", {"start": v(121.11, 109.07) * mm, "end": v(125.73, 109.07) * mm});
            skLineSegment(sketch, "E758.MirrorCS", {"start": v(144.78, 26.52) * mm, "end": v(144.78, 21.9) * mm});
            skLineSegment(sketch, "E759.MirrorCS", {"start": v(159.21, 134.47) * mm, "end": v(159.21, 129.85) * mm});
            skLineSegment(sketch, "E760.MirrorCS", {"start": v(138.43, 96.37) * mm, "end": v(133.81, 96.37) * mm});
            skLineSegment(sketch, "E761.MirrorCS", {"start": v(106.68, 26.52) * mm, "end": v(106.68, 21.9) * mm});
            skLineSegment(sketch, "E762.MirrorCS", {"start": v(127.46, 161.6) * mm, "end": v(127.46, 166.22) * mm});
            skLineSegment(sketch, "E763.MirrorCS", {"start": v(144.78, 153.52) * mm, "end": v(140.16, 153.52) * mm});
            skLineSegment(sketch, "E764.MirrorCS", {"start": v(170.18, 128.12) * mm, "end": v(165.56, 128.12) * mm});
            skLineSegment(sketch, "E765.MirrorCS", {"start": v(189.23, 96.37) * mm, "end": v(189.23, 91.75) * mm});
            skLineSegment(sketch, "E766.MirrorCS", {"start": v(100.33, 83.67) * mm, "end": v(98.02, 83.67) * mm});
            skLineSegment(sketch, "E767.MirrorCS", {"start": v(95.71, 83.67) * mm, "end": v(95.71, 79.04) * mm});
            skLineSegment(sketch, "E768.MirrorCS", {"start": v(184.61, 109.07) * mm, "end": v(184.61, 104.45) * mm});
            skLineSegment(sketch, "E769.MirrorCS", {"start": v(113.03, 134.47) * mm, "end": v(108.41, 134.47) * mm});
            skLineSegment(sketch, "E770.MirrorCS", {"start": v(100.33, 70.97) * mm, "end": v(98.02, 70.97) * mm});
            skLineSegment(sketch, "E771.MirrorCS", {"start": v(157.48, 161.6) * mm, "end": v(157.48, 166.22) * mm});
            skLineSegment(sketch, "E772.MirrorCS", {"start": v(140.16, 110.8) * mm, "end": v(140.16, 115.42) * mm});
            skLineSegment(sketch, "E773.MirrorCS", {"start": v(152.86, 110.8) * mm, "end": v(152.86, 115.42) * mm});
            skLineSegment(sketch, "E774.MirrorCS", {"start": v(144.78, 77.32) * mm, "end": v(144.78, 72.7) * mm});
            skLineSegment(sketch, "E775.MirrorCS", {"start": v(144.78, 140.82) * mm, "end": v(140.16, 140.82) * mm});
            skLineSegment(sketch, "E776.MirrorCS", {"start": v(138.43, 96.37) * mm, "end": v(138.43, 91.75) * mm});
            skLineSegment(sketch, "E777.MirrorCS", {"start": v(98.02, 20.17) * mm, "end": v(95.71, 20.17) * mm});
            skLineSegment(sketch, "E778.MirrorCS", {"start": v(127.46, 72.7) * mm, "end": v(132.08, 72.7) * mm});
            skLineSegment(sketch, "E779.MirrorCS", {"start": v(95.71, 70.97) * mm, "end": v(95.71, 66.34) * mm});
            skLineSegment(sketch, "E780.MirrorCS", {"start": v(127.46, 60) * mm, "end": v(132.08, 60) * mm});
            skLineSegment(sketch, "E781.MirrorCS", {"start": v(113.03, 121.77) * mm, "end": v(108.41, 121.77) * mm});
            skLineSegment(sketch, "E782.MirrorCS", {"start": v(102.06, 148.9) * mm, "end": v(102.06, 153.52) * mm});
            skLineSegment(sketch, "E783.MirrorCS", {"start": v(132.08, 110.8) * mm, "end": v(132.08, 115.42) * mm});
            skLineSegment(sketch, "E784.MirrorCS", {"start": v(119.38, 77.32) * mm, "end": v(119.38, 72.7) * mm});
            skLineSegment(sketch, "E785.MirrorCS", {"start": v(95.71, 58.27) * mm, "end": v(95.71, 53.64) * mm});
            skLineSegment(sketch, "E786.MirrorCS", {"start": v(123.42, 32.87) * mm, "end": v(121.11, 32.87) * mm});
            skLineSegment(sketch, "E787.MirrorCS", {"start": v(171.91, 142.55) * mm, "end": v(171.91, 147.17) * mm});
            skLineSegment(sketch, "E788.MirrorCS", {"start": v(144.78, 72.7) * mm, "end": v(140.16, 72.7) * mm});
            skLineSegment(sketch, "E789.MirrorCS", {"start": v(144.78, 98.1) * mm, "end": v(140.16, 98.1) * mm});
            skLineSegment(sketch, "E790.MirrorCS", {"start": v(102.06, 64.62) * mm, "end": v(102.06, 60) * mm});
            skLineSegment(sketch, "E791.MirrorCS", {"start": v(146.51, 83.67) * mm, "end": v(146.51, 79.04) * mm});
            skLineSegment(sketch, "E792.MirrorCS", {"start": v(146.51, 70.97) * mm, "end": v(146.51, 66.34) * mm});
            skLineSegment(sketch, "E793.MirrorCS", {"start": v(113.03, 66.34) * mm, "end": v(113.03, 70.97) * mm});
            skLineSegment(sketch, "E794.MirrorCS", {"start": v(144.78, 110.8) * mm, "end": v(144.78, 115.42) * mm});
            skLineSegment(sketch, "E795.MirrorCS", {"start": v(113.03, 53.64) * mm, "end": v(113.03, 58.27) * mm});
            skLineSegment(sketch, "E796.MirrorCS", {"start": v(146.51, 40.94) * mm, "end": v(151.13, 40.94) * mm});
            skLineSegment(sketch, "E797.MirrorCS", {"start": v(163.83, 40.94) * mm, "end": v(159.21, 40.94) * mm});
            skLineSegment(sketch, "E798.MirrorCS", {"start": v(102.06, 39.22) * mm, "end": v(102.06, 34.6) * mm});
            skLineSegment(sketch, "E799.MirrorCS", {"start": v(102.06, 140.82) * mm, "end": v(106.68, 140.82) * mm});
            skLineSegment(sketch, "E800.MirrorCS", {"start": v(121.11, 32.87) * mm, "end": v(121.11, 28.24) * mm});
            skLineSegment(sketch, "E801.MirrorCS", {"start": v(189.23, 117.15) * mm, "end": v(186.92, 117.15) * mm});
            skLineSegment(sketch, "E802.MirrorCS", {"start": v(171.91, 28.24) * mm, "end": v(176.53, 28.24) * mm});
            skLineSegment(sketch, "E803.MirrorCS", {"start": v(144.78, 60) * mm, "end": v(140.16, 60) * mm});
            skLineSegment(sketch, "E804.MirrorCS", {"start": v(170.18, 47.3) * mm, "end": v(165.56, 47.3) * mm});
            skLineSegment(sketch, "E805.MirrorCS", {"start": v(95.71, 79.04) * mm, "end": v(100.33, 79.04) * mm});
            skLineSegment(sketch, "E806.MirrorCS", {"start": v(178.26, 47.3) * mm, "end": v(182.88, 47.3) * mm});
            skLineSegment(sketch, "E807.MirrorCS", {"start": v(151.13, 66.34) * mm, "end": v(151.13, 70.97) * mm});
            skLineSegment(sketch, "E808.MirrorCS", {"start": v(146.51, 58.27) * mm, "end": v(146.51, 53.64) * mm});
            skLineSegment(sketch, "E809.MirrorCS", {"start": v(178.26, 39.22) * mm, "end": v(178.26, 34.6) * mm});
            skLineSegment(sketch, "E810.MirrorCS", {"start": v(138.43, 142.55) * mm, "end": v(136.12, 142.55) * mm});
            skLineSegment(sketch, "E811.MirrorCS", {"start": v(136.12, 32.87) * mm, "end": v(133.81, 32.87) * mm});
            skLineSegment(sketch, "E812.MirrorCS", {"start": v(98.02, 155.25) * mm, "end": v(95.71, 155.25) * mm});
            skLineSegment(sketch, "E813.MirrorCS", {"start": v(138.43, 20.17) * mm, "end": v(136.12, 20.17) * mm});
            skLineSegment(sketch, "E814.MirrorCS", {"start": v(138.43, 40.94) * mm, "end": v(138.43, 45.57) * mm});
            skLineSegment(sketch, "E815.MirrorCS", {"start": v(95.71, 66.34) * mm, "end": v(100.33, 66.34) * mm});
            skLineSegment(sketch, "E816.MirrorCS", {"start": v(121.11, 40.94) * mm, "end": v(125.73, 40.94) * mm});
            skLineSegment(sketch, "E817.MirrorCS", {"start": v(113.03, 7.47) * mm, "end": v(110.72, 7.47) * mm});
            skLineSegment(sketch, "E818.MirrorCS", {"start": v(189.23, 40.94) * mm, "end": v(184.61, 40.94) * mm});
            skLineSegment(sketch, "E819.MirrorCS", {"start": v(151.13, 53.64) * mm, "end": v(151.13, 58.27) * mm});
            skLineSegment(sketch, "E820.MirrorCS", {"start": v(178.26, 39.22) * mm, "end": v(182.88, 39.22) * mm});
            skLineSegment(sketch, "E821.MirrorCS", {"start": v(138.43, 2.84) * mm, "end": v(138.43, 7.47) * mm});
            skLineSegment(sketch, "E822.MirrorCS", {"start": v(170.18, 140.82) * mm, "end": v(165.56, 140.82) * mm});
            skLineSegment(sketch, "E823.MirrorCS", {"start": v(144.78, 123.5) * mm, "end": v(144.78, 128.12) * mm});
            skLineSegment(sketch, "E824.MirrorCS", {"start": v(95.71, 96.37) * mm, "end": v(100.33, 96.37) * mm});
            skLineSegment(sketch, "E825.MirrorCS", {"start": v(152.86, 47.3) * mm, "end": v(157.48, 47.3) * mm});
            skLineSegment(sketch, "E826.MirrorCS", {"start": v(113.03, 40.94) * mm, "end": v(113.03, 45.57) * mm});
            skLineSegment(sketch, "E827.MirrorCS", {"start": v(113.03, 20.17) * mm, "end": v(110.72, 20.17) * mm});
            skLineSegment(sketch, "E828.MirrorCS", {"start": v(102.06, 98.1) * mm, "end": v(102.06, 102.72) * mm});
            skLineSegment(sketch, "E829.MirrorCS", {"start": v(146.51, 32.87) * mm, "end": v(146.51, 28.24) * mm});
            skLineSegment(sketch, "E830.MirrorCS", {"start": v(127.46, 39.22) * mm, "end": v(127.46, 34.6) * mm});
            skLineSegment(sketch, "E831.MirrorCS", {"start": v(119.38, 136.2) * mm, "end": v(119.38, 140.82) * mm});
            skLineSegment(sketch, "E832.MirrorCS", {"start": v(151.13, 96.37) * mm, "end": v(151.13, 91.75) * mm});
            skLineSegment(sketch, "E833.MirrorCS", {"start": v(95.71, 2.84) * mm, "end": v(100.33, 2.84) * mm});
            skLineSegment(sketch, "E834.MirrorCS", {"start": v(102.06, 110.8) * mm, "end": v(106.68, 110.8) * mm});
            skLineSegment(sketch, "E835.MirrorCS", {"start": v(146.51, 79.04) * mm, "end": v(151.13, 79.04) * mm});
            skLineSegment(sketch, "E836.MirrorCS", {"start": v(152.86, 21.9) * mm, "end": v(157.48, 21.9) * mm});
            skLineSegment(sketch, "E837.MirrorCS", {"start": v(152.86, 26.52) * mm, "end": v(152.86, 21.9) * mm});
            skLineSegment(sketch, "E838.MirrorCS", {"start": v(146.51, 117.15) * mm, "end": v(146.51, 121.77) * mm});
            skLineSegment(sketch, "E839.MirrorCS", {"start": v(114.76, 161.6) * mm, "end": v(114.76, 166.22) * mm});
            skLineSegment(sketch, "E840.MirrorCS", {"start": v(127.46, 166.22) * mm, "end": v(132.08, 166.22) * mm});
            skLineSegment(sketch, "E841.MirrorCS", {"start": v(182.88, 123.5) * mm, "end": v(182.88, 128.12) * mm});
            skLineSegment(sketch, "E842.MirrorCS", {"start": v(184.61, 134.47) * mm, "end": v(184.61, 129.85) * mm});
            skLineSegment(sketch, "E843.MirrorCS", {"start": v(108.41, 172.57) * mm, "end": v(108.41, 167.95) * mm});
            skLineSegment(sketch, "E844.MirrorCS", {"start": v(174.22, 142.55) * mm, "end": v(171.91, 142.55) * mm});
            skLineSegment(sketch, "E845.MirrorCS", {"start": v(165.56, 148.9) * mm, "end": v(165.56, 153.52) * mm});
            skLineSegment(sketch, "E846.MirrorCS", {"start": v(113.03, 159.87) * mm, "end": v(113.03, 155.25) * mm});
            skLineSegment(sketch, "E847.MirrorCS", {"start": v(113.03, 96.37) * mm, "end": v(113.03, 91.75) * mm});
            skLineSegment(sketch, "E848.MirrorCS", {"start": v(121.11, 121.77) * mm, "end": v(125.73, 121.77) * mm});
            skLineSegment(sketch, "E849.MirrorCS", {"start": v(132.08, 161.6) * mm, "end": v(132.08, 166.22) * mm});
            skLineSegment(sketch, "E850.MirrorCS", {"start": v(113.03, 147.17) * mm, "end": v(113.03, 142.55) * mm});
            skLineSegment(sketch, "E851.MirrorCS", {"start": v(95.71, 20.17) * mm, "end": v(95.71, 15.54) * mm});
            skLineSegment(sketch, "E852.MirrorCS", {"start": v(170.18, 136.2) * mm, "end": v(165.56, 136.2) * mm});
            skLineSegment(sketch, "E853.MirrorCS", {"start": v(138.43, 147.17) * mm, "end": v(138.43, 142.55) * mm});
            skLineSegment(sketch, "E854.MirrorCS", {"start": v(189.23, 96.37) * mm, "end": v(184.61, 96.37) * mm});
            skLineSegment(sketch, "E855.MirrorCS", {"start": v(102.06, 13.82) * mm, "end": v(102.06, 9.2) * mm});
            skLineSegment(sketch, "E856.MirrorCS", {"start": v(127.46, 64.62) * mm, "end": v(127.46, 60) * mm});
            skLineSegment(sketch, "E857.MirrorCS", {"start": v(114.76, 13.82) * mm, "end": v(114.76, 9.2) * mm});
            skLineSegment(sketch, "E858.MirrorCS", {"start": v(152.86, 128.12) * mm, "end": v(157.48, 128.12) * mm});
            skLineSegment(sketch, "E859.MirrorCS", {"start": v(127.46, 110.8) * mm, "end": v(132.08, 110.8) * mm});
            skLineSegment(sketch, "E860.MirrorCS", {"start": v(133.81, 159.87) * mm, "end": v(133.81, 155.25) * mm});
            skLineSegment(sketch, "E861.MirrorCS", {"start": v(151.13, 79.04) * mm, "end": v(151.13, 83.67) * mm});
            skLineSegment(sketch, "E862.MirrorCS", {"start": v(95.71, 134.47) * mm, "end": v(100.33, 134.47) * mm});
            skLineSegment(sketch, "E863.MirrorCS", {"start": v(138.43, 134.47) * mm, "end": v(133.81, 134.47) * mm});
            skLineSegment(sketch, "E864.MirrorCS", {"start": v(113.03, 109.07) * mm, "end": v(113.03, 104.45) * mm});
            skLineSegment(sketch, "E865.MirrorCS", {"start": v(178.26, 136.2) * mm, "end": v(178.26, 140.82) * mm});
            skLineSegment(sketch, "E866.MirrorCS", {"start": v(144.78, 166.22) * mm, "end": v(140.16, 166.22) * mm});
            skLineSegment(sketch, "E867.MirrorCS", {"start": v(146.51, 91.75) * mm, "end": v(146.51, 96.37) * mm});
            skLineSegment(sketch, "E868.MirrorCS", {"start": v(119.38, 9.2) * mm, "end": v(114.76, 9.2) * mm});
            skLineSegment(sketch, "E869.MirrorCS", {"start": v(138.43, 121.77) * mm, "end": v(138.43, 117.15) * mm});
            skLineSegment(sketch, "E870.MirrorCS", {"start": v(125.73, 147.17) * mm, "end": v(125.73, 142.55) * mm});
            skLineSegment(sketch, "E871.MirrorCS", {"start": v(146.51, 167.95) * mm, "end": v(146.51, 172.57) * mm});
            skLineSegment(sketch, "E872.MirrorCS", {"start": v(138.43, 28.24) * mm, "end": v(138.43, 32.87) * mm});
            skLineSegment(sketch, "E873.MirrorCS", {"start": v(119.38, 98.1) * mm, "end": v(114.76, 98.1) * mm});
            skLineSegment(sketch, "E874.MirrorCS", {"start": v(95.71, 172.57) * mm, "end": v(100.33, 172.57) * mm});
            skLineSegment(sketch, "E875.MirrorCS", {"start": v(132.08, 123.5) * mm, "end": v(132.08, 128.12) * mm});
            skLineSegment(sketch, "E876.MirrorCS", {"start": v(189.23, 134.47) * mm, "end": v(189.23, 129.85) * mm});
            skLineSegment(sketch, "E877.MirrorCS", {"start": v(119.38, 161.6) * mm, "end": v(114.76, 161.6) * mm});
            skLineSegment(sketch, "E878.MirrorCS", {"start": v(100.33, 147.17) * mm, "end": v(100.33, 142.55) * mm});
            skLineSegment(sketch, "E879.MirrorCS", {"start": v(140.16, 161.6) * mm, "end": v(140.16, 166.22) * mm});
            skLineSegment(sketch, "E880.MirrorCS", {"start": v(144.78, 161.6) * mm, "end": v(140.16, 161.6) * mm});
            skLineSegment(sketch, "E881.MirrorCS", {"start": v(113.03, 172.57) * mm, "end": v(108.41, 172.57) * mm});
            skLineSegment(sketch, "E882.MirrorCS", {"start": v(163.83, 147.17) * mm, "end": v(163.83, 142.55) * mm});
            skLineSegment(sketch, "E883.MirrorCS", {"start": v(171.91, 134.47) * mm, "end": v(176.53, 134.47) * mm});
            skLineSegment(sketch, "E884.MirrorCS", {"start": v(95.71, 159.87) * mm, "end": v(100.33, 159.87) * mm});
            skLineSegment(sketch, "E885.MirrorCS", {"start": v(121.11, 117.15) * mm, "end": v(121.11, 121.77) * mm});
            skLineSegment(sketch, "E886.MirrorCS", {"start": v(146.51, 155.25) * mm, "end": v(146.51, 159.87) * mm});
            skLineSegment(sketch, "E887.MirrorCS", {"start": v(125.73, 134.47) * mm, "end": v(125.73, 129.85) * mm});
            skLineSegment(sketch, "E888.MirrorCS", {"start": v(184.61, 66.34) * mm, "end": v(184.61, 70.97) * mm});
            skLineSegment(sketch, "E889.MirrorCS", {"start": v(102.06, 64.62) * mm, "end": v(106.68, 64.62) * mm});
            skLineSegment(sketch, "E890.MirrorCS", {"start": v(138.43, 66.34) * mm, "end": v(133.81, 66.34) * mm});
            skLineSegment(sketch, "E891.MirrorCS", {"start": v(125.73, 15.54) * mm, "end": v(125.73, 20.17) * mm});
            skLineSegment(sketch, "E892.MirrorCS", {"start": v(184.61, 53.64) * mm, "end": v(184.61, 58.27) * mm});
            skLineSegment(sketch, "E893.MirrorCS", {"start": v(146.51, 66.34) * mm, "end": v(151.13, 66.34) * mm});
            skLineSegment(sketch, "E894.MirrorCS", {"start": v(144.78, 47.3) * mm, "end": v(140.16, 47.3) * mm});
            skLineSegment(sketch, "E895.MirrorCS", {"start": v(132.08, 148.9) * mm, "end": v(132.08, 153.52) * mm});
            skLineSegment(sketch, "E896.MirrorCS", {"start": v(176.53, 134.47) * mm, "end": v(176.53, 129.85) * mm});
            skLineSegment(sketch, "E897.MirrorCS", {"start": v(127.46, 64.62) * mm, "end": v(132.08, 64.62) * mm});
            skLineSegment(sketch, "E898.MirrorCS", {"start": v(140.16, 51.92) * mm, "end": v(140.16, 47.3) * mm});
            skLineSegment(sketch, "E899.MirrorCS", {"start": v(125.73, 40.94) * mm, "end": v(125.73, 45.57) * mm});
            skLineSegment(sketch, "E900.MirrorCS", {"start": v(176.53, 40.94) * mm, "end": v(176.53, 45.57) * mm});
            skLineSegment(sketch, "E901.MirrorCS", {"start": v(146.51, 28.24) * mm, "end": v(151.13, 28.24) * mm});
            skLineSegment(sketch, "E902.MirrorCS", {"start": v(148.82, 20.17) * mm, "end": v(146.51, 20.17) * mm});
            skLineSegment(sketch, "E903.MirrorCS", {"start": v(95.71, 142.55) * mm, "end": v(95.71, 147.17) * mm});
            skLineSegment(sketch, "E904.MirrorCS", {"start": v(151.13, 28.24) * mm, "end": v(151.13, 32.87) * mm});
            skLineSegment(sketch, "E905.MirrorCS", {"start": v(119.38, 51.92) * mm, "end": v(114.76, 51.92) * mm});
            skLineSegment(sketch, "E906.MirrorCS", {"start": v(102.06, 34.6) * mm, "end": v(106.68, 34.6) * mm});
            skLineSegment(sketch, "E907.MirrorCS", {"start": v(138.43, 15.54) * mm, "end": v(138.43, 20.17) * mm});
            skLineSegment(sketch, "E908.MirrorCS", {"start": v(146.51, 53.64) * mm, "end": v(151.13, 53.64) * mm});
            skLineSegment(sketch, "E909.MirrorCS", {"start": v(152.86, 26.52) * mm, "end": v(157.48, 26.52) * mm});
            skLineSegment(sketch, "E910.MirrorCS", {"start": v(152.86, 98.1) * mm, "end": v(152.86, 102.72) * mm});
            skLineSegment(sketch, "E911.MirrorCS", {"start": v(163.83, 134.47) * mm, "end": v(159.21, 134.47) * mm});
            skLineSegment(sketch, "E912.MirrorCS", {"start": v(152.86, 34.6) * mm, "end": v(157.48, 34.6) * mm});
            skLineSegment(sketch, "E913.MirrorCS", {"start": v(138.43, 32.87) * mm, "end": v(136.12, 32.87) * mm});
            skLineSegment(sketch, "E914.MirrorCS", {"start": v(102.06, 128.12) * mm, "end": v(106.68, 128.12) * mm});
            skLineSegment(sketch, "E915.MirrorCS", {"start": v(170.18, 148.9) * mm, "end": v(165.56, 148.9) * mm});
            skLineSegment(sketch, "E916.MirrorCS", {"start": v(152.86, 161.6) * mm, "end": v(157.48, 161.6) * mm});
            skLineSegment(sketch, "E917.MirrorCS", {"start": v(171.91, 45.57) * mm, "end": v(171.91, 40.94) * mm});
            skLineSegment(sketch, "E918.MirrorCS", {"start": v(125.73, 172.57) * mm, "end": v(125.73, 167.95) * mm});
            skLineSegment(sketch, "E919.MirrorCS", {"start": v(146.51, 109.07) * mm, "end": v(151.13, 109.07) * mm});
            skLineSegment(sketch, "E920.MirrorCS", {"start": v(140.16, 123.5) * mm, "end": v(140.16, 128.12) * mm});
            skLineSegment(sketch, "E921.MirrorCS", {"start": v(95.71, 109.07) * mm, "end": v(100.33, 109.07) * mm});
            skLineSegment(sketch, "E922.MirrorCS", {"start": v(127.46, 34.6) * mm, "end": v(132.08, 34.6) * mm});
            skLineSegment(sketch, "E923.MirrorCS", {"start": v(108.41, 40.94) * mm, "end": v(108.41, 45.57) * mm});
            skLineSegment(sketch, "E924.MirrorCS", {"start": v(140.16, 26.52) * mm, "end": v(140.16, 21.9) * mm});
            skLineSegment(sketch, "E925.MirrorCS", {"start": v(125.73, 104.45) * mm, "end": v(123.42, 104.45) * mm});
            skLineSegment(sketch, "E926.MirrorCS", {"start": v(148.82, 117.15) * mm, "end": v(146.51, 117.15) * mm});
            skLineSegment(sketch, "E927.MirrorCS", {"start": v(100.33, 20.17) * mm, "end": v(98.02, 20.17) * mm});
            skLineSegment(sketch, "E928.MirrorCS", {"start": v(184.61, 79.04) * mm, "end": v(184.61, 83.67) * mm});
            skLineSegment(sketch, "E929.MirrorCS", {"start": v(113.03, 28.24) * mm, "end": v(108.41, 28.24) * mm});
            skLineSegment(sketch, "E930.MirrorCS", {"start": v(113.03, 28.24) * mm, "end": v(113.03, 32.87) * mm});
            skLineSegment(sketch, "E931.MirrorCS", {"start": v(113.03, 117.15) * mm, "end": v(110.72, 117.15) * mm});
            skLineSegment(sketch, "E932.MirrorCS", {"start": v(125.73, 2.84) * mm, "end": v(125.73, 7.47) * mm});
            skLineSegment(sketch, "E933.MirrorCS", {"start": v(163.83, 15.54) * mm, "end": v(163.83, 20.17) * mm});
            skLineSegment(sketch, "E934.MirrorCS", {"start": v(189.23, 134.47) * mm, "end": v(184.61, 134.47) * mm});
            skLineSegment(sketch, "E935.MirrorCS", {"start": v(95.71, 91.75) * mm, "end": v(95.71, 96.37) * mm});
            skLineSegment(sketch, "E936.MirrorCS", {"start": v(119.38, 102.72) * mm, "end": v(114.76, 102.72) * mm});
            skLineSegment(sketch, "E937.MirrorCS", {"start": v(95.71, 53.64) * mm, "end": v(100.33, 53.64) * mm});
            skLineSegment(sketch, "E938.MirrorCS", {"start": v(170.18, 39.22) * mm, "end": v(165.56, 39.22) * mm});
            skLineSegment(sketch, "E939.MirrorCS", {"start": v(152.86, 136.2) * mm, "end": v(157.48, 136.2) * mm});
            skLineSegment(sketch, "E940.MirrorCS", {"start": v(127.46, 115.42) * mm, "end": v(132.08, 115.42) * mm});
            skLineSegment(sketch, "E941.MirrorCS", {"start": v(102.06, 123.5) * mm, "end": v(106.68, 123.5) * mm});
            skLineSegment(sketch, "E942.MirrorCS", {"start": v(138.43, 104.45) * mm, "end": v(136.12, 104.45) * mm});
            skLineSegment(sketch, "E943.MirrorCS", {"start": v(170.18, 26.52) * mm, "end": v(170.18, 21.9) * mm});
            skLineSegment(sketch, "E944.MirrorCS", {"start": v(182.88, 110.8) * mm, "end": v(182.88, 115.42) * mm});
            skLineSegment(sketch, "E945.MirrorCS", {"start": v(106.68, 123.5) * mm, "end": v(106.68, 128.12) * mm});
            skLineSegment(sketch, "E946.MirrorCS", {"start": v(133.81, 96.37) * mm, "end": v(133.81, 91.75) * mm});
            skLineSegment(sketch, "E947.MirrorCS", {"start": v(170.18, 153.52) * mm, "end": v(165.56, 153.52) * mm});
            skLineSegment(sketch, "E948.MirrorCS", {"start": v(144.78, 148.9) * mm, "end": v(140.16, 148.9) * mm});
            skLineSegment(sketch, "E949.MirrorCS", {"start": v(119.38, 148.9) * mm, "end": v(119.38, 153.52) * mm});
            skLineSegment(sketch, "E950.MirrorCS", {"start": v(95.71, 155.25) * mm, "end": v(95.71, 159.87) * mm});
            skLineSegment(sketch, "E951.MirrorCS", {"start": v(121.11, 28.24) * mm, "end": v(125.73, 28.24) * mm});
            skLineSegment(sketch, "E952.MirrorCS", {"start": v(95.71, 32.87) * mm, "end": v(95.71, 28.24) * mm});
            skLineSegment(sketch, "E953.MirrorCS", {"start": v(125.73, 159.87) * mm, "end": v(125.73, 155.25) * mm});
            skLineSegment(sketch, "E954.MirrorCS", {"start": v(159.21, 159.87) * mm, "end": v(159.21, 155.25) * mm});
            skLineSegment(sketch, "E955.MirrorCS", {"start": v(100.33, 79.04) * mm, "end": v(100.33, 83.67) * mm});
            skLineSegment(sketch, "E956.MirrorCS", {"start": v(100.33, 66.34) * mm, "end": v(100.33, 70.97) * mm});
            skLineSegment(sketch, "E957.MirrorCS", {"start": v(165.56, 136.2) * mm, "end": v(165.56, 140.82) * mm});
            skLineSegment(sketch, "E958.MirrorCS", {"start": v(106.68, 136.2) * mm, "end": v(106.68, 140.82) * mm});
            skLineSegment(sketch, "E959.MirrorCS", {"start": v(114.76, 77.32) * mm, "end": v(114.76, 72.7) * mm});
            skLineSegment(sketch, "E960.MirrorCS", {"start": v(140.16, 39.22) * mm, "end": v(140.16, 34.6) * mm});
            skLineSegment(sketch, "E961.MirrorCS", {"start": v(133.81, 66.34) * mm, "end": v(133.81, 70.97) * mm});
            skLineSegment(sketch, "E962.MirrorCS", {"start": v(138.43, 15.54) * mm, "end": v(133.81, 15.54) * mm});
            skLineSegment(sketch, "E963.MirrorCS", {"start": v(170.18, 136.2) * mm, "end": v(170.18, 140.82) * mm});
            skLineSegment(sketch, "E964.MirrorCS", {"start": v(121.11, 53.64) * mm, "end": v(125.73, 53.64) * mm});
            skLineSegment(sketch, "E965.MirrorCS", {"start": v(189.23, 53.64) * mm, "end": v(184.61, 53.64) * mm});
            skLineSegment(sketch, "E966.MirrorCS", {"start": v(121.11, 70.97) * mm, "end": v(121.11, 66.34) * mm});
            skLineSegment(sketch, "E967.MirrorCS", {"start": v(127.46, 51.92) * mm, "end": v(132.08, 51.92) * mm});
            skLineSegment(sketch, "E968.MirrorCS", {"start": v(121.11, 58.27) * mm, "end": v(121.11, 53.64) * mm});
            skLineSegment(sketch, "E969.MirrorCS", {"start": v(138.43, 40.94) * mm, "end": v(133.81, 40.94) * mm});
            skLineSegment(sketch, "E970.MirrorCS", {"start": v(182.88, 98.1) * mm, "end": v(182.88, 102.72) * mm});
            skLineSegment(sketch, "E971.MirrorCS", {"start": v(121.11, 129.85) * mm, "end": v(121.11, 134.47) * mm});
            skLineSegment(sketch, "E972.MirrorCS", {"start": v(151.13, 2.84) * mm, "end": v(151.13, 7.47) * mm});
            skLineSegment(sketch, "E973.MirrorCS", {"start": v(144.78, 148.9) * mm, "end": v(144.78, 153.52) * mm});
            skLineSegment(sketch, "E974.MirrorCS", {"start": v(121.11, 155.25) * mm, "end": v(121.11, 159.87) * mm});
            skLineSegment(sketch, "E975.MirrorCS", {"start": v(157.48, 148.9) * mm, "end": v(157.48, 153.52) * mm});
            skLineSegment(sketch, "E976.MirrorCS", {"start": v(138.43, 109.07) * mm, "end": v(138.43, 104.45) * mm});
            skLineSegment(sketch, "E977.MirrorCS", {"start": v(157.48, 13.82) * mm, "end": v(157.48, 9.2) * mm});
            skLineSegment(sketch, "E978.MirrorCS", {"start": v(146.51, 7.47) * mm, "end": v(146.51, 2.84) * mm});
            skLineSegment(sketch, "E979.MirrorCS", {"start": v(113.03, 40.94) * mm, "end": v(108.41, 40.94) * mm});
            skLineSegment(sketch, "E980.MirrorCS", {"start": v(152.86, 51.92) * mm, "end": v(152.86, 47.3) * mm});
            skLineSegment(sketch, "E981.MirrorCS", {"start": v(133.81, 134.47) * mm, "end": v(133.81, 129.85) * mm});
            skLineSegment(sketch, "E982.MirrorCS", {"start": v(114.76, 51.92) * mm, "end": v(114.76, 47.3) * mm});
            skLineSegment(sketch, "E983.MirrorCS", {"start": v(119.38, 148.9) * mm, "end": v(114.76, 148.9) * mm});
            skLineSegment(sketch, "E984.MirrorCS", {"start": v(136.12, 20.17) * mm, "end": v(133.81, 20.17) * mm});
            skLineSegment(sketch, "E985.MirrorCS", {"start": v(100.33, 28.24) * mm, "end": v(100.33, 32.87) * mm});
            skLineSegment(sketch, "E986.MirrorCS", {"start": v(102.06, 39.22) * mm, "end": v(106.68, 39.22) * mm});
            skLineSegment(sketch, "E987.MirrorCS", {"start": v(170.18, 39.22) * mm, "end": v(170.18, 34.6) * mm});
            skLineSegment(sketch, "E988.MirrorCS", {"start": v(119.38, 13.82) * mm, "end": v(114.76, 13.82) * mm});
            skLineSegment(sketch, "E989.MirrorCS", {"start": v(108.41, 15.54) * mm, "end": v(108.41, 20.17) * mm});
            skLineSegment(sketch, "E990.MirrorCS", {"start": v(114.76, 26.52) * mm, "end": v(114.76, 21.9) * mm});
            skLineSegment(sketch, "E991.MirrorCS", {"start": v(127.46, 98.1) * mm, "end": v(132.08, 98.1) * mm});
            skLineSegment(sketch, "E992.MirrorCS", {"start": v(121.11, 96.37) * mm, "end": v(125.73, 96.37) * mm});
            skLineSegment(sketch, "E993.MirrorCS", {"start": v(102.06, 136.2) * mm, "end": v(102.06, 140.82) * mm});
            skLineSegment(sketch, "E994.MirrorCS", {"start": v(127.46, 148.9) * mm, "end": v(132.08, 148.9) * mm});
            skLineSegment(sketch, "E995.MirrorCS", {"start": v(163.83, 159.87) * mm, "end": v(163.83, 155.25) * mm});
            skLineSegment(sketch, "E996.MirrorCS", {"start": v(152.86, 64.62) * mm, "end": v(152.86, 60) * mm});
            skLineSegment(sketch, "E997.MirrorCS", {"start": v(114.76, 64.62) * mm, "end": v(114.76, 60) * mm});
            skLineSegment(sketch, "E998.MirrorCS", {"start": v(174.22, 129.85) * mm, "end": v(171.91, 129.85) * mm});
            skLineSegment(sketch, "E999.MirrorCS", {"start": v(102.06, 98.1) * mm, "end": v(106.68, 98.1) * mm});
            skLineSegment(sketch, "E1000.MirrorCS", {"start": v(121.11, 79.04) * mm, "end": v(125.73, 79.04) * mm});
            skLineSegment(sketch, "E1001.MirrorCS", {"start": v(113.03, 109.07) * mm, "end": v(108.41, 109.07) * mm});
            skLineSegment(sketch, "E1002.MirrorCS", {"start": v(121.11, 83.67) * mm, "end": v(121.11, 79.04) * mm});
            skLineSegment(sketch, "E1003.MirrorCS", {"start": v(132.08, 51.92) * mm, "end": v(132.08, 47.3) * mm});
            skLineSegment(sketch, "E1004.MirrorCS", {"start": v(144.78, 51.92) * mm, "end": v(140.16, 51.92) * mm});
            skLineSegment(sketch, "E1005.MirrorCS", {"start": v(108.41, 28.24) * mm, "end": v(108.41, 32.87) * mm});
            skLineSegment(sketch, "E1006.MirrorCS", {"start": v(121.11, 66.34) * mm, "end": v(125.73, 66.34) * mm});
            skLineSegment(sketch, "E1007.MirrorCS", {"start": v(189.23, 66.34) * mm, "end": v(184.61, 66.34) * mm});
            skLineSegment(sketch, "E1008.MirrorCS", {"start": v(100.33, 53.64) * mm, "end": v(100.33, 58.27) * mm});
            skLineSegment(sketch, "E1009.MirrorCS", {"start": v(152.86, 39.22) * mm, "end": v(157.48, 39.22) * mm});
            skLineSegment(sketch, "E1010.MirrorCS", {"start": v(100.33, 32.87) * mm, "end": v(98.02, 32.87) * mm});
            skLineSegment(sketch, "E1011.MirrorCS", {"start": v(106.68, 51.92) * mm, "end": v(106.68, 47.3) * mm});
            skLineSegment(sketch, "E1012.MirrorCS", {"start": v(119.38, 153.52) * mm, "end": v(114.76, 153.52) * mm});
            skLineSegment(sketch, "E1013.MirrorCS", {"start": v(132.08, 26.52) * mm, "end": v(132.08, 21.9) * mm});
            skLineSegment(sketch, "E1014.MirrorCS", {"start": v(108.41, 159.87) * mm, "end": v(108.41, 155.25) * mm});
            skLineSegment(sketch, "E1015.MirrorCS", {"start": v(152.86, 148.9) * mm, "end": v(157.48, 148.9) * mm});
            skLineSegment(sketch, "E1016.MirrorCS", {"start": v(102.06, 115.42) * mm, "end": v(106.68, 115.42) * mm});
            skLineSegment(sketch, "E1017.MirrorCS", {"start": v(113.03, 121.77) * mm, "end": v(113.03, 117.15) * mm});
            skLineSegment(sketch, "E1018.MirrorCS", {"start": v(176.53, 28.24) * mm, "end": v(176.53, 32.87) * mm});
            skLineSegment(sketch, "E1019.MirrorCS", {"start": v(127.46, 153.52) * mm, "end": v(132.08, 153.52) * mm});
            skLineSegment(sketch, "E1020.MirrorCS", {"start": v(121.11, 172.57) * mm, "end": v(125.73, 172.57) * mm});
            skLineSegment(sketch, "E1021.MirrorCS", {"start": v(113.03, 172.57) * mm, "end": v(113.03, 167.95) * mm});
            skLineSegment(sketch, "E1022.MirrorCS", {"start": v(138.43, 2.84) * mm, "end": v(133.81, 2.84) * mm});
            skLineSegment(sketch, "E1023.MirrorCS", {"start": v(100.33, 2.84) * mm, "end": v(100.33, 7.47) * mm});
            skLineSegment(sketch, "E1024.MirrorCS", {"start": v(133.81, 15.54) * mm, "end": v(133.81, 20.17) * mm});
            skLineSegment(sketch, "E1025.MirrorCS", {"start": v(119.38, 51.92) * mm, "end": v(119.38, 47.3) * mm});
            skLineSegment(sketch, "E1026.MirrorCS", {"start": v(152.86, 123.5) * mm, "end": v(152.86, 128.12) * mm});
            skLineSegment(sketch, "E1027.MirrorCS", {"start": v(100.33, 142.55) * mm, "end": v(98.02, 142.55) * mm});
            skLineSegment(sketch, "E1028.MirrorCS", {"start": v(98.02, 167.95) * mm, "end": v(95.71, 167.95) * mm});
            skLineSegment(sketch, "E1029.MirrorCS", {"start": v(170.18, 34.6) * mm, "end": v(165.56, 34.6) * mm});
            skLineSegment(sketch, "E1030.MirrorCS", {"start": v(102.06, 123.5) * mm, "end": v(102.06, 128.12) * mm});
            skLineSegment(sketch, "E1031.MirrorCS", {"start": v(159.21, 15.54) * mm, "end": v(159.21, 20.17) * mm});
            skLineSegment(sketch, "E1032.MirrorCS", {"start": v(114.76, 136.2) * mm, "end": v(114.76, 140.82) * mm});
            skLineSegment(sketch, "E1033.MirrorCS", {"start": v(152.86, 148.9) * mm, "end": v(152.86, 153.52) * mm});
            skLineSegment(sketch, "E1034.MirrorCS", {"start": v(178.26, 136.2) * mm, "end": v(182.88, 136.2) * mm});
            skLineSegment(sketch, "E1035.MirrorCS", {"start": v(127.46, 140.82) * mm, "end": v(132.08, 140.82) * mm});
            skLineSegment(sketch, "E1036.MirrorCS", {"start": v(100.33, 96.37) * mm, "end": v(100.33, 91.75) * mm});
            skLineSegment(sketch, "E1037.MirrorCS", {"start": v(110.72, 117.15) * mm, "end": v(108.41, 117.15) * mm});
            skLineSegment(sketch, "E1038.MirrorCS", {"start": v(125.73, 79.04) * mm, "end": v(125.73, 83.67) * mm});
            skLineSegment(sketch, "E1039.MirrorCS", {"start": v(184.61, 96.37) * mm, "end": v(184.61, 91.75) * mm});
            skLineSegment(sketch, "E1040.MirrorCS", {"start": v(125.73, 66.34) * mm, "end": v(125.73, 70.97) * mm});
            skLineSegment(sketch, "E1041.MirrorCS", {"start": v(119.38, 77.32) * mm, "end": v(114.76, 77.32) * mm});
            skLineSegment(sketch, "E1042.MirrorCS", {"start": v(171.91, 129.85) * mm, "end": v(171.91, 134.47) * mm});
            skLineSegment(sketch, "E1043.MirrorCS", {"start": v(119.38, 64.62) * mm, "end": v(114.76, 64.62) * mm});
            skLineSegment(sketch, "E1044.MirrorCS", {"start": v(113.03, 96.37) * mm, "end": v(108.41, 96.37) * mm});
            skLineSegment(sketch, "E1045.MirrorCS", {"start": v(146.51, 104.45) * mm, "end": v(146.51, 109.07) * mm});
            skLineSegment(sketch, "E1046.MirrorCS", {"start": v(119.38, 110.8) * mm, "end": v(114.76, 110.8) * mm});
            skLineSegment(sketch, "E1047.MirrorCS", {"start": v(189.23, 121.77) * mm, "end": v(184.61, 121.77) * mm});
            skLineSegment(sketch, "E1048.MirrorCS", {"start": v(119.38, 110.8) * mm, "end": v(119.38, 115.42) * mm});
            skLineSegment(sketch, "E1049.MirrorCS", {"start": v(189.23, 109.07) * mm, "end": v(184.61, 109.07) * mm});
            skLineSegment(sketch, "E1050.MirrorCS", {"start": v(151.13, 134.47) * mm, "end": v(151.13, 129.85) * mm});
            skLineSegment(sketch, "E1051.MirrorCS", {"start": v(146.51, 142.55) * mm, "end": v(146.51, 147.17) * mm});
            skLineSegment(sketch, "E1052.MirrorCS", {"start": v(138.43, 172.57) * mm, "end": v(138.43, 167.95) * mm});
            skLineSegment(sketch, "E1053.MirrorCS", {"start": v(151.13, 159.87) * mm, "end": v(151.13, 155.25) * mm});
            skLineSegment(sketch, "E1054.MirrorCS", {"start": v(125.73, 53.64) * mm, "end": v(125.73, 58.27) * mm});
            skLineSegment(sketch, "E1055.MirrorCS", {"start": v(114.76, 39.22) * mm, "end": v(114.76, 34.6) * mm});
            skLineSegment(sketch, "E1056.MirrorCS", {"start": v(174.22, 32.87) * mm, "end": v(171.91, 32.87) * mm});
            skLineSegment(sketch, "E1057.MirrorCS", {"start": v(176.53, 32.87) * mm, "end": v(174.22, 32.87) * mm});
            skLineSegment(sketch, "E1058.MirrorCS", {"start": v(163.83, 40.94) * mm, "end": v(163.83, 45.57) * mm});
            skLineSegment(sketch, "E1059.MirrorCS", {"start": v(189.23, 58.27) * mm, "end": v(186.92, 58.27) * mm});
            skLineSegment(sketch, "E1060.MirrorCS", {"start": v(108.41, 96.37) * mm, "end": v(108.41, 91.75) * mm});
            skLineSegment(sketch, "E1061.MirrorCS", {"start": v(132.08, 98.1) * mm, "end": v(132.08, 102.72) * mm});
            skLineSegment(sketch, "E1062.MirrorCS", {"start": v(119.38, 140.82) * mm, "end": v(114.76, 140.82) * mm});
            skLineSegment(sketch, "E1063.MirrorCS", {"start": v(165.56, 26.52) * mm, "end": v(165.56, 21.9) * mm});
            skLineSegment(sketch, "E1064.MirrorCS", {"start": v(121.11, 15.54) * mm, "end": v(125.73, 15.54) * mm});
            skLineSegment(sketch, "E1065.MirrorCS", {"start": v(171.91, 32.87) * mm, "end": v(171.91, 28.24) * mm});
            skLineSegment(sketch, "E1066.MirrorCS", {"start": v(152.86, 39.22) * mm, "end": v(152.86, 34.6) * mm});
            skLineSegment(sketch, "E1067.MirrorCS", {"start": v(113.03, 2.84) * mm, "end": v(108.41, 2.84) * mm});
            skLineSegment(sketch, "E1068.MirrorCS", {"start": v(123.42, 83.67) * mm, "end": v(121.11, 83.67) * mm});
            skLineSegment(sketch, "E1069.MirrorCS", {"start": v(108.41, 79.04) * mm, "end": v(108.41, 83.67) * mm});
            skLineSegment(sketch, "E1070.MirrorCS", {"start": v(119.38, 26.52) * mm, "end": v(119.38, 21.9) * mm});
            skLineSegment(sketch, "E1071.MirrorCS", {"start": v(119.38, 21.9) * mm, "end": v(114.76, 21.9) * mm});
            skLineSegment(sketch, "E1072.MirrorCS", {"start": v(113.03, 53.64) * mm, "end": v(108.41, 53.64) * mm});
            skLineSegment(sketch, "E1073.MirrorCS", {"start": v(144.78, 13.82) * mm, "end": v(140.16, 13.82) * mm});
            skLineSegment(sketch, "E1074.MirrorCS", {"start": v(121.11, 159.87) * mm, "end": v(125.73, 159.87) * mm});
            skLineSegment(sketch, "E1075.MirrorCS", {"start": v(148.82, 142.55) * mm, "end": v(146.51, 142.55) * mm});
            skLineSegment(sketch, "E1076.MirrorCS", {"start": v(144.78, 9.2) * mm, "end": v(140.16, 9.2) * mm});
            skLineSegment(sketch, "E1077.MirrorCS", {"start": v(152.86, 9.2) * mm, "end": v(157.48, 9.2) * mm});
            skLineSegment(sketch, "E1078.MirrorCS", {"start": v(140.16, 13.82) * mm, "end": v(140.16, 9.2) * mm});
            skLineSegment(sketch, "E1079.MirrorCS", {"start": v(95.71, 104.45) * mm, "end": v(95.71, 109.07) * mm});
            skLineSegment(sketch, "E1080.MirrorCS", {"start": v(148.82, 7.47) * mm, "end": v(146.51, 7.47) * mm});
            skLineSegment(sketch, "E1081.MirrorCS", {"start": v(106.68, 148.9) * mm, "end": v(106.68, 153.52) * mm});
            skLineSegment(sketch, "E1082.MirrorCS", {"start": v(146.51, 2.84) * mm, "end": v(151.13, 2.84) * mm});
            skLineSegment(sketch, "E1083.MirrorCS", {"start": v(119.38, 128.12) * mm, "end": v(114.76, 128.12) * mm});
            skLineSegment(sketch, "E1084.MirrorCS", {"start": v(144.78, 13.82) * mm, "end": v(144.78, 9.2) * mm});
            skLineSegment(sketch, "E1085.MirrorCS", {"start": v(144.78, 39.22) * mm, "end": v(144.78, 34.6) * mm});
            skLineSegment(sketch, "E1086.MirrorCS", {"start": v(146.51, 159.87) * mm, "end": v(151.13, 159.87) * mm});
            skLineSegment(sketch, "E1087.MirrorCS", {"start": v(121.11, 7.47) * mm, "end": v(121.11, 2.84) * mm});
            skLineSegment(sketch, "E1088.MirrorCS", {"start": v(121.11, 2.84) * mm, "end": v(125.73, 2.84) * mm});
            skLineSegment(sketch, "E1089.MirrorCS", {"start": v(119.38, 13.82) * mm, "end": v(119.38, 9.2) * mm});
            skLineSegment(sketch, "E1090.MirrorCS", {"start": v(132.08, 64.62) * mm, "end": v(132.08, 60) * mm});
            skLineSegment(sketch, "E1091.MirrorCS", {"start": v(159.21, 147.17) * mm, "end": v(159.21, 142.55) * mm});
            skLineSegment(sketch, "E1092.MirrorCS", {"start": v(144.78, 161.6) * mm, "end": v(144.78, 166.22) * mm});
            skLineSegment(sketch, "E1093.MirrorCS", {"start": v(98.02, 83.67) * mm, "end": v(95.71, 83.67) * mm});
            skLineSegment(sketch, "E1094.MirrorCS", {"start": v(98.02, 70.97) * mm, "end": v(95.71, 70.97) * mm});
            skLineSegment(sketch, "E1095.MirrorCS", {"start": v(113.03, 79.04) * mm, "end": v(108.41, 79.04) * mm});
            skLineSegment(sketch, "E1096.MirrorCS", {"start": v(102.06, 153.52) * mm, "end": v(106.68, 153.52) * mm});
            skLineSegment(sketch, "E1097.MirrorCS", {"start": v(113.03, 66.34) * mm, "end": v(108.41, 66.34) * mm});
            skLineSegment(sketch, "E1098.MirrorCS", {"start": v(189.23, 121.77) * mm, "end": v(189.23, 117.15) * mm});
            skLineSegment(sketch, "E1099.MirrorCS", {"start": v(127.46, 13.82) * mm, "end": v(132.08, 13.82) * mm});
            skLineSegment(sketch, "E1100.MirrorCS", {"start": v(95.71, 117.15) * mm, "end": v(95.71, 121.77) * mm});
            skLineSegment(sketch, "E1101.MirrorCS", {"start": v(102.06, 110.8) * mm, "end": v(102.06, 115.42) * mm});
            skLineSegment(sketch, "E1102.MirrorCS", {"start": v(121.11, 142.55) * mm, "end": v(121.11, 147.17) * mm});
            skLineSegment(sketch, "E1103.MirrorCS", {"start": v(121.11, 134.47) * mm, "end": v(125.73, 134.47) * mm});
            skLineSegment(sketch, "E1104.MirrorCS", {"start": v(140.16, 77.32) * mm, "end": v(140.16, 72.7) * mm});
            skLineSegment(sketch, "E1105.MirrorCS", {"start": v(127.46, 128.12) * mm, "end": v(132.08, 128.12) * mm});
            skLineSegment(sketch, "E1106.MirrorCS", {"start": v(157.48, 26.52) * mm, "end": v(157.48, 21.9) * mm});
            skLineSegment(sketch, "E1107.MirrorCS", {"start": v(144.78, 77.32) * mm, "end": v(140.16, 77.32) * mm});
            skLineSegment(sketch, "E1108.MirrorCS", {"start": v(146.51, 172.57) * mm, "end": v(151.13, 172.57) * mm});
            skLineSegment(sketch, "E1109.MirrorCS", {"start": v(133.81, 40.94) * mm, "end": v(133.81, 45.57) * mm});
            skLineSegment(sketch, "E1110.MirrorCS", {"start": v(144.78, 115.42) * mm, "end": v(140.16, 115.42) * mm});
            skLineSegment(sketch, "E1111.MirrorCS", {"start": v(138.43, 109.07) * mm, "end": v(133.81, 109.07) * mm});
            skLineSegment(sketch, "E1112.MirrorCS", {"start": v(144.78, 102.72) * mm, "end": v(140.16, 102.72) * mm});
            skLineSegment(sketch, "E1113.MirrorCS", {"start": v(100.33, 15.54) * mm, "end": v(100.33, 20.17) * mm});
            skLineSegment(sketch, "E1114.MirrorCS", {"start": v(140.16, 64.62) * mm, "end": v(140.16, 60) * mm});
            skLineSegment(sketch, "E1115.MirrorCS", {"start": v(119.38, 34.6) * mm, "end": v(114.76, 34.6) * mm});
            skLineSegment(sketch, "E1116.MirrorCS", {"start": v(127.46, 123.5) * mm, "end": v(127.46, 128.12) * mm});
            skLineSegment(sketch, "E1117.MirrorCS", {"start": v(108.41, 121.77) * mm, "end": v(108.41, 117.15) * mm});
            skLineSegment(sketch, "E1118.MirrorCS", {"start": v(138.43, 147.17) * mm, "end": v(133.81, 147.17) * mm});
            skLineSegment(sketch, "E1119.MirrorCS", {"start": v(127.46, 26.52) * mm, "end": v(127.46, 21.9) * mm});
            skLineSegment(sketch, "E1120.MirrorCS", {"start": v(163.83, 134.47) * mm, "end": v(163.83, 129.85) * mm});
            skLineSegment(sketch, "E1121.MirrorCS", {"start": v(189.23, 70.97) * mm, "end": v(186.92, 70.97) * mm});
            skLineSegment(sketch, "E1122.MirrorCS", {"start": v(138.43, 53.64) * mm, "end": v(138.43, 58.27) * mm});
            skLineSegment(sketch, "E1123.MirrorCS", {"start": v(95.71, 15.54) * mm, "end": v(100.33, 15.54) * mm});
            skLineSegment(sketch, "E1124.MirrorCS", {"start": v(136.12, 83.67) * mm, "end": v(133.81, 83.67) * mm});
            skLineSegment(sketch, "E1125.MirrorCS", {"start": v(178.26, 128.12) * mm, "end": v(182.88, 128.12) * mm});
            skLineSegment(sketch, "E1126.MirrorCS", {"start": v(189.23, 79.04) * mm, "end": v(189.23, 83.67) * mm});
            skLineSegment(sketch, "E1127.MirrorCS", {"start": v(127.46, 13.82) * mm, "end": v(127.46, 9.2) * mm});
            skLineSegment(sketch, "E1128.MirrorCS", {"start": v(119.38, 98.1) * mm, "end": v(119.38, 102.72) * mm});
            skLineSegment(sketch, "E1129.MirrorCS", {"start": v(102.06, 72.7) * mm, "end": v(106.68, 72.7) * mm});
            skLineSegment(sketch, "E1130.MirrorCS", {"start": v(144.78, 64.62) * mm, "end": v(140.16, 64.62) * mm});
            skLineSegment(sketch, "E1131.MirrorCS", {"start": v(108.41, 134.47) * mm, "end": v(108.41, 129.85) * mm});
            skLineSegment(sketch, "E1132.MirrorCS", {"start": v(133.81, 53.64) * mm, "end": v(133.81, 58.27) * mm});
            skLineSegment(sketch, "E1133.MirrorCS", {"start": v(121.11, 45.57) * mm, "end": v(121.11, 40.94) * mm});
            skLineSegment(sketch, "E1134.MirrorCS", {"start": v(136.12, 70.97) * mm, "end": v(133.81, 70.97) * mm});
            skLineSegment(sketch, "E1135.MirrorCS", {"start": v(133.81, 28.24) * mm, "end": v(133.81, 32.87) * mm});
            skLineSegment(sketch, "E1136.MirrorCS", {"start": v(157.48, 39.22) * mm, "end": v(157.48, 34.6) * mm});
            skLineSegment(sketch, "E1137.MirrorCS", {"start": v(151.13, 40.94) * mm, "end": v(151.13, 45.57) * mm});
            skLineSegment(sketch, "E1138.MirrorCS", {"start": v(100.33, 172.57) * mm, "end": v(100.33, 167.95) * mm});
            skLineSegment(sketch, "E1139.MirrorCS", {"start": v(127.46, 110.8) * mm, "end": v(127.46, 115.42) * mm});
            skLineSegment(sketch, "E1140.MirrorCS", {"start": v(100.33, 159.87) * mm, "end": v(100.33, 155.25) * mm});
            skLineSegment(sketch, "E1141.MirrorCS", {"start": v(151.13, 172.57) * mm, "end": v(151.13, 167.95) * mm});
            skLineSegment(sketch, "E1142.MirrorCS", {"start": v(121.11, 104.45) * mm, "end": v(121.11, 109.07) * mm});
            skLineSegment(sketch, "E1143.MirrorCS", {"start": v(189.23, 53.64) * mm, "end": v(189.23, 58.27) * mm});
            skLineSegment(sketch, "E1144.MirrorCS", {"start": v(114.76, 110.8) * mm, "end": v(114.76, 115.42) * mm});
            skLineSegment(sketch, "E1145.MirrorCS", {"start": v(108.41, 53.64) * mm, "end": v(108.41, 58.27) * mm});
            skLineSegment(sketch, "E1146.MirrorCS", {"start": v(123.42, 7.47) * mm, "end": v(121.11, 7.47) * mm});
            skLineSegment(sketch, "E1147.MirrorCS", {"start": v(144.78, 64.62) * mm, "end": v(144.78, 60) * mm});
            skLineSegment(sketch, "E1148.MirrorCS", {"start": v(182.88, 64.62) * mm, "end": v(182.88, 60) * mm});
            skLineSegment(sketch, "E1149.MirrorCS", {"start": v(151.13, 15.54) * mm, "end": v(151.13, 20.17) * mm});
            skLineSegment(sketch, "E1150.MirrorCS", {"start": v(119.38, 161.6) * mm, "end": v(119.38, 166.22) * mm});
            skLineSegment(sketch, "E1151.MirrorCS", {"start": v(95.71, 129.85) * mm, "end": v(95.71, 134.47) * mm});
            skLineSegment(sketch, "E1152.MirrorCS", {"start": v(138.43, 121.77) * mm, "end": v(133.81, 121.77) * mm});
            skLineSegment(sketch, "E1153.MirrorCS", {"start": v(114.76, 123.5) * mm, "end": v(114.76, 128.12) * mm});
            skLineSegment(sketch, "E1154.MirrorCS", {"start": v(140.16, 98.1) * mm, "end": v(140.16, 102.72) * mm});
            skLineSegment(sketch, "E1155.MirrorCS", {"start": v(157.48, 136.2) * mm, "end": v(157.48, 140.82) * mm});
            skLineSegment(sketch, "E1156.MirrorCS", {"start": v(170.18, 148.9) * mm, "end": v(170.18, 153.52) * mm});
            skLineSegment(sketch, "E1157.MirrorCS", {"start": v(113.03, 159.87) * mm, "end": v(108.41, 159.87) * mm});
            skLineSegment(sketch, "E1158.MirrorCS", {"start": v(152.86, 166.22) * mm, "end": v(157.48, 166.22) * mm});
            skLineSegment(sketch, "E1159.MirrorCS", {"start": v(140.16, 148.9) * mm, "end": v(140.16, 153.52) * mm});
            skLineSegment(sketch, "E1160.MirrorCS", {"start": v(127.46, 161.6) * mm, "end": v(132.08, 161.6) * mm});
            skLineSegment(sketch, "E1161.MirrorCS", {"start": v(189.23, 109.07) * mm, "end": v(189.23, 104.45) * mm});
            skLineSegment(sketch, "E1162.MirrorCS", {"start": v(100.33, 134.47) * mm, "end": v(100.33, 129.85) * mm});
            skLineSegment(sketch, "E1163.MirrorCS", {"start": v(108.41, 2.84) * mm, "end": v(108.41, 7.47) * mm});
            skLineSegment(sketch, "E1164.MirrorCS", {"start": v(133.81, 147.17) * mm, "end": v(133.81, 142.55) * mm});
            skLineSegment(sketch, "E1165.MirrorCS", {"start": v(119.38, 39.22) * mm, "end": v(119.38, 34.6) * mm});
            skLineSegment(sketch, "E1166.MirrorCS", {"start": v(144.78, 98.1) * mm, "end": v(144.78, 102.72) * mm});
            skLineSegment(sketch, "E1167.MirrorCS", {"start": v(127.46, 136.2) * mm, "end": v(127.46, 140.82) * mm});
            skLineSegment(sketch, "E1168.MirrorCS", {"start": v(170.18, 26.52) * mm, "end": v(165.56, 26.52) * mm});
            skLineSegment(sketch, "E1169.MirrorCS", {"start": v(119.38, 115.42) * mm, "end": v(114.76, 115.42) * mm});
            skLineSegment(sketch, "E1170.MirrorCS", {"start": v(144.78, 26.52) * mm, "end": v(140.16, 26.52) * mm});
            skLineSegment(sketch, "E1171.MirrorCS", {"start": v(110.72, 20.17) * mm, "end": v(108.41, 20.17) * mm});
            skLineSegment(sketch, "E1172.MirrorCS", {"start": v(151.13, 147.17) * mm, "end": v(151.13, 142.55) * mm});
            skLineSegment(sketch, "E1173.MirrorCS", {"start": v(182.88, 39.22) * mm, "end": v(182.88, 34.6) * mm});
            skLineSegment(sketch, "E1174.MirrorCS", {"start": v(102.06, 102.72) * mm, "end": v(106.68, 102.72) * mm});
            skLineSegment(sketch, "E1175.MirrorCS", {"start": v(113.03, 15.54) * mm, "end": v(108.41, 15.54) * mm});
            skLineSegment(sketch, "E1176.MirrorCS", {"start": v(163.83, 15.54) * mm, "end": v(159.21, 15.54) * mm});
            skLineSegment(sketch, "E1177.MirrorCS", {"start": v(146.51, 129.85) * mm, "end": v(146.51, 134.47) * mm});
            skLineSegment(sketch, "E1178.MirrorCS", {"start": v(102.06, 21.9) * mm, "end": v(106.68, 21.9) * mm});
            skLineSegment(sketch, "E1179.MirrorCS", {"start": v(132.08, 13.82) * mm, "end": v(132.08, 9.2) * mm});
            skLineSegment(sketch, "E1180.MirrorCS", {"start": v(106.68, 98.1) * mm, "end": v(106.68, 102.72) * mm});
            skLineSegment(sketch, "E1181.MirrorCS", {"start": v(144.78, 34.6) * mm, "end": v(140.16, 34.6) * mm});
            skLineSegment(sketch, "E1182.MirrorCS", {"start": v(125.73, 96.37) * mm, "end": v(125.73, 91.75) * mm});
            skLineSegment(sketch, "E1183.MirrorCS", {"start": v(140.16, 136.2) * mm, "end": v(140.16, 140.82) * mm});
            skLineSegment(sketch, "E1184.MirrorCS", {"start": v(98.02, 7.47) * mm, "end": v(95.71, 7.47) * mm});
            skLineSegment(sketch, "E1185.MirrorCS", {"start": v(159.21, 40.94) * mm, "end": v(159.21, 45.57) * mm});
            skLineSegment(sketch, "E1186.MirrorCS", {"start": v(95.71, 147.17) * mm, "end": v(100.33, 147.17) * mm});
            skLineSegment(sketch, "E1187.MirrorCS", {"start": v(108.41, 109.07) * mm, "end": v(108.41, 104.45) * mm});
            skLineSegment(sketch, "E1188.MirrorCS", {"start": v(144.78, 123.5) * mm, "end": v(140.16, 123.5) * mm});
            skLineSegment(sketch, "E1189.MirrorCS", {"start": v(121.11, 167.95) * mm, "end": v(121.11, 172.57) * mm});
            skLineSegment(sketch, "E1190.MirrorCS", {"start": v(144.78, 110.8) * mm, "end": v(140.16, 110.8) * mm});
            skLineSegment(sketch, "E1191.MirrorCS", {"start": v(148.82, 104.45) * mm, "end": v(146.51, 104.45) * mm});
            skLineSegment(sketch, "E1192.MirrorCS", {"start": v(144.78, 51.92) * mm, "end": v(144.78, 47.3) * mm});
            skLineSegment(sketch, "E1193.MirrorCS", {"start": v(171.91, 40.94) * mm, "end": v(176.53, 40.94) * mm});
            skLineSegment(sketch, "E1194.MirrorCS", {"start": v(127.46, 21.9) * mm, "end": v(132.08, 21.9) * mm});
            skLineSegment(sketch, "E1195.MirrorCS", {"start": v(138.43, 83.67) * mm, "end": v(136.12, 83.67) * mm});
            skLineSegment(sketch, "E1196.MirrorCS", {"start": v(102.06, 77.32) * mm, "end": v(102.06, 72.7) * mm});
            skLineSegment(sketch, "E1197.MirrorCS", {"start": v(106.68, 39.22) * mm, "end": v(106.68, 34.6) * mm});
            skLineSegment(sketch, "E1198.MirrorCS", {"start": v(146.51, 147.17) * mm, "end": v(151.13, 147.17) * mm});
            skLineSegment(sketch, "E1199.MirrorCS", {"start": v(146.51, 96.37) * mm, "end": v(151.13, 96.37) * mm});
            skLineSegment(sketch, "E1200.MirrorCS", {"start": v(132.08, 39.22) * mm, "end": v(132.08, 34.6) * mm});
            skLineSegment(sketch, "E1201.MirrorCS", {"start": v(138.43, 70.97) * mm, "end": v(136.12, 70.97) * mm});
            skLineSegment(sketch, "E1202.MirrorCS", {"start": v(119.38, 72.7) * mm, "end": v(114.76, 72.7) * mm});
            skLineSegment(sketch, "E1203.MirrorCS", {"start": v(119.38, 60) * mm, "end": v(114.76, 60) * mm});
            skPoint(sketch, "E1204.MirrorP", {"position": v(129.77, 87.7) * mm});
            skLineSegment(sketch, "E1205.MirrorCS", {"start": v(138.43, 66.34) * mm, "end": v(138.43, 70.97) * mm});
            skLineSegment(sketch, "E1206.MirrorCS", {"start": v(102.06, 161.6) * mm, "end": v(106.68, 161.6) * mm});
            skLineSegment(sketch, "E1207.MirrorCS", {"start": v(119.38, 123.5) * mm, "end": v(119.38, 128.12) * mm});
            skLineSegment(sketch, "E1208.MirrorCS", {"start": v(144.78, 39.22) * mm, "end": v(140.16, 39.22) * mm});
            skLineSegment(sketch, "E1209.MirrorCS", {"start": v(106.68, 64.62) * mm, "end": v(106.68, 60) * mm});
            skLineSegment(sketch, "E1210.MirrorCS", {"start": v(127.46, 39.22) * mm, "end": v(132.08, 39.22) * mm});
            skLineSegment(sketch, "E1211.MirrorCS", {"start": v(95.71, 45.57) * mm, "end": v(95.71, 40.94) * mm});
            skLineSegment(sketch, "E1212.MirrorCS", {"start": v(113.03, 2.84) * mm, "end": v(113.03, 7.47) * mm});
            skLineSegment(sketch, "E1213.MirrorCS", {"start": v(182.88, 51.92) * mm, "end": v(182.88, 47.3) * mm});
            skLineSegment(sketch, "E1214.MirrorCS", {"start": v(146.51, 45.57) * mm, "end": v(146.51, 40.94) * mm});
            skLineSegment(sketch, "E1215.MirrorCS", {"start": v(127.46, 51.92) * mm, "end": v(127.46, 47.3) * mm});
            skLineSegment(sketch, "E1216.MirrorCS", {"start": v(144.78, 21.9) * mm, "end": v(140.16, 21.9) * mm});
            skLineSegment(sketch, "E1217.MirrorCS", {"start": v(163.83, 28.24) * mm, "end": v(163.83, 32.87) * mm});
            skLineSegment(sketch, "E1218.MirrorCS", {"start": v(165.56, 39.22) * mm, "end": v(165.56, 34.6) * mm});
            skLineSegment(sketch, "E1219.MirrorCS", {"start": v(138.43, 159.87) * mm, "end": v(133.81, 159.87) * mm});
            skLineSegment(sketch, "E1220.MirrorCS", {"start": v(176.53, 147.17) * mm, "end": v(176.53, 142.55) * mm});
            skLineSegment(sketch, "E1221.MirrorCS", {"start": v(133.81, 79.04) * mm, "end": v(133.81, 83.67) * mm});
            skLineSegment(sketch, "E1222.MirrorCS", {"start": v(146.51, 134.47) * mm, "end": v(151.13, 134.47) * mm});
            skLineSegment(sketch, "E1223.MirrorCS", {"start": v(102.06, 13.82) * mm, "end": v(106.68, 13.82) * mm});
            skLineSegment(sketch, "E1224.MirrorCS", {"start": v(146.51, 20.17) * mm, "end": v(146.51, 15.54) * mm});
            skLineSegment(sketch, "E1225.MirrorCS", {"start": v(95.71, 167.95) * mm, "end": v(95.71, 172.57) * mm});
            skLineSegment(sketch, "E1226.MirrorCS", {"start": v(98.02, 32.87) * mm, "end": v(95.71, 32.87) * mm});
            skLineSegment(sketch, "E1227.MirrorCS", {"start": v(102.06, 26.52) * mm, "end": v(102.06, 21.9) * mm});
            skLineSegment(sketch, "E1228.MirrorCS", {"start": v(144.78, 136.2) * mm, "end": v(144.78, 140.82) * mm});
            skLineSegment(sketch, "E1229.MirrorCS", {"start": v(119.38, 26.52) * mm, "end": v(114.76, 26.52) * mm});
            skLineSegment(sketch, "E1230.MirrorCS", {"start": v(113.03, 147.17) * mm, "end": v(108.41, 147.17) * mm});
            skLineSegment(sketch, "E1231.MirrorCS", {"start": v(127.46, 98.1) * mm, "end": v(127.46, 102.72) * mm});
            skLineSegment(sketch, "E1232.MirrorCS", {"start": v(163.83, 159.87) * mm, "end": v(159.21, 159.87) * mm});
            skLineSegment(sketch, "E1233.MirrorCS", {"start": v(119.38, 136.2) * mm, "end": v(114.76, 136.2) * mm});
            skLineSegment(sketch, "E1234.MirrorCS", {"start": v(138.43, 172.57) * mm, "end": v(133.81, 172.57) * mm});
            skLineSegment(sketch, "E1235.MirrorCS", {"start": v(138.43, 134.47) * mm, "end": v(138.43, 129.85) * mm});
            skLineSegment(sketch, "E1236.MirrorCS", {"start": v(144.78, 136.2) * mm, "end": v(140.16, 136.2) * mm});
            skLineSegment(sketch, "E1237.MirrorCS", {"start": v(127.46, 148.9) * mm, "end": v(127.46, 153.52) * mm});
            skLineSegment(sketch, "E1238.MirrorCS", {"start": v(114.76, 98.1) * mm, "end": v(114.76, 102.72) * mm});
            skLineSegment(sketch, "E1239.MirrorCS", {"start": v(119.38, 123.5) * mm, "end": v(114.76, 123.5) * mm});
            skLineSegment(sketch, "E1240.MirrorCS", {"start": v(113.03, 134.47) * mm, "end": v(113.03, 129.85) * mm});
            skLineSegment(sketch, "E1241.MirrorCS", {"start": v(138.43, 79.04) * mm, "end": v(133.81, 79.04) * mm});
            skLineSegment(sketch, "E1242.MirrorCS", {"start": v(123.42, 70.97) * mm, "end": v(121.11, 70.97) * mm});
            skLineSegment(sketch, "E1243.MirrorCS", {"start": v(106.68, 161.6) * mm, "end": v(106.68, 166.22) * mm});
            skLineSegment(sketch, "E1244.MirrorCS", {"start": v(106.68, 13.82) * mm, "end": v(106.68, 9.2) * mm});
            skPoint(sketch, "E1245.MirrorP", {"position": v(104.37, 163.91) * mm});
            skPoint(sketch, "E1246.MirrorP", {"position": v(129.77, 138.51) * mm});
            skPoint(sketch, "E1247.MirrorP", {"position": v(155.17, 163.91) * mm});
            skPoint(sketch, "E1248.MirrorP", {"position": v(117.07, 87.71) * mm});
            skPoint(sketch, "E1249.MirrorP", {"position": v(142.47, 87.71) * mm});
            skPoint(sketch, "E1250.MirrorP", {"position": v(129.77, 163.91) * mm});
            skPoint(sketch, "E1251.MirrorP", {"position": v(104.37, 75) * mm});
            skPoint(sketch, "E1252.MirrorP", {"position": v(104.37, 151.21) * mm});
            skPoint(sketch, "E1253.MirrorP", {"position": v(104.37, 87.7) * mm});
            skPoint(sketch, "E1254.MirrorP", {"position": v(129.77, 87.71) * mm});
            skPoint(sketch, "E1255.MirrorP", {"position": v(104.37, 109.07) * mm});
            skPoint(sketch, "E1256.MirrorP", {"position": v(155.17, 167.95) * mm});
            skPoint(sketch, "E1257.MirrorP", {"position": v(155.17, 155.25) * mm});
            skPoint(sketch, "E1258.MirrorP", {"position": v(104.37, 167.95) * mm});
            skPoint(sketch, "E1259.MirrorP", {"position": v(104.37, 155.25) * mm});
            skPoint(sketch, "E1260.MirrorP", {"position": v(104.37, 104.45) * mm});
            skPoint(sketch, "E1261.MirrorP", {"position": v(181.73, 48.86) * mm});
            skPoint(sketch, "E1262.MirrorP", {"position": v(104.37, 70.97) * mm});
            skPoint(sketch, "E1263.MirrorP", {"position": v(129.77, 91.75) * mm});
            skPoint(sketch, "E1264.MirrorP", {"position": v(104.37, 121.77) * mm});
            skPoint(sketch, "E1265.MirrorP", {"position": v(117.07, 100.41) * mm});
            skPoint(sketch, "E1266.MirrorP", {"position": v(129.77, 129.85) * mm});
            skPoint(sketch, "E1267.MirrorP", {"position": v(129.77, 96.37) * mm});
            skPoint(sketch, "E1268.MirrorP", {"position": v(104.37, 96.37) * mm});
            skPoint(sketch, "E1269.MirrorP", {"position": v(104.37, 20.17) * mm});
            skPoint(sketch, "E1270.MirrorP", {"position": v(117.07, 11.5) * mm});
            skPoint(sketch, "E1271.MirrorP", {"position": v(129.77, 62.3) * mm});
            skPoint(sketch, "E1272.MirrorP", {"position": v(129.77, 117.15) * mm});
            skPoint(sketch, "E1273.MirrorP", {"position": v(104.37, 7.47) * mm});
            skPoint(sketch, "E1274.MirrorP", {"position": v(104.37, 129.85) * mm});
            skPoint(sketch, "E1275.MirrorP", {"position": v(104.37, 113.11) * mm});
            skLineSegment(sketch, "E1276.MirrorCS", {"start": v(98.02, 0) * mm, "end": v(155.17, 0) * mm});
            skPoint(sketch, "E1277.MirrorP", {"position": v(142.47, 62.3) * mm});
            skPoint(sketch, "E1278.MirrorP", {"position": v(104.37, 11.5) * mm});
            skLineSegment(sketch, "E1279.MirrorCS", {"start": v(155.17, 175.42) * mm, "end": v(199.42, 130.56) * mm});
            skPoint(sketch, "E1280.MirrorP", {"position": v(142.47, 36.9) * mm});
            skPoint(sketch, "E1281.MirrorP", {"position": v(104.37, 79.04) * mm});
            skPoint(sketch, "E1282.MirrorP", {"position": v(155.17, 142.55) * mm});
            skPoint(sketch, "E1283.MirrorP", {"position": v(180.57, 129.85) * mm});
            skPoint(sketch, "E1284.MirrorP", {"position": v(142.47, 49.6) * mm});
            skPoint(sketch, "E1285.MirrorP", {"position": v(155.17, 36.9) * mm});
            skLineSegment(sketch, "E1286.MirrorCS", {"start": v(155.17, 0) * mm, "end": v(199.42, 44.86) * mm});
            skPoint(sketch, "E1287.MirrorP", {"position": v(104.37, 66.34) * mm});
            skPoint(sketch, "E1288.MirrorP", {"position": v(155.17, 20.17) * mm});
            skPoint(sketch, "E1289.MirrorP", {"position": v(129.77, 66.34) * mm});
            skPoint(sketch, "E1290.MirrorP", {"position": v(104.37, 36.9) * mm});
            skPoint(sketch, "E1291.MirrorP", {"position": v(104.37, 15.54) * mm});
            skPoint(sketch, "E1292.MirrorP", {"position": v(180.57, 40.94) * mm});
            skLineSegment(sketch, "E1293.MirrorCS", {"start": v(98.02, 175.42) * mm, "end": v(155.17, 175.42) * mm});
            skPoint(sketch, "E1294.MirrorP", {"position": v(155.17, 147.17) * mm});
            skPoint(sketch, "E1295.MirrorP", {"position": v(104.37, 91.75) * mm});
            skPoint(sketch, "E1296.MirrorP", {"position": v(117.07, 151.21) * mm});
            skPoint(sketch, "E1297.MirrorP", {"position": v(142.47, 87.7) * mm});
            skPoint(sketch, "E1298.MirrorP", {"position": v(129.77, 7.47) * mm});
            skPoint(sketch, "E1299.MirrorP", {"position": v(129.77, 151.21) * mm});
            skPoint(sketch, "E1300.MirrorP", {"position": v(117.07, 125.81) * mm});
            skPoint(sketch, "E1301.MirrorP", {"position": v(117.07, 62.3) * mm});
            skPoint(sketch, "E1302.MirrorP", {"position": v(117.07, 49.6) * mm});
            skPoint(sketch, "E1303.MirrorP", {"position": v(104.37, 138.51) * mm});
            skPoint(sketch, "E1304.MirrorP", {"position": v(104.37, 117.15) * mm});
            skPoint(sketch, "E1305.MirrorP", {"position": v(142.47, 113.11) * mm});
            skPoint(sketch, "E1306.MirrorP", {"position": v(142.47, 138.51) * mm});
            skPoint(sketch, "E1307.MirrorP", {"position": v(155.17, 138.51) * mm});
            skPoint(sketch, "E1308.MirrorP", {"position": v(117.07, 163.91) * mm});
            skPoint(sketch, "E1309.MirrorP", {"position": v(104.37, 142.55) * mm});
            skPoint(sketch, "E1310.MirrorP", {"position": v(155.17, 151.21) * mm});
            skPoint(sketch, "E1311.MirrorP", {"position": v(129.77, 104.45) * mm});
            skPoint(sketch, "E1312.MirrorP", {"position": v(104.37, 28.24) * mm});
            skPoint(sketch, "E1313.MirrorP", {"position": v(104.37, 58.27) * mm});
            skPoint(sketch, "E1314.MirrorP", {"position": v(104.37, 45.57) * mm});
            skPoint(sketch, "E1315.MirrorP", {"position": v(142.47, 11.5) * mm});
            skPoint(sketch, "E1316.MirrorP", {"position": v(129.77, 28.24) * mm});
            skPoint(sketch, "E1317.MirrorP", {"position": v(129.77, 11.5) * mm});
            skPoint(sketch, "E1318.MirrorP", {"position": v(129.77, 40.94) * mm});
            skPoint(sketch, "E1319.MirrorP", {"position": v(180.57, 36.9) * mm});
            skPoint(sketch, "E1320.MirrorP", {"position": v(117.07, 24.2) * mm});
            skPoint(sketch, "E1321.MirrorP", {"position": v(155.17, 32.87) * mm});
            skPoint(sketch, "E1322.MirrorP", {"position": v(129.77, 36.9) * mm});
            skPoint(sketch, "E1323.MirrorP", {"position": v(142.47, 24.2) * mm});
            skPoint(sketch, "E1324.MirrorP", {"position": v(129.77, 100.41) * mm});
            skPoint(sketch, "E1325.MirrorP", {"position": v(142.47, 75) * mm});
            skPoint(sketch, "E1326.MirrorP", {"position": v(129.77, 167.95) * mm});
            skPoint(sketch, "E1327.MirrorP", {"position": v(180.57, 134.47) * mm});
            skPoint(sketch, "E1328.MirrorP", {"position": v(142.47, 163.91) * mm});
            skPoint(sketch, "E1329.MirrorP", {"position": v(129.77, 147.17) * mm});
            skPoint(sketch, "E1330.MirrorP", {"position": v(104.37, 159.87) * mm});
            skPoint(sketch, "E1331.MirrorP", {"position": v(129.77, 134.47) * mm});
            skPoint(sketch, "E1332.MirrorP", {"position": v(129.77, 142.55) * mm});
            skPoint(sketch, "E1333.MirrorP", {"position": v(142.47, 151.21) * mm});
            skPoint(sketch, "E1334.MirrorP", {"position": v(142.47, 125.81) * mm});
            skPoint(sketch, "E1335.MirrorP", {"position": v(129.77, 58.27) * mm});
            skPoint(sketch, "E1336.MirrorP", {"position": v(129.77, 15.54) * mm});
            skPoint(sketch, "E1337.MirrorP", {"position": v(129.77, 45.57) * mm});
            skPoint(sketch, "E1338.MirrorP", {"position": v(155.17, 129.85) * mm});
            skPoint(sketch, "E1339.MirrorP", {"position": v(180.57, 45.57) * mm});
            skPoint(sketch, "E1340.MirrorP", {"position": v(117.07, 36.9) * mm});
            skPoint(sketch, "E1341.MirrorP", {"position": v(129.77, 155.25) * mm});
            skPoint(sketch, "E1342.MirrorP", {"position": v(104.37, 83.67) * mm});
            skPoint(sketch, "E1343.MirrorP", {"position": v(129.77, 70.97) * mm});
            skPoint(sketch, "E1344.MirrorP", {"position": v(129.77, 109.07) * mm});
            skPoint(sketch, "E1345.MirrorP", {"position": v(180.57, 138.51) * mm});
            skPoint(sketch, "E1346.MirrorP", {"position": v(117.07, 75) * mm});
            skPoint(sketch, "E1347.MirrorP", {"position": v(117.07, 87.7) * mm});
            skPoint(sketch, "E1348.MirrorP", {"position": v(142.47, 100.41) * mm});
            skPoint(sketch, "E1349.MirrorP", {"position": v(104.37, 134.47) * mm});
            skPoint(sketch, "E1350.MirrorP", {"position": v(104.37, 62.3) * mm});
            skPoint(sketch, "E1351.MirrorP", {"position": v(129.77, 159.87) * mm});
            skPoint(sketch, "E1352.MirrorP", {"position": v(104.37, 147.17) * mm});
            skPoint(sketch, "E1353.MirrorP", {"position": v(117.07, 138.51) * mm});
            skPoint(sketch, "E1354.MirrorP", {"position": v(104.37, 100.41) * mm});
            skPoint(sketch, "E1355.MirrorP", {"position": v(129.77, 121.77) * mm});
            skPoint(sketch, "E1356.MirrorP", {"position": v(104.37, 49.6) * mm});
            skPoint(sketch, "E1357.MirrorP", {"position": v(129.77, 53.64) * mm});
            skPoint(sketch, "E1358.MirrorP", {"position": v(155.17, 11.5) * mm});
            skPoint(sketch, "E1359.MirrorP", {"position": v(129.77, 20.17) * mm});
            skPoint(sketch, "E1360.MirrorP", {"position": v(155.17, 15.54) * mm});
            skPoint(sketch, "E1361.MirrorP", {"position": v(104.37, 24.2) * mm});
            skPoint(sketch, "E1362.MirrorP", {"position": v(129.77, 113.11) * mm});
            skPoint(sketch, "E1363.MirrorP", {"position": v(104.37, 40.94) * mm});
            skPoint(sketch, "E1364.MirrorP", {"position": v(129.77, 24.2) * mm});
            skPoint(sketch, "E1365.MirrorP", {"position": v(155.17, 7.47) * mm});
            skPoint(sketch, "E1366.MirrorP", {"position": v(155.17, 45.57) * mm});
            skPoint(sketch, "E1367.MirrorP", {"position": v(104.37, 53.64) * mm});
            skPoint(sketch, "E1368.MirrorP", {"position": v(117.07, 113.11) * mm});
            skPoint(sketch, "E1369.MirrorP", {"position": v(129.77, 125.81) * mm});
            skPoint(sketch, "E1370.MirrorP", {"position": v(129.77, 32.87) * mm});
            skPoint(sketch, "E1371.MirrorP", {"position": v(129.77, 79.04) * mm});
            skPoint(sketch, "E1372.MirrorP", {"position": v(155.17, 134.47) * mm});
            skPoint(sketch, "E1373.MirrorP", {"position": v(155.17, 40.94) * mm});
            skPoint(sketch, "E1374.MirrorP", {"position": v(129.77, 49.6) * mm});
            skPoint(sketch, "E1375.MirrorP", {"position": v(155.17, 24.2) * mm});
            skPoint(sketch, "E1376.MirrorP", {"position": v(129.77, 83.67) * mm});
            skPoint(sketch, "E1377.MirrorP", {"position": v(129.77, 75) * mm});
            skPoint(sketch, "E1378.MirrorP", {"position": v(104.37, 32.87) * mm});
            skPoint(sketch, "E1379.MirrorP", {"position": v(155.17, 28.24) * mm});
            skPoint(sketch, "E1380.MirrorP", {"position": v(155.17, 159.87) * mm});
            skPoint(sketch, "E1381.MirrorP", {"position": v(104.37, 125.81) * mm});
            skPoint(sketch, "E1382.MirrorP", {"position": v(104.37, 87.71) * mm});
            skLineSegment(sketch, "E1383", {"start": v(-3.37, 125.8) * mm, "end": v(-3.37, 49.6) * mm});
            skLineSegment(sketch, "E1384", {"start": v(199.42, 130.56) * mm, "end": v(199.42, 44.86) * mm});
            skLineSegment(sketch, "E1385.bottom", {"start": v(182.88, 128.12) * mm, "end": v(152.86, 128.12) * mm});
            skLineSegment(sketch, "E1385.top", {"start": v(182.88, 47.3) * mm, "end": v(152.86, 47.3) * mm});
            skLineSegment(sketch, "E1385.left", {"start": v(182.88, 128.12) * mm, "end": v(182.88, 47.3) * mm});
            skLineSegment(sketch, "E1385.right", {"start": v(152.86, 128.12) * mm, "end": v(152.86, 47.3) * mm});
            skSolve(sketch);
        }
        {
            var Q0;
            Q0=makeQuery(id+"F0nU1GUYquLPwz4_0.opExtrude","CAP_FACE",FACE,{"disambiguationData":[OSD([sQuery(id+"F0.wireOp",EDGE,"E2.2.0.0"),sQuery(id+"F0.wireOp",EDGE,"E2.2.0.2"),sQuery(id+"F0.wireOp",EDGE,"E2.2.0.4"),sQuery(id+"F0.wireOp",EDGE,"E2.2.0.7"),sQuery(id+"F0.wireOp",EDGE,"E2.2.0.8"),sQuery(id+"F0.wireOp",EDGE,"E2.2.0.9"),sQuery(id+"F0.wireOp",EDGE,"E2.2.0.11"),sQuery(id+"F0.wireOp",EDGE,"E2.2.0.13"),sQuery(id+"F0.wireOp",EDGE,"E2.2.0.14"),sQuery(id+"F0.wireOp",EDGE,"E2.2.0.15"),sQuery(id+"F0.wireOp",EDGE,"E2.2.0.17"),sQuery(id+"F0.wireOp",EDGE,"E2.2.0.19"),sQuery(id+"F0.wireOp",EDGE,"E2.2.0.20"),sQuery(id+"F0.wireOp",EDGE,"E2.3.0.0"),sQuery(id+"F0.wireOp",EDGE,"E2.3.0.2"),sQuery(id+"F0.wireOp",EDGE,"E2.3.0.4"),sQuery(id+"F0.wireOp",EDGE,"E2.3.0.5"),sQuery(id+"F0.wireOp",EDGE,"E2.3.0.7"),sQuery(id+"F0.wireOp",EDGE,"E2.3.0.8"),sQuery(id+"F0.wireOp",EDGE,"E2.3.0.9"),sQuery(id+"F0.wireOp",EDGE,"E2.3.0.10"),sQuery(id+"F0.wireOp",EDGE,"E2.3.0.11"),sQuery(id+"F0.wireOp",EDGE,"E2.3.0.12"),sQuery(id+"F0.wireOp",EDGE,"E2.3.0.13"),sQuery(id+"F0.wireOp",EDGE,"E2.3.0.14"),sQuery(id+"F0.wireOp",EDGE,"E2.3.0.15"),sQuery(id+"F0.wireOp",EDGE,"E2.3.0.16"),sQuery(id+"F0.wireOp",EDGE,"E2.3.0.17"),sQuery(id+"F0.wireOp",EDGE,"E2.3.0.19"),sQuery(id+"F0.wireOp",EDGE,"E2.3.0.20"),sQuery(id+"F0.wireOp",EDGE,"E2.3.0.21"),sQuery(id+"F0.wireOp",EDGE,"E2.4.0.5"),sQuery(id+"F0.wireOp",EDGE,"E2.4.0.7"),sQuery(id+"F0.wireOp",EDGE,"E2.4.0.10"),sQuery(id+"F0.wireOp",EDGE,"E2.4.0.11"),sQuery(id+"F0.wireOp",EDGE,"E2.4.0.12"),sQuery(id+"F0.wireOp",EDGE,"E2.4.0.13"),sQuery(id+"F0.wireOp",EDGE,"E2.4.0.15"),sQuery(id+"F0.wireOp",EDGE,"E2.4.0.16"),sQuery(id+"F0.wireOp",EDGE,"E2.4.0.21"),sQuery(id+"F0.wireOp",EDGE,"E3.0.1.15"),sQuery(id+"F0.wireOp",EDGE,"E3.0.1.17"),sQuery(id+"F0.wireOp",EDGE,"E3.0.1.19"),sQuery(id+"F0.wireOp",EDGE,"E3.0.1.21"),sQuery(id+"F0.wireOp",EDGE,"E3.0.1.30"),sQuery(id+"F0.wireOp",EDGE,"E3.0.1.46"),sQuery(id+"F0.wireOp",EDGE,"E3.0.1.51"),sQuery(id+"F0.wireOp",EDGE,"E3.0.1.52"),sQuery(id+"F0.wireOp",EDGE,"E3.0.1.58"),sQuery(id+"F0.wireOp",EDGE,"E3.0.1.68"),sQuery(id+"F0.wireOp",EDGE,"E3.0.1.69"),sQuery(id+"F0.wireOp",EDGE,"E3.0.1.82"),sQuery(id+"F0.wireOp",EDGE,"E3.0.1.87"),sQuery(id+"F0.wireOp",EDGE,"E3.0.1.88"),sQuery(id+"F0.wireOp",EDGE,"E3.0.1.93"),sQuery(id+"F0.wireOp",EDGE,"E3.0.1.94"),sQuery(id+"F0.wireOp",EDGE,"E3.0.1.95"),sQuery(id+"F0.wireOp",EDGE,"E3.0.1.99"),sQuery(id+"F0.wireOp",EDGE,"E3.0.1.105"),sQuery(id+"F0.wireOp",EDGE,"E3.0.1.106"),sQuery(id+"F0.wireOp",EDGE,"E3.0.1.109"),sQuery(id+"F0.wireOp",EDGE,"E3.0.1.110"),sQuery(id+"F0.wireOp",EDGE,"E3.0.1.115"),sQuery(id+"F0.wireOp",EDGE,"E3.0.1.116"),sQuery(id+"F0.wireOp",EDGE,"E3.0.1.122"),sQuery(id+"F0.wireOp",EDGE,"E3.0.1.123"),sQuery(id+"F0.wireOp",EDGE,"E3.0.1.124"),sQuery(id+"F0.wireOp",EDGE,"E3.0.1.127"),sQuery(id+"F0.wireOp",EDGE,"E3.0.1.139"),sQuery(id+"F0.wireOp",EDGE,"E3.0.1.141"),sQuery(id+"F0.wireOp",EDGE,"E3.0.1.142"),sQuery(id+"F0.wireOp",EDGE,"E3.0.1.146"),sQuery(id+"F0.wireOp",EDGE,"E3.0.1.151"),sQuery(id+"F0.wireOp",EDGE,"E3.0.1.152"),sQuery(id+"F0.wireOp",EDGE,"E3.0.1.153"),sQuery(id+"F0.wireOp",EDGE,"E3.0.1.154"),sQuery(id+"F0.wireOp",EDGE,"E3.0.1.156"),sQuery(id+"F0.wireOp",EDGE,"E3.0.1.162"),sQuery(id+"F0.wireOp",EDGE,"E3.0.1.163"),sQuery(id+"F0.wireOp",EDGE,"E3.0.1.167"),sQuery(id+"F0.wireOp",EDGE,"E3.0.1.170"),sQuery(id+"F0.wireOp",EDGE,"E3.0.1.171"),sQuery(id+"F0.wireOp",EDGE,"E3.0.1.173"),sQuery(id+"F0.wireOp",EDGE,"E3.0.1.178"),sQuery(id+"F0.wireOp",EDGE,"E3.0.1.182"),sQuery(id+"F0.wireOp",EDGE,"E3.0.1.192"),sQuery(id+"F0.wireOp",EDGE,"E3.0.1.194"),sQuery(id+"F0.wireOp",EDGE,"E3.0.1.208"),sQuery(id+"F0.wireOp",EDGE,"E3.0.1.211"),sQuery(id+"F0.wireOp",EDGE,"E3.0.2.8"),sQuery(id+"F0.wireOp",EDGE,"E3.0.2.15"),sQuery(id+"F0.wireOp",EDGE,"E3.0.2.17"),sQuery(id+"F0.wireOp",EDGE,"E3.0.2.19"),sQuery(id+"F0.wireOp",EDGE,"E3.0.2.21"),sQuery(id+"F0.wireOp",EDGE,"E3.0.2.30"),sQuery(id+"F0.wireOp",EDGE,"E3.0.2.46"),sQuery(id+"F0.wireOp",EDGE,"E3.0.2.51"),sQuery(id+"F0.wireOp",EDGE,"E3.0.2.52"),sQuery(id+"F0.wireOp",EDGE,"E3.0.2.58"),sQuery(id+"F0.wireOp",EDGE,"E3.0.2.68"),sQuery(id+"F0.wireOp",EDGE,"E3.0.2.69"),sQuery(id+"F0.wireOp",EDGE,"E3.0.2.82"),sQuery(id+"F0.wireOp",EDGE,"E3.0.2.83"),sQuery(id+"F0.wireOp",EDGE,"E3.0.2.87"),sQuery(id+"F0.wireOp",EDGE,"E3.0.2.88"),sQuery(id+"F0.wireOp",EDGE,"E3.0.2.93"),sQuery(id+"F0.wireOp",EDGE,"E3.0.2.94"),sQuery(id+"F0.wireOp",EDGE,"E3.0.2.95"),sQuery(id+"F0.wireOp",EDGE,"E3.0.2.99"),sQuery(id+"F0.wireOp",EDGE,"E3.0.2.104"),sQuery(id+"F0.wireOp",EDGE,"E3.0.2.105"),sQuery(id+"F0.wireOp",EDGE,"E3.0.2.106"),sQuery(id+"F0.wireOp",EDGE,"E3.0.2.109"),sQuery(id+"F0.wireOp",EDGE,"E3.0.2.110"),sQuery(id+"F0.wireOp",EDGE,"E3.0.2.115"),sQuery(id+"F0.wireOp",EDGE,"E3.0.2.116"),sQuery(id+"F0.wireOp",EDGE,"E3.0.2.122"),sQuery(id+"F0.wireOp",EDGE,"E3.0.2.123"),sQuery(id+"F0.wireOp",EDGE,"E3.0.2.124"),sQuery(id+"F0.wireOp",EDGE,"E3.0.2.127"),sQuery(id+"F0.wireOp",EDGE,"E3.0.2.128"),sQuery(id+"F0.wireOp",EDGE,"E3.0.2.139"),sQuery(id+"F0.wireOp",EDGE,"E3.0.2.141"),sQuery(id+"F0.wireOp",EDGE,"E3.0.2.142"),sQuery(id+"F0.wireOp",EDGE,"E3.0.2.145"),sQuery(id+"F0.wireOp",EDGE,"E3.0.2.146"),sQuery(id+"F0.wireOp",EDGE,"E3.0.2.151"),sQuery(id+"F0.wireOp",EDGE,"E3.0.2.152"),sQuery(id+"F0.wireOp",EDGE,"E3.0.2.153"),sQuery(id+"F0.wireOp",EDGE,"E3.0.2.154"),sQuery(id+"F0.wireOp",EDGE,"E3.0.2.156"),sQuery(id+"F0.wireOp",EDGE,"E3.0.2.162"),sQuery(id+"F0.wireOp",EDGE,"E3.0.2.163"),sQuery(id+"F0.wireOp",EDGE,"E3.0.2.164"),sQuery(id+"F0.wireOp",EDGE,"E3.0.2.167"),sQuery(id+"F0.wireOp",EDGE,"E3.0.2.170"),sQuery(id+"F0.wireOp",EDGE,"E3.0.2.171"),sQuery(id+"F0.wireOp",EDGE,"E3.0.2.173"),sQuery(id+"F0.wireOp",EDGE,"E3.0.2.175"),sQuery(id+"F0.wireOp",EDGE,"E3.0.2.178"),sQuery(id+"F0.wireOp",EDGE,"E3.0.2.182"),sQuery(id+"F0.wireOp",EDGE,"E3.0.2.190"),sQuery(id+"F0.wireOp",EDGE,"E3.0.2.192"),sQuery(id+"F0.wireOp",EDGE,"E3.0.2.194"),sQuery(id+"F0.wireOp",EDGE,"E3.0.2.208"),sQuery(id+"F0.wireOp",EDGE,"E3.0.2.211"),sQuery(id+"F0.wireOp",EDGE,"E3.0.2.212"),sQuery(id+"F0.wireOp",EDGE,"E3.0.3.8"),sQuery(id+"F0.wireOp",EDGE,"E3.0.3.15"),sQuery(id+"F0.wireOp",EDGE,"E3.0.3.17"),sQuery(id+"F0.wireOp",EDGE,"E3.0.3.19"),sQuery(id+"F0.wireOp",EDGE,"E3.0.3.21"),sQuery(id+"F0.wireOp",EDGE,"E3.0.3.30"),sQuery(id+"F0.wireOp",EDGE,"E3.0.3.35"),sQuery(id+"F0.wireOp",EDGE,"E3.0.3.46"),sQuery(id+"F0.wireOp",EDGE,"E3.0.3.47"),sQuery(id+"F0.wireOp",EDGE,"E3.0.3.51"),sQuery(id+"F0.wireOp",EDGE,"E3.0.3.52"),sQuery(id+"F0.wireOp",EDGE,"E3.0.3.58"),sQuery(id+"F0.wireOp",EDGE,"E3.0.3.68"),sQuery(id+"F0.wireOp",EDGE,"E3.0.3.69"),sQuery(id+"F0.wireOp",EDGE,"E3.0.3.82"),sQuery(id+"F0.wireOp",EDGE,"E3.0.3.83"),sQuery(id+"F0.wireOp",EDGE,"E3.0.3.87"),sQuery(id+"F0.wireOp",EDGE,"E3.0.3.88"),sQuery(id+"F0.wireOp",EDGE,"E3.0.3.93"),sQuery(id+"F0.wireOp",EDGE,"E3.0.3.94"),sQuery(id+"F0.wireOp",EDGE,"E3.0.3.95"),sQuery(id+"F0.wireOp",EDGE,"E3.0.3.99"),sQuery(id+"F0.wireOp",EDGE,"E3.0.3.104"),sQuery(id+"F0.wireOp",EDGE,"E3.0.3.105"),sQuery(id+"F0.wireOp",EDGE,"E3.0.3.106"),sQuery(id+"F0.wireOp",EDGE,"E3.0.3.109"),sQuery(id+"F0.wireOp",EDGE,"E3.0.3.110"),sQuery(id+"F0.wireOp",EDGE,"E3.0.3.115"),sQuery(id+"F0.wireOp",EDGE,"E3.0.3.116"),sQuery(id+"F0.wireOp",EDGE,"E3.0.3.122"),sQuery(id+"F0.wireOp",EDGE,"E3.0.3.123"),sQuery(id+"F0.wireOp",EDGE,"E3.0.3.124"),sQuery(id+"F0.wireOp",EDGE,"E3.0.3.127"),sQuery(id+"F0.wireOp",EDGE,"E3.0.3.128"),sQuery(id+"F0.wireOp",EDGE,"E3.0.3.139"),sQuery(id+"F0.wireOp",EDGE,"E3.0.3.141"),sQuery(id+"F0.wireOp",EDGE,"E3.0.3.142"),sQuery(id+"F0.wireOp",EDGE,"E3.0.3.145"),sQuery(id+"F0.wireOp",EDGE,"E3.0.3.146"),sQuery(id+"F0.wireOp",EDGE,"E3.0.3.147"),sQuery(id+"F0.wireOp",EDGE,"E3.0.3.149"),sQuery(id+"F0.wireOp",EDGE,"E3.0.3.151"),sQuery(id+"F0.wireOp",EDGE,"E3.0.3.152"),sQuery(id+"F0.wireOp",EDGE,"E3.0.3.153"),sQuery(id+"F0.wireOp",EDGE,"E3.0.3.154"),sQuery(id+"F0.wireOp",EDGE,"E3.0.3.156"),sQuery(id+"F0.wireOp",EDGE,"E3.0.3.162"),sQuery(id+"F0.wireOp",EDGE,"E3.0.3.163"),sQuery(id+"F0.wireOp",EDGE,"E3.0.3.164"),sQuery(id+"F0.wireOp",EDGE,"E3.0.3.167"),sQuery(id+"F0.wireOp",EDGE,"E3.0.3.170"),sQuery(id+"F0.wireOp",EDGE,"E3.0.3.171"),sQuery(id+"F0.wireOp",EDGE,"E3.0.3.173"),sQuery(id+"F0.wireOp",EDGE,"E3.0.3.175"),sQuery(id+"F0.wireOp",EDGE,"E3.0.3.178"),sQuery(id+"F0.wireOp",EDGE,"E3.0.3.182"),sQuery(id+"F0.wireOp",EDGE,"E3.0.3.190"),sQuery(id+"F0.wireOp",EDGE,"E3.0.3.192"),sQuery(id+"F0.wireOp",EDGE,"E3.0.3.194"),sQuery(id+"F0.wireOp",EDGE,"E3.0.3.195"),sQuery(id+"F0.wireOp",EDGE,"E3.0.3.208"),sQuery(id+"F0.wireOp",EDGE,"E3.0.3.211"),sQuery(id+"F0.wireOp",EDGE,"E3.0.3.212"),sQuery(id+"F0.wireOp",EDGE,"E3.0.4.8"),sQuery(id+"F0.wireOp",EDGE,"E3.0.4.15"),sQuery(id+"F0.wireOp",EDGE,"E3.0.4.17"),sQuery(id+"F0.wireOp",EDGE,"E3.0.4.19"),sQuery(id+"F0.wireOp",EDGE,"E3.0.4.21"),sQuery(id+"F0.wireOp",EDGE,"E3.0.4.30"),sQuery(id+"F0.wireOp",EDGE,"E3.0.4.35"),sQuery(id+"F0.wireOp",EDGE,"E3.0.4.46"),sQuery(id+"F0.wireOp",EDGE,"E3.0.4.47"),sQuery(id+"F0.wireOp",EDGE,"E3.0.4.51"),sQuery(id+"F0.wireOp",EDGE,"E3.0.4.52"),sQuery(id+"F0.wireOp",EDGE,"E3.0.4.58"),sQuery(id+"F0.wireOp",EDGE,"E3.0.4.68"),sQuery(id+"F0.wireOp",EDGE,"E3.0.4.69"),sQuery(id+"F0.wireOp",EDGE,"E3.0.4.82"),sQuery(id+"F0.wireOp",EDGE,"E3.0.4.83"),sQuery(id+"F0.wireOp",EDGE,"E3.0.4.87"),sQuery(id+"F0.wireOp",EDGE,"E3.0.4.88"),sQuery(id+"F0.wireOp",EDGE,"E3.0.4.93"),sQuery(id+"F0.wireOp",EDGE,"E3.0.4.94"),sQuery(id+"F0.wireOp",EDGE,"E3.0.4.95"),sQuery(id+"F0.wireOp",EDGE,"E3.0.4.99"),sQuery(id+"F0.wireOp",EDGE,"E3.0.4.104"),sQuery(id+"F0.wireOp",EDGE,"E3.0.4.105"),sQuery(id+"F0.wireOp",EDGE,"E3.0.4.106"),sQuery(id+"F0.wireOp",EDGE,"E3.0.4.109"),sQuery(id+"F0.wireOp",EDGE,"E3.0.4.110"),sQuery(id+"F0.wireOp",EDGE,"E3.0.4.115"),sQuery(id+"F0.wireOp",EDGE,"E3.0.4.116"),sQuery(id+"F0.wireOp",EDGE,"E3.0.4.122"),sQuery(id+"F0.wireOp",EDGE,"E3.0.4.123"),sQuery(id+"F0.wireOp",EDGE,"E3.0.4.124"),sQuery(id+"F0.wireOp",EDGE,"E3.0.4.127"),sQuery(id+"F0.wireOp",EDGE,"E3.0.4.128"),sQuery(id+"F0.wireOp",EDGE,"E3.0.4.139"),sQuery(id+"F0.wireOp",EDGE,"E3.0.4.141"),sQuery(id+"F0.wireOp",EDGE,"E3.0.4.142"),sQuery(id+"F0.wireOp",EDGE,"E3.0.4.145"),sQuery(id+"F0.wireOp",EDGE,"E3.0.4.146"),sQuery(id+"F0.wireOp",EDGE,"E3.0.4.147"),sQuery(id+"F0.wireOp",EDGE,"E3.0.4.149"),sQuery(id+"F0.wireOp",EDGE,"E3.0.4.151"),sQuery(id+"F0.wireOp",EDGE,"E3.0.4.152"),sQuery(id+"F0.wireOp",EDGE,"E3.0.4.153"),sQuery(id+"F0.wireOp",EDGE,"E3.0.4.154"),sQuery(id+"F0.wireOp",EDGE,"E3.0.4.156"),sQuery(id+"F0.wireOp",EDGE,"E3.0.4.162"),sQuery(id+"F0.wireOp",EDGE,"E3.0.4.163"),sQuery(id+"F0.wireOp",EDGE,"E3.0.4.164"),sQuery(id+"F0.wireOp",EDGE,"E3.0.4.167"),sQuery(id+"F0.wireOp",EDGE,"E3.0.4.170"),sQuery(id+"F0.wireOp",EDGE,"E3.0.4.171"),sQuery(id+"F0.wireOp",EDGE,"E3.0.4.173"),sQuery(id+"F0.wireOp",EDGE,"E3.0.4.175"),sQuery(id+"F0.wireOp",EDGE,"E3.0.4.178"),sQuery(id+"F0.wireOp",EDGE,"E3.0.4.182"),sQuery(id+"F0.wireOp",EDGE,"E3.0.4.190"),sQuery(id+"F0.wireOp",EDGE,"E3.0.4.192"),sQuery(id+"F0.wireOp",EDGE,"E3.0.4.194"),sQuery(id+"F0.wireOp",EDGE,"E3.0.4.195"),sQuery(id+"F0.wireOp",EDGE,"E3.0.4.208"),sQuery(id+"F0.wireOp",EDGE,"E3.0.4.211"),sQuery(id+"F0.wireOp",EDGE,"E3.0.4.212"),sQuery(id+"F0.wireOp",EDGE,"E3.0.5.8"),sQuery(id+"F0.wireOp",EDGE,"E3.0.5.15"),sQuery(id+"F0.wireOp",EDGE,"E3.0.5.17"),sQuery(id+"F0.wireOp",EDGE,"E3.0.5.19"),sQuery(id+"F0.wireOp",EDGE,"E3.0.5.21"),sQuery(id+"F0.wireOp",EDGE,"E3.0.5.30"),sQuery(id+"F0.wireOp",EDGE,"E3.0.5.35"),sQuery(id+"F0.wireOp",EDGE,"E3.0.5.46"),sQuery(id+"F0.wireOp",EDGE,"E3.0.5.47"),sQuery(id+"F0.wireOp",EDGE,"E3.0.5.51"),sQuery(id+"F0.wireOp",EDGE,"E3.0.5.52"),sQuery(id+"F0.wireOp",EDGE,"E3.0.5.58"),sQuery(id+"F0.wireOp",EDGE,"E3.0.5.68"),sQuery(id+"F0.wireOp",EDGE,"E3.0.5.69"),sQuery(id+"F0.wireOp",EDGE,"E3.0.5.82"),sQuery(id+"F0.wireOp",EDGE,"E3.0.5.83"),sQuery(id+"F0.wireOp",EDGE,"E3.0.5.87"),sQuery(id+"F0.wireOp",EDGE,"E3.0.5.88"),sQuery(id+"F0.wireOp",EDGE,"E3.0.5.93"),sQuery(id+"F0.wireOp",EDGE,"E3.0.5.94"),sQuery(id+"F0.wireOp",EDGE,"E3.0.5.95"),sQuery(id+"F0.wireOp",EDGE,"E3.0.5.99"),sQuery(id+"F0.wireOp",EDGE,"E3.0.5.104"),sQuery(id+"F0.wireOp",EDGE,"E3.0.5.105"),sQuery(id+"F0.wireOp",EDGE,"E3.0.5.106"),sQuery(id+"F0.wireOp",EDGE,"E3.0.5.109"),sQuery(id+"F0.wireOp",EDGE,"E3.0.5.110"),sQuery(id+"F0.wireOp",EDGE,"E3.0.5.115"),sQuery(id+"F0.wireOp",EDGE,"E3.0.5.116"),sQuery(id+"F0.wireOp",EDGE,"E3.0.5.122"),sQuery(id+"F0.wireOp",EDGE,"E3.0.5.123"),sQuery(id+"F0.wireOp",EDGE,"E3.0.5.124"),sQuery(id+"F0.wireOp",EDGE,"E3.0.5.127"),sQuery(id+"F0.wireOp",EDGE,"E3.0.5.128"),sQuery(id+"F0.wireOp",EDGE,"E3.0.5.139"),sQuery(id+"F0.wireOp",EDGE,"E3.0.5.141"),sQuery(id+"F0.wireOp",EDGE,"E3.0.5.142"),sQuery(id+"F0.wireOp",EDGE,"E3.0.5.145"),sQuery(id+"F0.wireOp",EDGE,"E3.0.5.146"),sQuery(id+"F0.wireOp",EDGE,"E3.0.5.147"),sQuery(id+"F0.wireOp",EDGE,"E3.0.5.149"),sQuery(id+"F0.wireOp",EDGE,"E3.0.5.151"),sQuery(id+"F0.wireOp",EDGE,"E3.0.5.152"),sQuery(id+"F0.wireOp",EDGE,"E3.0.5.153"),sQuery(id+"F0.wireOp",EDGE,"E3.0.5.154"),sQuery(id+"F0.wireOp",EDGE,"E3.0.5.156"),sQuery(id+"F0.wireOp",EDGE,"E3.0.5.162"),sQuery(id+"F0.wireOp",EDGE,"E3.0.5.163"),sQuery(id+"F0.wireOp",EDGE,"E3.0.5.164"),sQuery(id+"F0.wireOp",EDGE,"E3.0.5.167"),sQuery(id+"F0.wireOp",EDGE,"E3.0.5.170"),sQuery(id+"F0.wireOp",EDGE,"E3.0.5.171"),sQuery(id+"F0.wireOp",EDGE,"E3.0.5.173"),sQuery(id+"F0.wireOp",EDGE,"E3.0.5.175"),sQuery(id+"F0.wireOp",EDGE,"E3.0.5.178"),sQuery(id+"F0.wireOp",EDGE,"E3.0.5.182"),sQuery(id+"F0.wireOp",EDGE,"E3.0.5.190"),sQuery(id+"F0.wireOp",EDGE,"E3.0.5.192"),sQuery(id+"F0.wireOp",EDGE,"E3.0.5.194"),sQuery(id+"F0.wireOp",EDGE,"E3.0.5.195"),sQuery(id+"F0.wireOp",EDGE,"E3.0.5.208"),sQuery(id+"F0.wireOp",EDGE,"E3.0.5.211"),sQuery(id+"F0.wireOp",EDGE,"E3.0.5.212"),sQuery(id+"F0.wireOp",EDGE,"E3.0.6.8"),sQuery(id+"F0.wireOp",EDGE,"E3.0.6.15"),sQuery(id+"F0.wireOp",EDGE,"E3.0.6.17"),sQuery(id+"F0.wireOp",EDGE,"E3.0.6.19"),sQuery(id+"F0.wireOp",EDGE,"E3.0.6.21"),sQuery(id+"F0.wireOp",EDGE,"E3.0.6.30"),sQuery(id+"F0.wireOp",EDGE,"E3.0.6.35"),sQuery(id+"F0.wireOp",EDGE,"E3.0.6.46"),sQuery(id+"F0.wireOp",EDGE,"E3.0.6.47"),sQuery(id+"F0.wireOp",EDGE,"E3.0.6.51"),sQuery(id+"F0.wireOp",EDGE,"E3.0.6.52"),sQuery(id+"F0.wireOp",EDGE,"E3.0.6.58"),sQuery(id+"F0.wireOp",EDGE,"E3.0.6.68"),sQuery(id+"F0.wireOp",EDGE,"E3.0.6.69"),sQuery(id+"F0.wireOp",EDGE,"E3.0.6.82"),sQuery(id+"F0.wireOp",EDGE,"E3.0.6.83"),sQuery(id+"F0.wireOp",EDGE,"E3.0.6.87"),sQuery(id+"F0.wireOp",EDGE,"E3.0.6.88"),sQuery(id+"F0.wireOp",EDGE,"E3.0.6.93"),sQuery(id+"F0.wireOp",EDGE,"E3.0.6.94"),sQuery(id+"F0.wireOp",EDGE,"E3.0.6.99"),sQuery(id+"F0.wireOp",EDGE,"E3.0.6.104"),sQuery(id+"F0.wireOp",EDGE,"E3.0.6.105"),sQuery(id+"F0.wireOp",EDGE,"E3.0.6.106"),sQuery(id+"F0.wireOp",EDGE,"E3.0.6.109"),sQuery(id+"F0.wireOp",EDGE,"E3.0.6.110"),sQuery(id+"F0.wireOp",EDGE,"E3.0.6.115"),sQuery(id+"F0.wireOp",EDGE,"E3.0.6.116"),sQuery(id+"F0.wireOp",EDGE,"E3.0.6.122"),sQuery(id+"F0.wireOp",EDGE,"E3.0.6.123"),sQuery(id+"F0.wireOp",EDGE,"E3.0.6.127"),sQuery(id+"F0.wireOp",EDGE,"E3.0.6.128"),sQuery(id+"F0.wireOp",EDGE,"E3.0.6.141"),sQuery(id+"F0.wireOp",EDGE,"E3.0.6.142"),sQuery(id+"F0.wireOp",EDGE,"E3.0.6.145"),sQuery(id+"F0.wireOp",EDGE,"E3.0.6.146"),sQuery(id+"F0.wireOp",EDGE,"E3.0.6.147"),sQuery(id+"F0.wireOp",EDGE,"E3.0.6.149"),sQuery(id+"F0.wireOp",EDGE,"E3.0.6.153"),sQuery(id+"F0.wireOp",EDGE,"E3.0.6.154"),sQuery(id+"F0.wireOp",EDGE,"E3.0.6.156"),sQuery(id+"F0.wireOp",EDGE,"E3.0.6.162"),sQuery(id+"F0.wireOp",EDGE,"E3.0.6.163"),sQuery(id+"F0.wireOp",EDGE,"E3.0.6.164"),sQuery(id+"F0.wireOp",EDGE,"E3.0.6.167"),sQuery(id+"F0.wireOp",EDGE,"E3.0.6.170"),sQuery(id+"F0.wireOp",EDGE,"E3.0.6.171"),sQuery(id+"F0.wireOp",EDGE,"E3.0.6.173"),sQuery(id+"F0.wireOp",EDGE,"E3.0.6.178"),sQuery(id+"F0.wireOp",EDGE,"E3.0.6.182"),sQuery(id+"F0.wireOp",EDGE,"E3.0.6.190"),sQuery(id+"F0.wireOp",EDGE,"E3.0.6.194"),sQuery(id+"F0.wireOp",EDGE,"E3.0.6.195"),sQuery(id+"F0.wireOp",EDGE,"E3.0.6.208"),sQuery(id+"F0.wireOp",EDGE,"E3.0.6.211"),sQuery(id+"F0.wireOp",EDGE,"E3.0.6.212"),sQuery(id+"F0.wireOp",EDGE,"E4"),sQuery(id+"F0.wireOp",EDGE,"E5"),sQuery(id+"F0.wireOp",EDGE,"E6"),sQuery(id+"F0.wireOp",EDGE,"E7.MirrorCS"),sQuery(id+"F0.wireOp",EDGE,"E8.MirrorCS"),sQuery(id+"F0.wireOp",EDGE,"E9.MirrorCS"),sQuery(id+"F0.wireOp",EDGE,"E12.MirrorCS"),sQuery(id+"F0.wireOp",EDGE,"E13.MirrorCS"),sQuery(id+"F0.wireOp",EDGE,"E14.MirrorCS"),sQuery(id+"F0.wireOp",EDGE,"E15.MirrorCS"),sQuery(id+"F0.wireOp",EDGE,"E16.MirrorCS"),sQuery(id+"F0.wireOp",EDGE,"E17.MirrorCS"),sQuery(id+"F0.wireOp",EDGE,"E18.MirrorCS"),sQuery(id+"F0.wireOp",EDGE,"E19.MirrorCS"),sQuery(id+"F0.wireOp",EDGE,"E20.MirrorCS"),sQuery(id+"F0.wireOp",EDGE,"E21.MirrorCS"),sQuery(id+"F0.wireOp",EDGE,"E22.MirrorCS"),sQuery(id+"F0.wireOp",EDGE,"E25.MirrorCS"),sQuery(id+"F0.wireOp",EDGE,"E26.MirrorCS"),sQuery(id+"F0.wireOp",EDGE,"E28.MirrorCS"),sQuery(id+"F0.wireOp",EDGE,"E29.MirrorCS"),sQuery(id+"F0.wireOp",EDGE,"E30.MirrorCS"),sQuery(id+"F0.wireOp",EDGE,"E31.MirrorCS"),sQuery(id+"F0.wireOp",EDGE,"E32.MirrorCS"),sQuery(id+"F0.wireOp",EDGE,"E33.MirrorCS"),sQuery(id+"F0.wireOp",EDGE,"E34.MirrorCS"),sQuery(id+"F0.wireOp",EDGE,"E36.MirrorCS"),sQuery(id+"F0.wireOp",EDGE,"E37.MirrorCS"),sQuery(id+"F0.wireOp",EDGE,"E38.MirrorCS"),sQuery(id+"F0.wireOp",EDGE,"E39.MirrorCS"),sQuery(id+"F0.wireOp",EDGE,"E40.MirrorCS"),sQuery(id+"F0.wireOp",EDGE,"E41.MirrorCS"),sQuery(id+"F0.wireOp",EDGE,"E42.MirrorCS"),sQuery(id+"F0.wireOp",EDGE,"E43.MirrorCS"),sQuery(id+"F0.wireOp",EDGE,"E46.MirrorCS"),sQuery(id+"F0.wireOp",EDGE,"E47.MirrorCS"),sQuery(id+"F0.wireOp",EDGE,"E48.MirrorCS"),sQuery(id+"F0.wireOp",EDGE,"E49.MirrorCS"),sQuery(id+"F0.wireOp",EDGE,"E50.MirrorCS"),sQuery(id+"F0.wireOp",EDGE,"E51.MirrorCS"),sQuery(id+"F0.wireOp",EDGE,"E52.MirrorCS"),sQuery(id+"F0.wireOp",EDGE,"E53.MirrorCS"),sQuery(id+"F0.wireOp",EDGE,"E54.MirrorCS"),sQuery(id+"F0.wireOp",EDGE,"E56.MirrorCS"),sQuery(id+"F0.wireOp",EDGE,"E57.MirrorCS"),sQuery(id+"F0.wireOp",EDGE,"E58.MirrorCS"),sQuery(id+"F0.wireOp",EDGE,"E59.MirrorCS"),sQuery(id+"F0.wireOp",EDGE,"E60.MirrorCS"),sQuery(id+"F0.wireOp",EDGE,"E61.MirrorCS"),sQuery(id+"F0.wireOp",EDGE,"E62.MirrorCS"),sQuery(id+"F0.wireOp",EDGE,"E63.MirrorCS"),sQuery(id+"F0.wireOp",EDGE,"E64.MirrorCS"),sQuery(id+"F0.wireOp",EDGE,"E65.MirrorCS"),sQuery(id+"F0.wireOp",EDGE,"E66.MirrorCS"),sQuery(id+"F0.wireOp",EDGE,"E67.MirrorCS"),sQuery(id+"F0.wireOp",EDGE,"E70.MirrorCS"),sQuery(id+"F0.wireOp",EDGE,"E71.MirrorCS"),sQuery(id+"F0.wireOp",EDGE,"E72.MirrorCS"),sQuery(id+"F0.wireOp",EDGE,"E73.MirrorCS"),sQuery(id+"F0.wireOp",EDGE,"E74.MirrorCS"),sQuery(id+"F0.wireOp",EDGE,"E75.MirrorCS"),sQuery(id+"F0.wireOp",EDGE,"E76.MirrorCS"),sQuery(id+"F0.wireOp",EDGE,"E77.MirrorCS"),sQuery(id+"F0.wireOp",EDGE,"E78.MirrorCS"),sQuery(id+"F0.wireOp",EDGE,"E79.MirrorCS"),sQuery(id+"F0.wireOp",EDGE,"E80.MirrorCS"),sQuery(id+"F0.wireOp",EDGE,"E81.MirrorCS"),sQuery(id+"F0.wireOp",EDGE,"E82.MirrorCS"),sQuery(id+"F0.wireOp",EDGE,"E83.MirrorCS"),sQuery(id+"F0.wireOp",EDGE,"E84.MirrorCS"),sQuery(id+"F0.wireOp",EDGE,"E85.MirrorCS"),sQuery(id+"F0.wireOp",EDGE,"E86.MirrorCS"),sQuery(id+"F0.wireOp",EDGE,"E87.MirrorCS"),sQuery(id+"F0.wireOp",EDGE,"E88.MirrorCS"),sQuery(id+"F0.wireOp",EDGE,"E89.MirrorCS"),sQuery(id+"F0.wireOp",EDGE,"E90.MirrorCS"),sQuery(id+"F0.wireOp",EDGE,"E91.MirrorCS"),sQuery(id+"F0.wireOp",EDGE,"E92.MirrorCS"),sQuery(id+"F0.wireOp",EDGE,"E93.MirrorCS"),sQuery(id+"F0.wireOp",EDGE,"E94.MirrorCS"),sQuery(id+"F0.wireOp",EDGE,"E95.MirrorCS"),sQuery(id+"F0.wireOp",EDGE,"E96.MirrorCS"),sQuery(id+"F0.wireOp",EDGE,"E97.MirrorCS"),sQuery(id+"F0.wireOp",EDGE,"E101.MirrorCS"),sQuery(id+"F0.wireOp",EDGE,"E102.MirrorCS"),sQuery(id+"F0.wireOp",EDGE,"E103.MirrorCS"),sQuery(id+"F0.wireOp",EDGE,"E104.MirrorCS"),sQuery(id+"F0.wireOp",EDGE,"E105.MirrorCS"),sQuery(id+"F0.wireOp",EDGE,"E106.MirrorCS"),sQuery(id+"F0.wireOp",EDGE,"E107.MirrorCS"),sQuery(id+"F0.wireOp",EDGE,"E108.MirrorCS"),sQuery(id+"F0.wireOp",EDGE,"E3.0.6.175"),sQuery(id+"F0.wireOp",EDGE,"E109.MirrorCS"),sQuery(id+"F0.wireOp",EDGE,"E110.MirrorCS"),sQuery(id+"F0.wireOp",EDGE,"E111.MirrorCS"),sQuery(id+"F0.wireOp",EDGE,"E112.MirrorCS"),sQuery(id+"F0.wireOp",EDGE,"E113.MirrorCS"),sQuery(id+"F0.wireOp",EDGE,"E114.MirrorCS"),sQuery(id+"F0.wireOp",EDGE,"E115.MirrorCS"),sQuery(id+"F0.wireOp",EDGE,"E116.MirrorCS"),sQuery(id+"F0.wireOp",EDGE,"E117.MirrorCS"),sQuery(id+"F0.wireOp",EDGE,"E118.MirrorCS"),sQuery(id+"F0.wireOp",EDGE,"E3.0.6.192"),sQuery(id+"F0.wireOp",EDGE,"E119.MirrorCS"),sQuery(id+"F0.wireOp",EDGE,"E120.MirrorCS"),sQuery(id+"F0.wireOp",EDGE,"E3.0.6.124"),sQuery(id+"F0.wireOp",EDGE,"E121.MirrorCS"),sQuery(id+"F0.wireOp",EDGE,"E122.MirrorCS"),sQuery(id+"F0.wireOp",EDGE,"E123.MirrorCS"),sQuery(id+"F0.wireOp",EDGE,"E124.MirrorCS"),sQuery(id+"F0.wireOp",EDGE,"E125.MirrorCS"),sQuery(id+"F0.wireOp",EDGE,"E126.MirrorCS"),sQuery(id+"F0.wireOp",EDGE,"E3.0.6.139"),sQuery(id+"F0.wireOp",EDGE,"E127.MirrorCS"),sQuery(id+"F0.wireOp",EDGE,"E128.MirrorCS"),sQuery(id+"F0.wireOp",EDGE,"E129.MirrorCS"),sQuery(id+"F0.wireOp",EDGE,"E130.MirrorCS"),sQuery(id+"F0.wireOp",EDGE,"E131.MirrorCS"),sQuery(id+"F0.wireOp",EDGE,"E132.MirrorCS"),sQuery(id+"F0.wireOp",EDGE,"E133.MirrorCS"),sQuery(id+"F0.wireOp",EDGE,"E134.MirrorCS"),sQuery(id+"F0.wireOp",EDGE,"E135.MirrorCS"),sQuery(id+"F0.wireOp",EDGE,"E136.MirrorCS"),sQuery(id+"F0.wireOp",EDGE,"E137.MirrorCS"),sQuery(id+"F0.wireOp",EDGE,"E138.MirrorCS"),sQuery(id+"F0.wireOp",EDGE,"E139.MirrorCS"),sQuery(id+"F0.wireOp",EDGE,"E140.MirrorCS"),sQuery(id+"F0.wireOp",EDGE,"E141.MirrorCS"),sQuery(id+"F0.wireOp",EDGE,"E142.MirrorCS"),sQuery(id+"F0.wireOp",EDGE,"E143.MirrorCS"),sQuery(id+"F0.wireOp",EDGE,"E144.MirrorCS"),sQuery(id+"F0.wireOp",EDGE,"E145.MirrorCS"),sQuery(id+"F0.wireOp",EDGE,"E146.MirrorCS"),sQuery(id+"F0.wireOp",EDGE,"E147.MirrorCS"),sQuery(id+"F0.wireOp",EDGE,"E148.MirrorCS"),sQuery(id+"F0.wireOp",EDGE,"E149.MirrorCS"),sQuery(id+"F0.wireOp",EDGE,"E150.MirrorCS"),sQuery(id+"F0.wireOp",EDGE,"E151.MirrorCS"),sQuery(id+"F0.wireOp",EDGE,"E152.MirrorCS"),sQuery(id+"F0.wireOp",EDGE,"E155.MirrorCS"),sQuery(id+"F0.wireOp",EDGE,"E158.MirrorCS"),sQuery(id+"F0.wireOp",EDGE,"E159.MirrorCS"),sQuery(id+"F0.wireOp",EDGE,"E160.MirrorCS"),sQuery(id+"F0.wireOp",EDGE,"E164.MirrorCS"),sQuery(id+"F0.wireOp",EDGE,"E166.MirrorCS"),sQuery(id+"F0.wireOp",EDGE,"E167.MirrorCS"),sQuery(id+"F0.wireOp",EDGE,"E169.MirrorCS"),sQuery(id+"F0.wireOp",EDGE,"E170.MirrorCS"),sQuery(id+"F0.wireOp",EDGE,"E171.MirrorCS"),sQuery(id+"F0.wireOp",EDGE,"E172.MirrorCS"),sQuery(id+"F0.wireOp",EDGE,"E173.MirrorCS"),sQuery(id+"F0.wireOp",EDGE,"E174.MirrorCS"),sQuery(id+"F0.wireOp",EDGE,"E175.MirrorCS"),sQuery(id+"F0.wireOp",EDGE,"E176.MirrorCS"),sQuery(id+"F0.wireOp",EDGE,"E177.MirrorCS"),sQuery(id+"F0.wireOp",EDGE,"E178.MirrorCS"),sQuery(id+"F0.wireOp",EDGE,"E180.MirrorCS"),sQuery(id+"F0.wireOp",EDGE,"E183.MirrorCS"),sQuery(id+"F0.wireOp",EDGE,"E184.MirrorCS"),sQuery(id+"F0.wireOp",EDGE,"E185.MirrorCS"),sQuery(id+"F0.wireOp",EDGE,"E188.MirrorCS"),sQuery(id+"F0.wireOp",EDGE,"E189.MirrorCS"),sQuery(id+"F0.wireOp",EDGE,"E190.MirrorCS"),sQuery(id+"F0.wireOp",EDGE,"E191.MirrorCS"),sQuery(id+"F0.wireOp",EDGE,"E192.MirrorCS"),sQuery(id+"F0.wireOp",EDGE,"E194.MirrorCS"),sQuery(id+"F0.wireOp",EDGE,"E198.MirrorCS"),sQuery(id+"F0.wireOp",EDGE,"E199.MirrorCS"),sQuery(id+"F0.wireOp",EDGE,"E201.MirrorCS"),sQuery(id+"F0.wireOp",EDGE,"E206.MirrorCS"),sQuery(id+"F0.wireOp",EDGE,"E207.MirrorCS"),sQuery(id+"F0.wireOp",EDGE,"E208.MirrorCS"),sQuery(id+"F0.wireOp",EDGE,"E209.MirrorCS"),sQuery(id+"F0.wireOp",EDGE,"E210.MirrorCS"),sQuery(id+"F0.wireOp",EDGE,"E211.MirrorCS"),sQuery(id+"F0.wireOp",EDGE,"E212.MirrorCS"),sQuery(id+"F0.wireOp",EDGE,"E213.MirrorCS"),sQuery(id+"F0.wireOp",EDGE,"E215.MirrorCS"),sQuery(id+"F0.wireOp",EDGE,"E222.MirrorCS"),sQuery(id+"F0.wireOp",EDGE,"E3.0.6.151"),sQuery(id+"F0.wireOp",EDGE,"E224.MirrorCS"),sQuery(id+"F0.wireOp",EDGE,"E232.MirrorCS"),sQuery(id+"F0.wireOp",EDGE,"E237.MirrorCS"),sQuery(id+"F0.wireOp",EDGE,"E238.MirrorCS"),sQuery(id+"F0.wireOp",EDGE,"E239.MirrorCS"),sQuery(id+"F0.wireOp",EDGE,"E240.MirrorCS"),sQuery(id+"F0.wireOp",EDGE,"E241.MirrorCS"),sQuery(id+"F0.wireOp",EDGE,"E242.MirrorCS"),sQuery(id+"F0.wireOp",EDGE,"E243.MirrorCS"),sQuery(id+"F0.wireOp",EDGE,"E244.MirrorCS"),sQuery(id+"F0.wireOp",EDGE,"E3.0.6.152"),sQuery(id+"F0.wireOp",EDGE,"E249.MirrorCS"),sQuery(id+"F0.wireOp",EDGE,"E250.MirrorCS"),sQuery(id+"F0.wireOp",EDGE,"E251.MirrorCS"),sQuery(id+"F0.wireOp",EDGE,"E252.MirrorCS"),sQuery(id+"F0.wireOp",EDGE,"E255.MirrorCS"),sQuery(id+"F0.wireOp",EDGE,"E256.MirrorCS"),sQuery(id+"F0.wireOp",EDGE,"E258.MirrorCS"),sQuery(id+"F0.wireOp",EDGE,"E259.MirrorCS"),sQuery(id+"F0.wireOp",EDGE,"E260.MirrorCS"),sQuery(id+"F0.wireOp",EDGE,"E261.MirrorCS"),sQuery(id+"F0.wireOp",EDGE,"E263.MirrorCS"),sQuery(id+"F0.wireOp",EDGE,"E264.MirrorCS"),sQuery(id+"F0.wireOp",EDGE,"E265.MirrorCS"),sQuery(id+"F0.wireOp",EDGE,"E266.MirrorCS"),sQuery(id+"F0.wireOp",EDGE,"E271.MirrorCS"),sQuery(id+"F0.wireOp",EDGE,"E272.MirrorCS"),sQuery(id+"F0.wireOp",EDGE,"E273.MirrorCS"),sQuery(id+"F0.wireOp",EDGE,"E274.MirrorCS"),sQuery(id+"F0.wireOp",EDGE,"E275.MirrorCS"),sQuery(id+"F0.wireOp",EDGE,"E277.MirrorCS"),sQuery(id+"F0.wireOp",EDGE,"E278.MirrorCS"),sQuery(id+"F0.wireOp",EDGE,"E279.MirrorCS"),sQuery(id+"F0.wireOp",EDGE,"E280.MirrorCS"),sQuery(id+"F0.wireOp",EDGE,"E282.MirrorCS"),sQuery(id+"F0.wireOp",EDGE,"E283.MirrorCS"),sQuery(id+"F0.wireOp",EDGE,"E285.MirrorCS"),sQuery(id+"F0.wireOp",EDGE,"E286.MirrorCS"),sQuery(id+"F0.wireOp",EDGE,"E287.MirrorCS"),sQuery(id+"F0.wireOp",EDGE,"E288.MirrorCS"),sQuery(id+"F0.wireOp",EDGE,"E289.MirrorCS"),sQuery(id+"F0.wireOp",EDGE,"E290.MirrorCS"),sQuery(id+"F0.wireOp",EDGE,"E291.MirrorCS"),sQuery(id+"F0.wireOp",EDGE,"E292.MirrorCS"),sQuery(id+"F0.wireOp",EDGE,"E293.MirrorCS"),sQuery(id+"F0.wireOp",EDGE,"E295.MirrorCS"),sQuery(id+"F0.wireOp",EDGE,"E296.MirrorCS"),sQuery(id+"F0.wireOp",EDGE,"E297.MirrorCS"),sQuery(id+"F0.wireOp",EDGE,"E299.MirrorCS"),sQuery(id+"F0.wireOp",EDGE,"E300.MirrorCS"),sQuery(id+"F0.wireOp",EDGE,"E301.MirrorCS"),sQuery(id+"F0.wireOp",EDGE,"E302.MirrorCS"),sQuery(id+"F0.wireOp",EDGE,"E306.MirrorCS"),sQuery(id+"F0.wireOp",EDGE,"E308.MirrorCS"),sQuery(id+"F0.wireOp",EDGE,"E309.MirrorCS"),sQuery(id+"F0.wireOp",EDGE,"E310.MirrorCS"),sQuery(id+"F0.wireOp",EDGE,"E311.MirrorCS"),sQuery(id+"F0.wireOp",EDGE,"E313.MirrorCS"),sQuery(id+"F0.wireOp",EDGE,"E314.MirrorCS"),sQuery(id+"F0.wireOp",EDGE,"E315.MirrorCS"),sQuery(id+"F0.wireOp",EDGE,"E317.MirrorCS"),sQuery(id+"F0.wireOp",EDGE,"E318.MirrorCS"),sQuery(id+"F0.wireOp",EDGE,"E319.MirrorCS"),sQuery(id+"F0.wireOp",EDGE,"E320.MirrorCS"),sQuery(id+"F0.wireOp",EDGE,"E321.MirrorCS"),sQuery(id+"F0.wireOp",EDGE,"E322.MirrorCS"),sQuery(id+"F0.wireOp",EDGE,"E323.MirrorCS"),sQuery(id+"F0.wireOp",EDGE,"E324.MirrorCS"),sQuery(id+"F0.wireOp",EDGE,"E325.MirrorCS"),sQuery(id+"F0.wireOp",EDGE,"E326.MirrorCS"),sQuery(id+"F0.wireOp",EDGE,"E327.MirrorCS"),sQuery(id+"F0.wireOp",EDGE,"E329.MirrorCS"),sQuery(id+"F0.wireOp",EDGE,"E331.MirrorCS"),sQuery(id+"F0.wireOp",EDGE,"E332.MirrorCS"),sQuery(id+"F0.wireOp",EDGE,"E333.MirrorCS"),sQuery(id+"F0.wireOp",EDGE,"E334.MirrorCS"),sQuery(id+"F0.wireOp",EDGE,"E335.MirrorCS"),sQuery(id+"F0.wireOp",EDGE,"E336.MirrorCS"),sQuery(id+"F0.wireOp",EDGE,"E337.MirrorCS"),sQuery(id+"F0.wireOp",EDGE,"E338.MirrorCS"),sQuery(id+"F0.wireOp",EDGE,"E340.MirrorCS"),sQuery(id+"F0.wireOp",EDGE,"E341.MirrorCS"),sQuery(id+"F0.wireOp",EDGE,"E342.MirrorCS"),sQuery(id+"F0.wireOp",EDGE,"E343.MirrorCS"),sQuery(id+"F0.wireOp",EDGE,"E344.MirrorCS"),sQuery(id+"F0.wireOp",EDGE,"E345.MirrorCS"),sQuery(id+"F0.wireOp",EDGE,"E346.MirrorCS"),sQuery(id+"F0.wireOp",EDGE,"E347.MirrorCS"),sQuery(id+"F0.wireOp",EDGE,"E348.MirrorCS"),sQuery(id+"F0.wireOp",EDGE,"E349.MirrorCS"),sQuery(id+"F0.wireOp",EDGE,"E351.MirrorCS"),sQuery(id+"F0.wireOp",EDGE,"E352.MirrorCS"),sQuery(id+"F0.wireOp",EDGE,"E353.MirrorCS"),sQuery(id+"F0.wireOp",EDGE,"E354.MirrorCS"),sQuery(id+"F0.wireOp",EDGE,"E355.MirrorCS"),sQuery(id+"F0.wireOp",EDGE,"E356.MirrorCS"),sQuery(id+"F0.wireOp",EDGE,"E358.MirrorCS"),sQuery(id+"F0.wireOp",EDGE,"E359.MirrorCS"),sQuery(id+"F0.wireOp",EDGE,"E360.MirrorCS"),sQuery(id+"F0.wireOp",EDGE,"E364.MirrorCS"),sQuery(id+"F0.wireOp",EDGE,"E365.MirrorCS"),sQuery(id+"F0.wireOp",EDGE,"E366.MirrorCS"),sQuery(id+"F0.wireOp",EDGE,"E367.MirrorCS"),sQuery(id+"F0.wireOp",EDGE,"E368.MirrorCS"),sQuery(id+"F0.wireOp",EDGE,"E369.MirrorCS"),sQuery(id+"F0.wireOp",EDGE,"E370.MirrorCS"),sQuery(id+"F0.wireOp",EDGE,"E371.MirrorCS"),sQuery(id+"F0.wireOp",EDGE,"E372.MirrorCS"),sQuery(id+"F0.wireOp",EDGE,"E373.MirrorCS"),sQuery(id+"F0.wireOp",EDGE,"E374.MirrorCS"),sQuery(id+"F0.wireOp",EDGE,"E375.MirrorCS"),sQuery(id+"F0.wireOp",EDGE,"E376.MirrorCS"),sQuery(id+"F0.wireOp",EDGE,"E377.MirrorCS"),sQuery(id+"F0.wireOp",EDGE,"E378.MirrorCS"),sQuery(id+"F0.wireOp",EDGE,"E379.MirrorCS"),sQuery(id+"F0.wireOp",EDGE,"E380.MirrorCS"),sQuery(id+"F0.wireOp",EDGE,"E382.MirrorCS"),sQuery(id+"F0.wireOp",EDGE,"E383.MirrorCS"),sQuery(id+"F0.wireOp",EDGE,"E384.MirrorCS"),sQuery(id+"F0.wireOp",EDGE,"E385.MirrorCS"),sQuery(id+"F0.wireOp",EDGE,"E387.MirrorCS"),sQuery(id+"F0.wireOp",EDGE,"E388.MirrorCS"),sQuery(id+"F0.wireOp",EDGE,"E389.MirrorCS"),sQuery(id+"F0.wireOp",EDGE,"E390.MirrorCS"),sQuery(id+"F0.wireOp",EDGE,"E391.MirrorCS"),sQuery(id+"F0.wireOp",EDGE,"E392.MirrorCS"),sQuery(id+"F0.wireOp",EDGE,"E393.MirrorCS"),sQuery(id+"F0.wireOp",EDGE,"E395.MirrorCS"),sQuery(id+"F0.wireOp",EDGE,"E396.MirrorCS"),sQuery(id+"F0.wireOp",EDGE,"E397.MirrorCS"),sQuery(id+"F0.wireOp",EDGE,"E398.MirrorCS"),sQuery(id+"F0.wireOp",EDGE,"E399.MirrorCS"),sQuery(id+"F0.wireOp",EDGE,"E400.MirrorCS"),sQuery(id+"F0.wireOp",EDGE,"E401.MirrorCS"),sQuery(id+"F0.wireOp",EDGE,"E402.MirrorCS"),sQuery(id+"F0.wireOp",EDGE,"E403.MirrorCS"),sQuery(id+"F0.wireOp",EDGE,"E404.MirrorCS"),sQuery(id+"F0.wireOp",EDGE,"E405.MirrorCS"),sQuery(id+"F0.wireOp",EDGE,"E406.MirrorCS"),sQuery(id+"F0.wireOp",EDGE,"E409.MirrorCS"),sQuery(id+"F0.wireOp",EDGE,"E410.MirrorCS"),sQuery(id+"F0.wireOp",EDGE,"E411.MirrorCS"),sQuery(id+"F0.wireOp",EDGE,"E413.MirrorCS"),sQuery(id+"F0.wireOp",EDGE,"E414.MirrorCS"),sQuery(id+"F0.wireOp",EDGE,"E415.MirrorCS"),sQuery(id+"F0.wireOp",EDGE,"E416.MirrorCS"),sQuery(id+"F0.wireOp",EDGE,"E417.MirrorCS"),sQuery(id+"F0.wireOp",EDGE,"E418.MirrorCS"),sQuery(id+"F0.wireOp",EDGE,"E419.MirrorCS"),sQuery(id+"F0.wireOp",EDGE,"E420.MirrorCS"),sQuery(id+"F0.wireOp",EDGE,"E421.MirrorCS"),sQuery(id+"F0.wireOp",EDGE,"E422.MirrorCS"),sQuery(id+"F0.wireOp",EDGE,"E423.MirrorCS"),sQuery(id+"F0.wireOp",EDGE,"E425.MirrorCS"),sQuery(id+"F0.wireOp",EDGE,"E426.MirrorCS"),sQuery(id+"F0.wireOp",EDGE,"E430.MirrorCS"),sQuery(id+"F0.wireOp",EDGE,"E432.MirrorCS"),sQuery(id+"F0.wireOp",EDGE,"E433.MirrorCS"),sQuery(id+"F0.wireOp",EDGE,"E434.MirrorCS"),sQuery(id+"F0.wireOp",EDGE,"E435.MirrorCS"),sQuery(id+"F0.wireOp",EDGE,"E436.MirrorCS"),sQuery(id+"F0.wireOp",EDGE,"E439.MirrorCS"),sQuery(id+"F0.wireOp",EDGE,"E440.MirrorCS"),sQuery(id+"F0.wireOp",EDGE,"E441.MirrorCS"),sQuery(id+"F0.wireOp",EDGE,"E442.MirrorCS"),sQuery(id+"F0.wireOp",EDGE,"E443.MirrorCS"),sQuery(id+"F0.wireOp",EDGE,"E444.MirrorCS"),sQuery(id+"F0.wireOp",EDGE,"E447.MirrorCS"),sQuery(id+"F0.wireOp",EDGE,"E451.MirrorCS"),sQuery(id+"F0.wireOp",EDGE,"E452.MirrorCS"),sQuery(id+"F0.wireOp",EDGE,"E453.MirrorCS"),sQuery(id+"F0.wireOp",EDGE,"E454.MirrorCS"),sQuery(id+"F0.wireOp",EDGE,"E455.MirrorCS"),sQuery(id+"F0.wireOp",EDGE,"E456.MirrorCS"),sQuery(id+"F0.wireOp",EDGE,"E457.MirrorCS"),sQuery(id+"F0.wireOp",EDGE,"E458.MirrorCS"),sQuery(id+"F0.wireOp",EDGE,"E459.MirrorCS"),sQuery(id+"F0.wireOp",EDGE,"E460.MirrorCS"),sQuery(id+"F0.wireOp",EDGE,"E461.MirrorCS"),sQuery(id+"F0.wireOp",EDGE,"E462.MirrorCS"),sQuery(id+"F0.wireOp",EDGE,"E463.MirrorCS"),sQuery(id+"F0.wireOp",EDGE,"E464.MirrorCS"),sQuery(id+"F0.wireOp",EDGE,"E467.MirrorCS"),sQuery(id+"F0.wireOp",EDGE,"E469.MirrorCS"),sQuery(id+"F0.wireOp",EDGE,"E470.MirrorCS"),sQuery(id+"F0.wireOp",EDGE,"E471.MirrorCS"),sQuery(id+"F0.wireOp",EDGE,"E472.MirrorCS"),sQuery(id+"F0.wireOp",EDGE,"E474.MirrorCS"),sQuery(id+"F0.wireOp",EDGE,"E476.MirrorCS"),sQuery(id+"F0.wireOp",EDGE,"E477.MirrorCS"),sQuery(id+"F0.wireOp",EDGE,"E478.MirrorCS"),sQuery(id+"F0.wireOp",EDGE,"E479.MirrorCS"),sQuery(id+"F0.wireOp",EDGE,"E480.MirrorCS"),sQuery(id+"F0.wireOp",EDGE,"E481.MirrorCS"),sQuery(id+"F0.wireOp",EDGE,"E482.MirrorCS"),sQuery(id+"F0.wireOp",EDGE,"E483.MirrorCS"),sQuery(id+"F0.wireOp",EDGE,"E485.MirrorCS"),sQuery(id+"F0.wireOp",EDGE,"E487.MirrorCS"),sQuery(id+"F0.wireOp",EDGE,"E488.MirrorCS"),sQuery(id+"F0.wireOp",EDGE,"E489.MirrorCS"),sQuery(id+"F0.wireOp",EDGE,"E490.MirrorCS"),sQuery(id+"F0.wireOp",EDGE,"E491.MirrorCS"),sQuery(id+"F0.wireOp",EDGE,"E493.MirrorCS"),sQuery(id+"F0.wireOp",EDGE,"E494.MirrorCS"),sQuery(id+"F0.wireOp",EDGE,"E495.MirrorCS"),sQuery(id+"F0.wireOp",EDGE,"E497.MirrorCS"),sQuery(id+"F0.wireOp",EDGE,"E498.MirrorCS"),sQuery(id+"F0.wireOp",EDGE,"E499.MirrorCS"),sQuery(id+"F0.wireOp",EDGE,"E500.MirrorCS"),sQuery(id+"F0.wireOp",EDGE,"E501.MirrorCS"),sQuery(id+"F0.wireOp",EDGE,"E502.MirrorCS"),sQuery(id+"F0.wireOp",EDGE,"E505.MirrorCS"),sQuery(id+"F0.wireOp",EDGE,"E3.0.6.95"),sQuery(id+"F0.wireOp",EDGE,"E507.MirrorCS"),sQuery(id+"F0.wireOp",EDGE,"E511.MirrorCS"),sQuery(id+"F0.wireOp",EDGE,"E514.MirrorCS"),sQuery(id+"F0.wireOp",EDGE,"E516.MirrorCS"),sQuery(id+"F0.wireOp",EDGE,"E517.MirrorCS"),sQuery(id+"F0.wireOp",EDGE,"E518.MirrorCS"),sQuery(id+"F0.wireOp",EDGE,"E519.MirrorCS"),sQuery(id+"F0.wireOp",EDGE,"E520.MirrorCS"),sQuery(id+"F0.wireOp",EDGE,"77a35cee-5665-440d-8739-2c19d19630c15.MirrorCS"),sQuery(id+"F0.wireOp",EDGE,"77a35cee-5665-440d-8739-2c19d19630c16.MirrorCS"),sQuery(id+"F0.wireOp",EDGE,"E521.MirrorCS"),sQuery(id+"F0.wireOp",EDGE,"E522.MirrorCS"),sQuery(id+"F0.wireOp",EDGE,"E524.MirrorCS"),sQuery(id+"F0.wireOp",EDGE,"E525.MirrorCS"),sQuery(id+"F0.wireOp",EDGE,"E526.MirrorCS"),sQuery(id+"F0.wireOp",EDGE,"E527.MirrorCS"),sQuery(id+"F0.wireOp",EDGE,"77a35cee-5665-440d-8739-2c19d19630c119.MirrorCS"),sQuery(id+"F0.wireOp",EDGE,"E528.MirrorCS"),sQuery(id+"F0.wireOp",EDGE,"E529.MirrorCS"),sQuery(id+"F0.wireOp",EDGE,"77a35cee-5665-440d-8739-2c19d19630c123.MirrorCS"),sQuery(id+"F0.wireOp",EDGE,"E530.MirrorCS"),sQuery(id+"F0.wireOp",EDGE,"E532.MirrorCS"),sQuery(id+"F0.wireOp",EDGE,"E5190.MirrorCS"),sQuery(id+"F0.wireOp",EDGE,"E534.MirrorCS"),sQuery(id+"F0.wireOp",EDGE,"E535.MirrorCS"),sQuery(id+"F0.wireOp",EDGE,"E536.MirrorCS"),sQuery(id+"F0.wireOp",EDGE,"E5196.MirrorCS"),sQuery(id+"F0.wireOp",EDGE,"E537.MirrorCS"),sQuery(id+"F0.wireOp",EDGE,"E5199.MirrorCS"),sQuery(id+"F0.wireOp",EDGE,"E5200.MirrorCS"),sQuery(id+"F0.wireOp",EDGE,"E538.MirrorCS"),sQuery(id+"F0.wireOp",EDGE,"E539.MirrorCS"),sQuery(id+"F0.wireOp",EDGE,"E533.MirrorCS"),sQuery(id+"F0.wireOp",EDGE,"E531.MirrorCS"),sQuery(id+"F0.wireOp",EDGE,"E540.MirrorCS"),sQuery(id+"F0.wireOp",EDGE,"E541.MirrorCS"),sQuery(id+"F0.wireOp",EDGE,"E542.MirrorCS"),sQuery(id+"F0.wireOp",EDGE,"E543.MirrorCS"),sQuery(id+"F0.wireOp",EDGE,"77a35cee-5665-440d-8739-2c19d19630c150.MirrorCS"),sQuery(id+"F0.wireOp",EDGE,"E544.MirrorCS"),sQuery(id+"F0.wireOp",EDGE,"77a35cee-5665-440d-8739-2c19d19630c155.MirrorCS"),sQuery(id+"F0.wireOp",EDGE,"E545.MirrorCS"),sQuery(id+"F0.wireOp",EDGE,"E546.MirrorCS"),sQuery(id+"F0.wireOp",EDGE,"77a35cee-5665-440d-8739-2c19d19630c159.MirrorCS"),sQuery(id+"F0.wireOp",EDGE,"E547.MirrorCS"),sQuery(id+"F0.wireOp",EDGE,"E548.MirrorCS"),sQuery(id+"F0.wireOp",EDGE,"77a35cee-5665-440d-8739-2c19d19630c162.MirrorCS"),sQuery(id+"F0.wireOp",EDGE,"E549.MirrorCS"),sQuery(id+"F0.wireOp",EDGE,"E523.MirrorCS"),sQuery(id+"F0.wireOp",EDGE,"77a35cee-5665-440d-8739-2c19d19630c165.MirrorCS"),sQuery(id+"F0.wireOp",EDGE,"E550.MirrorCS"),sQuery(id+"F0.wireOp",EDGE,"E551.MirrorCS"),sQuery(id+"F0.wireOp",EDGE,"E552.MirrorCS"),sQuery(id+"F0.wireOp",EDGE,"E553.MirrorCS"),sQuery(id+"F0.wireOp",EDGE,"E5212.MirrorCS"),sQuery(id+"F0.wireOp",EDGE,"E554.MirrorCS"),sQuery(id+"F0.wireOp",EDGE,"E555.MirrorCS"),sQuery(id+"F0.wireOp",EDGE,"E556.MirrorCS"),sQuery(id+"F0.wireOp",EDGE,"E557.MirrorCS"),sQuery(id+"F0.wireOp",EDGE,"E558.MirrorCS"),sQuery(id+"F0.wireOp",EDGE,"E5219.MirrorCS"),sQuery(id+"F0.wireOp",EDGE,"E5220.MirrorCS"),sQuery(id+"F0.wireOp",EDGE,"E559.MirrorCS"),sQuery(id+"F0.wireOp",EDGE,"E560.MirrorCS"),sQuery(id+"F0.wireOp",EDGE,"E561.MirrorCS"),sQuery(id+"F0.wireOp",EDGE,"E562.MirrorCS"),sQuery(id+"F0.wireOp",EDGE,"E563.MirrorCS"),sQuery(id+"F0.wireOp",EDGE,"E564.MirrorCS"),sQuery(id+"F0.wireOp",EDGE,"E565.MirrorCS"),sQuery(id+"F0.wireOp",EDGE,"E566.MirrorCS"),sQuery(id+"F0.wireOp",EDGE,"E567.MirrorCS"),sQuery(id+"F0.wireOp",EDGE,"E568.MirrorCS"),sQuery(id+"F0.wireOp",EDGE,"E569.MirrorCS"),sQuery(id+"F0.wireOp",EDGE,"E570.MirrorCS"),sQuery(id+"F0.wireOp",EDGE,"E571.MirrorCS"),sQuery(id+"F0.wireOp",EDGE,"E572.MirrorCS"),sQuery(id+"F0.wireOp",EDGE,"E573.MirrorCS"),sQuery(id+"F0.wireOp",EDGE,"E574.MirrorCS"),sQuery(id+"F0.wireOp",EDGE,"E5237.MirrorCS"),sQuery(id+"F0.wireOp",EDGE,"E575.MirrorCS"),sQuery(id+"F0.wireOp",EDGE,"E576.MirrorCS"),sQuery(id+"F0.wireOp",EDGE,"E577.MirrorCS"),sQuery(id+"F0.wireOp",EDGE,"E578.MirrorCS"),sQuery(id+"F0.wireOp",EDGE,"E579.MirrorCS"),sQuery(id+"F0.wireOp",EDGE,"E580.MirrorCS"),sQuery(id+"F0.wireOp",EDGE,"E581.MirrorCS"),sQuery(id+"F0.wireOp",EDGE,"E582.MirrorCS"),sQuery(id+"F0.wireOp",EDGE,"77a35cee-5665-440d-8739-2c19d19630c1106.MirrorCS"),sQuery(id+"F0.wireOp",EDGE,"E583.MirrorCS"),sQuery(id+"F0.wireOp",EDGE,"E584.MirrorCS"),sQuery(id+"F0.wireOp",EDGE,"E585.MirrorCS"),sQuery(id+"F0.wireOp",EDGE,"E586.MirrorCS"),sQuery(id+"F0.wireOp",EDGE,"E587.MirrorCS"),sQuery(id+"F0.wireOp",EDGE,"E588.MirrorCS"),sQuery(id+"F0.wireOp",EDGE,"E589.MirrorCS"),sQuery(id+"F0.wireOp",EDGE,"E590.MirrorCS"),sQuery(id+"F0.wireOp",EDGE,"E591.MirrorCS"),sQuery(id+"F0.wireOp",EDGE,"E592.MirrorCS"),sQuery(id+"F0.wireOp",EDGE,"E593.MirrorCS"),sQuery(id+"F0.wireOp",EDGE,"E594.MirrorCS"),sQuery(id+"F0.wireOp",EDGE,"E595.MirrorCS"),sQuery(id+"F0.wireOp",EDGE,"E596.MirrorCS"),sQuery(id+"F0.wireOp",EDGE,"E597.MirrorCS"),sQuery(id+"F0.wireOp",EDGE,"E598.MirrorCS"),sQuery(id+"F0.wireOp",EDGE,"E599.MirrorCS"),sQuery(id+"F0.wireOp",EDGE,"77a35cee-5665-440d-8739-2c19d19630c1124.MirrorCS"),sQuery(id+"F0.wireOp",EDGE,"77a35cee-5665-440d-8739-2c19d19630c1125.MirrorCS"),sQuery(id+"F0.wireOp",EDGE,"E600.MirrorCS"),sQuery(id+"F0.wireOp",EDGE,"E601.MirrorCS"),sQuery(id+"F0.wireOp",EDGE,"E602.MirrorCS"),sQuery(id+"F0.wireOp",EDGE,"E603.MirrorCS"),sQuery(id+"F0.wireOp",EDGE,"E604.MirrorCS"),sQuery(id+"F0.wireOp",EDGE,"E605.MirrorCS"),sQuery(id+"F0.wireOp",EDGE,"E606.MirrorCS"),sQuery(id+"F0.wireOp",EDGE,"77a35cee-5665-440d-8739-2c19d19630c1134.MirrorCS"),sQuery(id+"F0.wireOp",EDGE,"E607.MirrorCS"),sQuery(id+"F0.wireOp",EDGE,"E608.MirrorCS"),sQuery(id+"F0.wireOp",EDGE,"77a35cee-5665-440d-8739-2c19d19630c1137.MirrorCS"),sQuery(id+"F0.wireOp",EDGE,"77a35cee-5665-440d-8739-2c19d19630c1138.MirrorCS"),sQuery(id+"F0.wireOp",EDGE,"77a35cee-5665-440d-8739-2c19d19630c1139.MirrorCS"),sQuery(id+"F0.wireOp",EDGE,"E609.MirrorCS"),sQuery(id+"F0.wireOp",EDGE,"77a35cee-5665-440d-8739-2c19d19630c1141.MirrorCS"),sQuery(id+"F0.wireOp",EDGE,"E610.MirrorCS"),sQuery(id+"F0.wireOp",EDGE,"E611.MirrorCS"),sQuery(id+"F0.wireOp",EDGE,"E612.MirrorCS"),sQuery(id+"F0.wireOp",EDGE,"E613.MirrorCS"),sQuery(id+"F0.wireOp",EDGE,"E614.MirrorCS"),sQuery(id+"F0.wireOp",EDGE,"E615.MirrorCS"),sQuery(id+"F0.wireOp",EDGE,"E616.MirrorCS"),sQuery(id+"F0.wireOp",EDGE,"E617.MirrorCS"),sQuery(id+"F0.wireOp",EDGE,"E618.MirrorCS"),sQuery(id+"F0.wireOp",EDGE,"E619.MirrorCS"),sQuery(id+"F0.wireOp",EDGE,"E5252.MirrorCS"),sQuery(id+"F0.wireOp",EDGE,"E620.MirrorCS"),sQuery(id+"F0.wireOp",EDGE,"E5254.MirrorCS"),sQuery(id+"F0.wireOp",EDGE,"E621.MirrorCS"),sQuery(id+"F0.wireOp",EDGE,"E622.MirrorCS"),sQuery(id+"F0.wireOp",EDGE,"E5257.MirrorCS"),sQuery(id+"F0.wireOp",EDGE,"E623.MirrorCS"),sQuery(id+"F0.wireOp",EDGE,"E624.MirrorCS"),sQuery(id+"F0.wireOp",EDGE,"E625.MirrorCS"),sQuery(id+"F0.wireOp",EDGE,"E626.MirrorCS"),sQuery(id+"F0.wireOp",EDGE,"E627.MirrorCS"),sQuery(id+"F0.wireOp",EDGE,"E628.MirrorCS"),sQuery(id+"F0.wireOp",EDGE,"E629.MirrorCS"),sQuery(id+"F0.wireOp",EDGE,"E630.MirrorCS"),sQuery(id+"F0.wireOp",EDGE,"E631.MirrorCS"),sQuery(id+"F0.wireOp",EDGE,"E632.MirrorCS"),sQuery(id+"F0.wireOp",EDGE,"E633.MirrorCS"),sQuery(id+"F0.wireOp",EDGE,"E634.MirrorCS"),sQuery(id+"F0.wireOp",EDGE,"E635.MirrorCS"),sQuery(id+"F0.wireOp",EDGE,"E636.MirrorCS"),sQuery(id+"F0.wireOp",EDGE,"E637.MirrorCS"),sQuery(id+"F0.wireOp",EDGE,"77a35cee-5665-440d-8739-2c19d19630c1173.MirrorCS"),sQuery(id+"F0.wireOp",EDGE,"77a35cee-5665-440d-8739-2c19d19630c1174.MirrorCS"),sQuery(id+"F0.wireOp",EDGE,"E638.MirrorCS"),sQuery(id+"F0.wireOp",EDGE,"E639.MirrorCS"),sQuery(id+"F0.wireOp",EDGE,"E640.MirrorCS"),sQuery(id+"F0.wireOp",EDGE,"E641.MirrorCS"),sQuery(id+"F0.wireOp",EDGE,"77a35cee-5665-440d-8739-2c19d19630c1179.MirrorCS"),sQuery(id+"F0.wireOp",EDGE,"E642.MirrorCS"),sQuery(id+"F0.wireOp",EDGE,"E643.MirrorCS"),sQuery(id+"F0.wireOp",EDGE,"E644.MirrorCS"),sQuery(id+"F0.wireOp",EDGE,"E645.MirrorCS"),sQuery(id+"F0.wireOp",EDGE,"E646.MirrorCS"),sQuery(id+"F0.wireOp",EDGE,"E647.MirrorCS"),sQuery(id+"F0.wireOp",EDGE,"E648.MirrorCS"),sQuery(id+"F0.wireOp",EDGE,"E649.MirrorCS"),sQuery(id+"F0.wireOp",EDGE,"E650.MirrorCS"),sQuery(id+"F0.wireOp",EDGE,"E651.MirrorCS"),sQuery(id+"F0.wireOp",EDGE,"77a35cee-5665-440d-8739-2c19d19630c1190.MirrorCS"),sQuery(id+"F0.wireOp",EDGE,"77a35cee-5665-440d-8739-2c19d19630c1191.MirrorCS"),sQuery(id+"F0.wireOp",EDGE,"E652.MirrorCS"),sQuery(id+"F0.wireOp",EDGE,"77a35cee-5665-440d-8739-2c19d19630c1193.MirrorCS"),sQuery(id+"F0.wireOp",EDGE,"77a35cee-5665-440d-8739-2c19d19630c1194.MirrorCS"),sQuery(id+"F0.wireOp",EDGE,"E653.MirrorCS"),sQuery(id+"F0.wireOp",EDGE,"E654.MirrorCS"),sQuery(id+"F0.wireOp",EDGE,"E655.MirrorCS"),sQuery(id+"F0.wireOp",EDGE,"E656.MirrorCS"),sQuery(id+"F0.wireOp",EDGE,"E657.MirrorCS"),sQuery(id+"F0.wireOp",EDGE,"E658.MirrorCS"),sQuery(id+"F0.wireOp",EDGE,"E659.MirrorCS"),sQuery(id+"F0.wireOp",EDGE,"E660.MirrorCS"),sQuery(id+"F0.wireOp",EDGE,"E661.MirrorCS"),sQuery(id+"F0.wireOp",EDGE,"E5284.MirrorCS"),sQuery(id+"F0.wireOp",EDGE,"E662.MirrorCS"),sQuery(id+"F0.wireOp",EDGE,"E663.MirrorCS"),sQuery(id+"F0.wireOp",EDGE,"E664.MirrorCS"),sQuery(id+"F0.wireOp",EDGE,"E5288.MirrorCS"),sQuery(id+"F0.wireOp",EDGE,"E665.MirrorCS"),sQuery(id+"F0.wireOp",EDGE,"E666.MirrorCS"),sQuery(id+"F0.wireOp",EDGE,"E667.MirrorCS"),sQuery(id+"F0.wireOp",EDGE,"E668.MirrorCS"),sQuery(id+"F0.wireOp",EDGE,"E669.MirrorCS"),sQuery(id+"F0.wireOp",EDGE,"E670.MirrorCS"),sQuery(id+"F0.wireOp",EDGE,"E671.MirrorCS"),sQuery(id+"F0.wireOp",EDGE,"E5296.MirrorCS"),sQuery(id+"F0.wireOp",EDGE,"E672.MirrorCS"),sQuery(id+"F0.wireOp",EDGE,"E673.MirrorCS"),sQuery(id+"F0.wireOp",EDGE,"E674.MirrorCS"),sQuery(id+"F0.wireOp",EDGE,"E675.MirrorCS"),sQuery(id+"F0.wireOp",EDGE,"77a35cee-5665-440d-8739-2c19d19630c1221.MirrorCS"),sQuery(id+"F0.wireOp",EDGE,"E676.MirrorCS"),sQuery(id+"F0.wireOp",EDGE,"77a35cee-5665-440d-8739-2c19d19630c1223.MirrorCS"),sQuery(id+"F0.wireOp",EDGE,"E677.MirrorCS"),sQuery(id+"F0.wireOp",EDGE,"E678.MirrorCS"),sQuery(id+"F0.wireOp",EDGE,"E679.MirrorCS"),sQuery(id+"F0.wireOp",EDGE,"E680.MirrorCS"),sQuery(id+"F0.wireOp",EDGE,"E681.MirrorCS"),sQuery(id+"F0.wireOp",EDGE,"E682.MirrorCS"),sQuery(id+"F0.wireOp",EDGE,"E683.MirrorCS"),sQuery(id+"F0.wireOp",EDGE,"E684.MirrorCS"),sQuery(id+"F0.wireOp",EDGE,"77a35cee-5665-440d-8739-2c19d19630c1232.MirrorCS"),sQuery(id+"F0.wireOp",EDGE,"E685.MirrorCS"),sQuery(id+"F0.wireOp",EDGE,"E686.MirrorCS"),sQuery(id+"F0.wireOp",EDGE,"E687.MirrorCS"),sQuery(id+"F0.wireOp",EDGE,"E688.MirrorCS"),sQuery(id+"F0.wireOp",EDGE,"E689.MirrorCS"),sQuery(id+"F0.wireOp",EDGE,"E690.MirrorCS"),sQuery(id+"F0.wireOp",EDGE,"E691.MirrorCS"),sQuery(id+"F0.wireOp",EDGE,"E692.MirrorCS"),sQuery(id+"F0.wireOp",EDGE,"E693.MirrorCS"),sQuery(id+"F0.wireOp",EDGE,"E694.MirrorCS"),sQuery(id+"F0.wireOp",EDGE,"E695.MirrorCS"),sQuery(id+"F0.wireOp",EDGE,"E696.MirrorCS"),sQuery(id+"F0.wireOp",EDGE,"E697.MirrorCS"),sQuery(id+"F0.wireOp",EDGE,"E698.MirrorCS"),sQuery(id+"F0.wireOp",EDGE,"E699.MirrorCS"),sQuery(id+"F0.wireOp",EDGE,"E700.MirrorCS"),sQuery(id+"F0.wireOp",EDGE,"E701.MirrorCS"),sQuery(id+"F0.wireOp",EDGE,"E702.MirrorCS"),sQuery(id+"F0.wireOp",EDGE,"E703.MirrorCS"),sQuery(id+"F0.wireOp",EDGE,"E704.MirrorCS"),sQuery(id+"F0.wireOp",EDGE,"E705.MirrorCS"),sQuery(id+"F0.wireOp",EDGE,"E706.MirrorCS"),sQuery(id+"F0.wireOp",EDGE,"E707.MirrorCS"),sQuery(id+"F0.wireOp",EDGE,"E708.MirrorCS"),sQuery(id+"F0.wireOp",EDGE,"E5318.MirrorCS"),sQuery(id+"F0.wireOp",EDGE,"E709.MirrorCS"),sQuery(id+"F0.wireOp",EDGE,"E710.MirrorCS"),sQuery(id+"F0.wireOp",EDGE,"E711.MirrorCS"),sQuery(id+"F0.wireOp",EDGE,"E712.MirrorCS"),sQuery(id+"F0.wireOp",EDGE,"E713.MirrorCS"),sQuery(id+"F0.wireOp",EDGE,"E714.MirrorCS"),sQuery(id+"F0.wireOp",EDGE,"E715.MirrorCS"),sQuery(id+"F0.wireOp",EDGE,"E5327.MirrorCS"),sQuery(id+"F0.wireOp",EDGE,"E716.MirrorCS"),sQuery(id+"F0.wireOp",EDGE,"E717.MirrorCS"),sQuery(id+"F0.wireOp",EDGE,"E718.MirrorCS"),sQuery(id+"F0.wireOp",EDGE,"E719.MirrorCS"),sQuery(id+"F0.wireOp",EDGE,"E720.MirrorCS"),sQuery(id+"F0.wireOp",EDGE,"E721.MirrorCS"),sQuery(id+"F0.wireOp",EDGE,"E722.MirrorCS"),sQuery(id+"F0.wireOp",EDGE,"E723.MirrorCS"),sQuery(id+"F0.wireOp",EDGE,"77a35cee-5665-440d-8739-2c19d19630c1276.MirrorCS"),sQuery(id+"F0.wireOp",EDGE,"E724.MirrorCS"),sQuery(id+"F0.wireOp",EDGE,"E725.MirrorCS"),sQuery(id+"F0.wireOp",EDGE,"77a35cee-5665-440d-8739-2c19d19630c1279.MirrorCS"),sQuery(id+"F0.wireOp",EDGE,"E726.MirrorCS"),sQuery(id+"F0.wireOp",EDGE,"E727.MirrorCS"),sQuery(id+"F0.wireOp",EDGE,"E728.MirrorCS"),sQuery(id+"F0.wireOp",EDGE,"E729.MirrorCS"),sQuery(id+"F0.wireOp",EDGE,"E730.MirrorCS"),sQuery(id+"F0.wireOp",EDGE,"E731.MirrorCS"),sQuery(id+"F0.wireOp",EDGE,"E732.MirrorCS"),sQuery(id+"F0.wireOp",EDGE,"E733.MirrorCS"),sQuery(id+"F0.wireOp",EDGE,"E734.MirrorCS"),sQuery(id+"F0.wireOp",EDGE,"E735.MirrorCS"),sQuery(id+"F0.wireOp",EDGE,"E736.MirrorCS"),sQuery(id+"F0.wireOp",EDGE,"E737.MirrorCS"),sQuery(id+"F0.wireOp",EDGE,"E738.MirrorCS"),sQuery(id+"F0.wireOp",EDGE,"77a35cee-5665-440d-8739-2c19d19630c1295.MirrorCS"),sQuery(id+"F0.wireOp",EDGE,"E739.MirrorCS"),sQuery(id+"F0.wireOp",EDGE,"E740.MirrorCS"),sQuery(id+"F0.wireOp",EDGE,"E741.MirrorCS"),sQuery(id+"F0.wireOp",EDGE,"E742.MirrorCS"),sQuery(id+"F0.wireOp",EDGE,"E743.MirrorCS"),sQuery(id+"F0.wireOp",EDGE,"E744.MirrorCS"),sQuery(id+"F0.wireOp",EDGE,"E745.MirrorCS"),sQuery(id+"F0.wireOp",EDGE,"E746.MirrorCS"),sQuery(id+"F0.wireOp",EDGE,"E747.MirrorCS"),sQuery(id+"F0.wireOp",EDGE,"E748.MirrorCS"),sQuery(id+"F0.wireOp",EDGE,"E749.MirrorCS"),sQuery(id+"F0.wireOp",EDGE,"E750.MirrorCS"),sQuery(id+"F0.wireOp",EDGE,"E751.MirrorCS"),sQuery(id+"F0.wireOp",EDGE,"E752.MirrorCS"),sQuery(id+"F0.wireOp",EDGE,"E753.MirrorCS"),sQuery(id+"F0.wireOp",EDGE,"E754.MirrorCS"),sQuery(id+"F0.wireOp",EDGE,"E755.MirrorCS"),sQuery(id+"F0.wireOp",EDGE,"E756.MirrorCS"),sQuery(id+"F0.wireOp",EDGE,"E5344.MirrorCS"),sQuery(id+"F0.wireOp",EDGE,"E757.MirrorCS"),sQuery(id+"F0.wireOp",EDGE,"E758.MirrorCS"),sQuery(id+"F0.wireOp",EDGE,"E759.MirrorCS"),sQuery(id+"F0.wireOp",EDGE,"E760.MirrorCS"),sQuery(id+"F0.wireOp",EDGE,"E761.MirrorCS"),sQuery(id+"F0.wireOp",EDGE,"E762.MirrorCS"),sQuery(id+"F0.wireOp",EDGE,"E763.MirrorCS"),sQuery(id+"F0.wireOp",EDGE,"E764.MirrorCS"),sQuery(id+"F0.wireOp",EDGE,"E765.MirrorCS"),sQuery(id+"F0.wireOp",EDGE,"E5355.MirrorCS"),sQuery(id+"F0.wireOp",EDGE,"E766.MirrorCS"),sQuery(id+"F0.wireOp",EDGE,"E767.MirrorCS"),sQuery(id+"F0.wireOp",EDGE,"E5359.MirrorCS"),sQuery(id+"F0.wireOp",EDGE,"E51930.MirrorCS"),sQuery(id+"F0.wireOp",EDGE,"E768.MirrorCS"),sQuery(id+"F0.wireOp",EDGE,"E769.MirrorCS"),sQuery(id+"F0.wireOp",EDGE,"E770.MirrorCS"),sQuery(id+"F0.wireOp",EDGE,"E771.MirrorCS"),sQuery(id+"F0.wireOp",EDGE,"E772.MirrorCS"),sQuery(id+"F0.wireOp",EDGE,"E773.MirrorCS"),sQuery(id+"F0.wireOp",EDGE,"E774.MirrorCS"),sQuery(id+"F0.wireOp",EDGE,"E775.MirrorCS"),sQuery(id+"F0.wireOp",EDGE,"E776.MirrorCS"),sQuery(id+"F0.wireOp",EDGE,"E777.MirrorCS"),sQuery(id+"F0.wireOp",EDGE,"E778.MirrorCS"),sQuery(id+"F0.wireOp",EDGE,"E779.MirrorCS"),sQuery(id+"F0.wireOp",EDGE,"E780.MirrorCS"),sQuery(id+"F0.wireOp",EDGE,"E5364.MirrorCS"),sQuery(id+"F0.wireOp",EDGE,"E781.MirrorCS"),sQuery(id+"F0.wireOp",EDGE,"E782.MirrorCS"),sQuery(id+"F0.wireOp",EDGE,"E783.MirrorCS"),sQuery(id+"F0.wireOp",EDGE,"E51950.MirrorCS"),sQuery(id+"F0.wireOp",EDGE,"E784.MirrorCS"),sQuery(id+"F0.wireOp",EDGE,"E785.MirrorCS"),sQuery(id+"F0.wireOp",EDGE,"E786.MirrorCS"),sQuery(id+"F0.wireOp",EDGE,"E787.MirrorCS"),sQuery(id+"F0.wireOp",EDGE,"E788.MirrorCS"),sQuery(id+"F0.wireOp",EDGE,"E789.MirrorCS"),sQuery(id+"F0.wireOp",EDGE,"E790.MirrorCS"),sQuery(id+"F0.wireOp",EDGE,"E791.MirrorCS"),sQuery(id+"F0.wireOp",EDGE,"E792.MirrorCS"),sQuery(id+"F0.wireOp",EDGE,"E51960.MirrorCS"),sQuery(id+"F0.wireOp",EDGE,"E793.MirrorCS"),sQuery(id+"F0.wireOp",EDGE,"E794.MirrorCS"),sQuery(id+"F0.wireOp",EDGE,"E795.MirrorCS"),sQuery(id+"F0.wireOp",EDGE,"E796.MirrorCS"),sQuery(id+"F0.wireOp",EDGE,"E797.MirrorCS"),sQuery(id+"F0.wireOp",EDGE,"E798.MirrorCS"),sQuery(id+"F0.wireOp",EDGE,"E799.MirrorCS"),sQuery(id+"F0.wireOp",EDGE,"E51968.MirrorCS"),sQuery(id+"F0.wireOp",EDGE,"E800.MirrorCS"),sQuery(id+"F0.wireOp",EDGE,"E801.MirrorCS"),sQuery(id+"F0.wireOp",EDGE,"E802.MirrorCS"),sQuery(id+"F0.wireOp",EDGE,"E803.MirrorCS"),sQuery(id+"F0.wireOp",EDGE,"E804.MirrorCS"),sQuery(id+"F0.wireOp",EDGE,"E805.MirrorCS"),sQuery(id+"F0.wireOp",EDGE,"E806.MirrorCS"),sQuery(id+"F0.wireOp",EDGE,"E807.MirrorCS"),sQuery(id+"F0.wireOp",EDGE,"E808.MirrorCS"),sQuery(id+"F0.wireOp",EDGE,"E809.MirrorCS"),sQuery(id+"F0.wireOp",EDGE,"E810.MirrorCS"),sQuery(id+"F0.wireOp",EDGE,"E811.MirrorCS"),sQuery(id+"F0.wireOp",EDGE,"E812.MirrorCS"),sQuery(id+"F0.wireOp",EDGE,"E51984.MirrorCS"),sQuery(id+"F0.wireOp",EDGE,"E813.MirrorCS"),sQuery(id+"F0.wireOp",EDGE,"E814.MirrorCS"),sQuery(id+"F0.wireOp",EDGE,"E51987.MirrorCS"),sQuery(id+"F0.wireOp",EDGE,"E815.MirrorCS"),sQuery(id+"F0.wireOp",EDGE,"E816.MirrorCS"),sQuery(id+"F0.wireOp",EDGE,"E817.MirrorCS"),sQuery(id+"F0.wireOp",EDGE,"E51991.MirrorCS"),sQuery(id+"F0.wireOp",EDGE,"E818.MirrorCS"),sQuery(id+"F0.wireOp",EDGE,"E819.MirrorCS"),sQuery(id+"F0.wireOp",EDGE,"E820.MirrorCS"),sQuery(id+"F0.wireOp",EDGE,"E821.MirrorCS"),sQuery(id+"F0.wireOp",EDGE,"E822.MirrorCS"),sQuery(id+"F0.wireOp",EDGE,"E823.MirrorCS"),sQuery(id+"F0.wireOp",EDGE,"E824.MirrorCS"),sQuery(id+"F0.wireOp",EDGE,"E825.MirrorCS"),sQuery(id+"F0.wireOp",EDGE,"E826.MirrorCS"),sQuery(id+"F0.wireOp",EDGE,"E827.MirrorCS"),sQuery(id+"F0.wireOp",EDGE,"E828.MirrorCS"),sQuery(id+"F0.wireOp",EDGE,"E829.MirrorCS"),sQuery(id+"F0.wireOp",EDGE,"E830.MirrorCS"),sQuery(id+"F0.wireOp",EDGE,"E831.MirrorCS"),sQuery(id+"F0.wireOp",EDGE,"E832.MirrorCS"),sQuery(id+"F0.wireOp",EDGE,"E833.MirrorCS"),sQuery(id+"F0.wireOp",EDGE,"E52008.MirrorCS"),sQuery(id+"F0.wireOp",EDGE,"E834.MirrorCS"),sQuery(id+"F0.wireOp",EDGE,"E835.MirrorCS"),sQuery(id+"F0.wireOp",EDGE,"E836.MirrorCS"),sQuery(id+"F0.wireOp",EDGE,"E837.MirrorCS"),sQuery(id+"F0.wireOp",EDGE,"E838.MirrorCS"),sQuery(id+"F0.wireOp",EDGE,"E839.MirrorCS"),sQuery(id+"F0.wireOp",EDGE,"E840.MirrorCS"),sQuery(id+"F0.wireOp",EDGE,"E5386.MirrorCS"),sQuery(id+"F0.wireOp",EDGE,"E841.MirrorCS"),sQuery(id+"F0.wireOp",EDGE,"E842.MirrorCS"),sQuery(id+"F0.wireOp",EDGE,"E843.MirrorCS"),sQuery(id+"F0.wireOp",EDGE,"E5390.MirrorCS"),sQuery(id+"F0.wireOp",EDGE,"E5391.MirrorCS"),sQuery(id+"F0.wireOp",EDGE,"E844.MirrorCS"),sQuery(id+"F0.wireOp",EDGE,"E845.MirrorCS"),sQuery(id+"F0.wireOp",EDGE,"E846.MirrorCS"),sQuery(id+"F0.wireOp",EDGE,"E847.MirrorCS"),sQuery(id+"F0.wireOp",EDGE,"E848.MirrorCS"),sQuery(id+"F0.wireOp",EDGE,"E5397.MirrorCS"),sQuery(id+"F0.wireOp",EDGE,"E849.MirrorCS"),sQuery(id+"F0.wireOp",EDGE,"E850.MirrorCS"),sQuery(id+"F0.wireOp",EDGE,"E851.MirrorCS"),sQuery(id+"F0.wireOp",EDGE,"E852.MirrorCS"),sQuery(id+"F0.wireOp",EDGE,"E853.MirrorCS"),sQuery(id+"F0.wireOp",EDGE,"E854.MirrorCS"),sQuery(id+"F0.wireOp",EDGE,"E855.MirrorCS"),sQuery(id+"F0.wireOp",EDGE,"E856.MirrorCS"),sQuery(id+"F0.wireOp",EDGE,"E857.MirrorCS"),sQuery(id+"F0.wireOp",EDGE,"E858.MirrorCS"),sQuery(id+"F0.wireOp",EDGE,"E52039.MirrorCS"),sQuery(id+"F0.wireOp",EDGE,"E859.MirrorCS"),sQuery(id+"F0.wireOp",EDGE,"E860.MirrorCS"),sQuery(id+"F0.wireOp",EDGE,"E861.MirrorCS"),sQuery(id+"F0.wireOp",EDGE,"E862.MirrorCS"),sQuery(id+"F0.wireOp",EDGE,"E863.MirrorCS"),sQuery(id+"F0.wireOp",EDGE,"E864.MirrorCS"),sQuery(id+"F0.wireOp",EDGE,"E865.MirrorCS"),sQuery(id+"F0.wireOp",EDGE,"E866.MirrorCS"),sQuery(id+"F0.wireOp",EDGE,"E867.MirrorCS"),sQuery(id+"F0.wireOp",EDGE,"E868.MirrorCS"),sQuery(id+"F0.wireOp",EDGE,"E869.MirrorCS"),sQuery(id+"F0.wireOp",EDGE,"E870.MirrorCS"),sQuery(id+"F0.wireOp",EDGE,"E871.MirrorCS"),sQuery(id+"F0.wireOp",EDGE,"E872.MirrorCS"),sQuery(id+"F0.wireOp",EDGE,"E873.MirrorCS"),sQuery(id+"F0.wireOp",EDGE,"E874.MirrorCS"),sQuery(id+"F0.wireOp",EDGE,"E875.MirrorCS"),sQuery(id+"F0.wireOp",EDGE,"E876.MirrorCS"),sQuery(id+"F0.wireOp",EDGE,"E877.MirrorCS"),sQuery(id+"F0.wireOp",EDGE,"E878.MirrorCS"),sQuery(id+"F0.wireOp",EDGE,"E879.MirrorCS"),sQuery(id+"F0.wireOp",EDGE,"E880.MirrorCS"),sQuery(id+"F0.wireOp",EDGE,"E881.MirrorCS"),sQuery(id+"F0.wireOp",EDGE,"E882.MirrorCS"),sQuery(id+"F0.wireOp",EDGE,"E883.MirrorCS"),sQuery(id+"F0.wireOp",EDGE,"E884.MirrorCS"),sQuery(id+"F0.wireOp",EDGE,"E885.MirrorCS"),sQuery(id+"F0.wireOp",EDGE,"E5410.MirrorCS"),sQuery(id+"F0.wireOp",EDGE,"E886.MirrorCS"),sQuery(id+"F0.wireOp",EDGE,"E887.MirrorCS"),sQuery(id+"F0.wireOp",EDGE,"E888.MirrorCS"),sQuery(id+"F0.wireOp",EDGE,"E889.MirrorCS"),sQuery(id+"F0.wireOp",EDGE,"E5418.MirrorCS"),sQuery(id+"F0.wireOp",EDGE,"E890.MirrorCS"),sQuery(id+"F0.wireOp",EDGE,"E891.MirrorCS"),sQuery(id+"F0.wireOp",EDGE,"E892.MirrorCS"),sQuery(id+"F0.wireOp",EDGE,"E893.MirrorCS"),sQuery(id+"F0.wireOp",EDGE,"E894.MirrorCS"),sQuery(id+"F0.wireOp",EDGE,"E5424.MirrorCS"),sQuery(id+"F0.wireOp",EDGE,"E5425.MirrorCS"),sQuery(id+"F0.wireOp",EDGE,"E895.MirrorCS"),sQuery(id+"F0.wireOp",EDGE,"E5427.MirrorCS"),sQuery(id+"F0.wireOp",EDGE,"E5428.MirrorCS"),sQuery(id+"F0.wireOp",EDGE,"E896.MirrorCS"),sQuery(id+"F0.wireOp",EDGE,"E897.MirrorCS"),sQuery(id+"F0.wireOp",EDGE,"E898.MirrorCS"),sQuery(id+"F0.wireOp",EDGE,"E899.MirrorCS"),sQuery(id+"F0.wireOp",EDGE,"E900.MirrorCS"),sQuery(id+"F0.wireOp",EDGE,"E5434.MirrorCS"),sQuery(id+"F0.wireOp",EDGE,"E901.MirrorCS"),sQuery(id+"F0.wireOp",EDGE,"E902.MirrorCS"),sQuery(id+"F0.wireOp",EDGE,"E903.MirrorCS"),sQuery(id+"F0.wireOp",EDGE,"E5438.MirrorCS"),sQuery(id+"F0.wireOp",EDGE,"E904.MirrorCS"),sQuery(id+"F0.wireOp",EDGE,"E905.MirrorCS"),sQuery(id+"F0.wireOp",EDGE,"E906.MirrorCS"),sQuery(id+"F0.wireOp",EDGE,"E907.MirrorCS"),sQuery(id+"F0.wireOp",EDGE,"E908.MirrorCS"),sQuery(id+"F0.wireOp",EDGE,"E909.MirrorCS"),sQuery(id+"F0.wireOp",EDGE,"E910.MirrorCS"),sQuery(id+"F0.wireOp",EDGE,"77a35cee-5665-440d-8739-2c19d19630c1507.MirrorCS"),sQuery(id+"F0.wireOp",EDGE,"77a35cee-5665-440d-8739-2c19d19630c1508.MirrorCS"),sQuery(id+"F0.wireOp",EDGE,"77a35cee-5665-440d-8739-2c19d19630c1509.MirrorCS"),sQuery(id+"F0.wireOp",EDGE,"E5440.MirrorCS"),sQuery(id+"F0.wireOp",EDGE,"E911.MirrorCS"),sQuery(id+"F0.wireOp",EDGE,"E912.MirrorCS"),sQuery(id+"F0.wireOp",EDGE,"E913.MirrorCS"),sQuery(id+"F0.wireOp",EDGE,"E914.MirrorCS"),sQuery(id+"F0.wireOp",EDGE,"E915.MirrorCS"),sQuery(id+"F0.wireOp",EDGE,"E916.MirrorCS"),sQuery(id+"F0.wireOp",EDGE,"E917.MirrorCS"),sQuery(id+"F0.wireOp",EDGE,"E918.MirrorCS"),sQuery(id+"F0.wireOp",EDGE,"E919.MirrorCS"),sQuery(id+"F0.wireOp",EDGE,"E920.MirrorCS"),sQuery(id+"F0.wireOp",EDGE,"E921.MirrorCS"),sQuery(id+"F0.wireOp",EDGE,"E922.MirrorCS"),sQuery(id+"F0.wireOp",EDGE,"E923.MirrorCS"),sQuery(id+"F0.wireOp",EDGE,"E924.MirrorCS"),sQuery(id+"F0.wireOp",EDGE,"E925.MirrorCS"),sQuery(id+"F0.wireOp",EDGE,"E926.MirrorCS"),sQuery(id+"F0.wireOp",EDGE,"E927.MirrorCS"),sQuery(id+"F0.wireOp",EDGE,"E928.MirrorCS"),sQuery(id+"F0.wireOp",EDGE,"E929.MirrorCS"),sQuery(id+"F0.wireOp",EDGE,"E930.MirrorCS"),sQuery(id+"F0.wireOp",EDGE,"77a35cee-5665-440d-8739-2c19d19630c1532.MirrorCS"),sQuery(id+"F0.wireOp",EDGE,"E931.MirrorCS"),sQuery(id+"F0.wireOp",EDGE,"E932.MirrorCS"),sQuery(id+"F0.wireOp",EDGE,"E933.MirrorCS"),sQuery(id+"F0.wireOp",EDGE,"E934.MirrorCS"),sQuery(id+"F0.wireOp",EDGE,"E935.MirrorCS"),sQuery(id+"F0.wireOp",EDGE,"E936.MirrorCS"),sQuery(id+"F0.wireOp",EDGE,"E937.MirrorCS"),sQuery(id+"F0.wireOp",EDGE,"E938.MirrorCS"),sQuery(id+"F0.wireOp",EDGE,"E939.MirrorCS"),sQuery(id+"F0.wireOp",EDGE,"E940.MirrorCS"),sQuery(id+"F0.wireOp",EDGE,"E941.MirrorCS"),sQuery(id+"F0.wireOp",EDGE,"E942.MirrorCS"),sQuery(id+"F0.wireOp",EDGE,"E943.MirrorCS"),sQuery(id+"F0.wireOp",EDGE,"E944.MirrorCS"),sQuery(id+"F0.wireOp",EDGE,"E945.MirrorCS"),sQuery(id+"F0.wireOp",EDGE,"E946.MirrorCS"),sQuery(id+"F0.wireOp",EDGE,"E947.MirrorCS"),sQuery(id+"F0.wireOp",EDGE,"E948.MirrorCS"),sQuery(id+"F0.wireOp",EDGE,"77a35cee-5665-440d-8739-2c19d19630c1552.MirrorCS"),sQuery(id+"F0.wireOp",EDGE,"E949.MirrorCS"),sQuery(id+"F0.wireOp",EDGE,"E950.MirrorCS"),sQuery(id+"F0.wireOp",EDGE,"E951.MirrorCS"),sQuery(id+"F0.wireOp",EDGE,"E952.MirrorCS"),sQuery(id+"F0.wireOp",EDGE,"77a35cee-5665-440d-8739-2c19d19630c1557.MirrorCS"),sQuery(id+"F0.wireOp",EDGE,"77a35cee-5665-440d-8739-2c19d19630c1558.MirrorCS"),sQuery(id+"F0.wireOp",EDGE,"77a35cee-5665-440d-8739-2c19d19630c1559.MirrorCS"),sQuery(id+"F0.wireOp",EDGE,"E953.MirrorCS"),sQuery(id+"F0.wireOp",EDGE,"E954.MirrorCS"),sQuery(id+"F0.wireOp",EDGE,"E955.MirrorCS"),sQuery(id+"F0.wireOp",EDGE,"E956.MirrorCS"),sQuery(id+"F0.wireOp",EDGE,"E957.MirrorCS"),sQuery(id+"F0.wireOp",EDGE,"E958.MirrorCS"),sQuery(id+"F0.wireOp",EDGE,"E959.MirrorCS"),sQuery(id+"F0.wireOp",EDGE,"E960.MirrorCS"),sQuery(id+"F0.wireOp",EDGE,"E5458.MirrorCS"),sQuery(id+"F0.wireOp",EDGE,"E961.MirrorCS"),sQuery(id+"F0.wireOp",EDGE,"E962.MirrorCS"),sQuery(id+"F0.wireOp",EDGE,"77a35cee-5665-440d-8739-2c19d19630c1571.MirrorCS"),sQuery(id+"F0.wireOp",EDGE,"E963.MirrorCS"),sQuery(id+"F0.wireOp",EDGE,"E964.MirrorCS"),sQuery(id+"F0.wireOp",EDGE,"E965.MirrorCS"),sQuery(id+"F0.wireOp",EDGE,"E966.MirrorCS"),sQuery(id+"F0.wireOp",EDGE,"E967.MirrorCS"),sQuery(id+"F0.wireOp",EDGE,"E968.MirrorCS"),sQuery(id+"F0.wireOp",EDGE,"77a35cee-5665-440d-8739-2c19d19630c1578.MirrorCS"),sQuery(id+"F0.wireOp",EDGE,"77a35cee-5665-440d-8739-2c19d19630c1579.MirrorCS"),sQuery(id+"F0.wireOp",EDGE,"E969.MirrorCS"),sQuery(id+"F0.wireOp",EDGE,"E5461.MirrorCS"),sQuery(id+"F0.wireOp",EDGE,"E5462.MirrorCS"),sQuery(id+"F0.wireOp",EDGE,"E970.MirrorCS"),sQuery(id+"F0.wireOp",EDGE,"E971.MirrorCS"),sQuery(id+"F0.wireOp",EDGE,"E972.MirrorCS"),sQuery(id+"F0.wireOp",EDGE,"E973.MirrorCS"),sQuery(id+"F0.wireOp",EDGE,"E974.MirrorCS"),sQuery(id+"F0.wireOp",EDGE,"E5468.MirrorCS"),sQuery(id+"F0.wireOp",EDGE,"E975.MirrorCS"),sQuery(id+"F0.wireOp",EDGE,"E976.MirrorCS"),sQuery(id+"F0.wireOp",EDGE,"E977.MirrorCS"),sQuery(id+"F0.wireOp",EDGE,"E978.MirrorCS"),sQuery(id+"F0.wireOp",EDGE,"E979.MirrorCS"),sQuery(id+"F0.wireOp",EDGE,"E980.MirrorCS"),sQuery(id+"F0.wireOp",EDGE,"E981.MirrorCS"),sQuery(id+"F0.wireOp",EDGE,"E982.MirrorCS"),sQuery(id+"F0.wireOp",EDGE,"E983.MirrorCS"),sQuery(id+"F0.wireOp",EDGE,"E984.MirrorCS"),sQuery(id+"F0.wireOp",EDGE,"E985.MirrorCS"),sQuery(id+"F0.wireOp",EDGE,"E986.MirrorCS"),sQuery(id+"F0.wireOp",EDGE,"E5471.MirrorCS"),sQuery(id+"F0.wireOp",EDGE,"E987.MirrorCS"),sQuery(id+"F0.wireOp",EDGE,"E988.MirrorCS"),sQuery(id+"F0.wireOp",EDGE,"E989.MirrorCS"),sQuery(id+"F0.wireOp",EDGE,"E990.MirrorCS"),sQuery(id+"F0.wireOp",EDGE,"E991.MirrorCS"),sQuery(id+"F0.wireOp",EDGE,"E5477.MirrorCS"),sQuery(id+"F0.wireOp",EDGE,"E992.MirrorCS"),sQuery(id+"F0.wireOp",EDGE,"E5480.MirrorCS"),sQuery(id+"F0.wireOp",EDGE,"E993.MirrorCS"),sQuery(id+"F0.wireOp",EDGE,"E5482.MirrorCS"),sQuery(id+"F0.wireOp",EDGE,"E994.MirrorCS"),sQuery(id+"F0.wireOp",EDGE,"E5484.MirrorCS"),sQuery(id+"F0.wireOp",EDGE,"E995.MirrorCS"),sQuery(id+"F0.wireOp",EDGE,"E5486.MirrorCS"),sQuery(id+"F0.wireOp",EDGE,"E5487.MirrorCS"),sQuery(id+"F0.wireOp",EDGE,"E996.MirrorCS"),sQuery(id+"F0.wireOp",EDGE,"E997.MirrorCS"),sQuery(id+"F0.wireOp",EDGE,"E998.MirrorCS"),sQuery(id+"F0.wireOp",EDGE,"E999.MirrorCS"),sQuery(id+"F0.wireOp",EDGE,"77a35cee-5665-440d-8739-2c19d19630c1622.MirrorCS"),sQuery(id+"F0.wireOp",EDGE,"E1000.MirrorCS"),sQuery(id+"F0.wireOp",EDGE,"77a35cee-5665-440d-8739-2c19d19630c1624.MirrorCS"),sQuery(id+"F0.wireOp",EDGE,"E1001.MirrorCS"),sQuery(id+"F0.wireOp",EDGE,"E1002.MirrorCS"),sQuery(id+"F0.wireOp",EDGE,"E1003.MirrorCS"),sQuery(id+"F0.wireOp",EDGE,"77a35cee-5665-440d-8739-2c19d19630c1628.MirrorCS"),sQuery(id+"F0.wireOp",EDGE,"E1004.MirrorCS"),sQuery(id+"F0.wireOp",EDGE,"E5490.MirrorCS"),sQuery(id+"F0.wireOp",EDGE,"E1005.MirrorCS"),sQuery(id+"F0.wireOp",EDGE,"E5492.MirrorCS"),sQuery(id+"F0.wireOp",EDGE,"E1006.MirrorCS"),sQuery(id+"F0.wireOp",EDGE,"E1007.MirrorCS"),sQuery(id+"F0.wireOp",EDGE,"E1008.MirrorCS"),sQuery(id+"F0.wireOp",EDGE,"E1009.MirrorCS"),sQuery(id+"F0.wireOp",EDGE,"E5497.MirrorCS"),sQuery(id+"F0.wireOp",EDGE,"E1010.MirrorCS"),sQuery(id+"F0.wireOp",EDGE,"E1011.MirrorCS"),sQuery(id+"F0.wireOp",EDGE,"E1012.MirrorCS"),sQuery(id+"F0.wireOp",EDGE,"E1013.MirrorCS"),sQuery(id+"F0.wireOp",EDGE,"E1014.MirrorCS"),sQuery(id+"F0.wireOp",EDGE,"E1015.MirrorCS"),sQuery(id+"F0.wireOp",EDGE,"E1016.MirrorCS"),sQuery(id+"F0.wireOp",EDGE,"E1017.MirrorCS"),sQuery(id+"F0.wireOp",EDGE,"E1018.MirrorCS"),sQuery(id+"F0.wireOp",EDGE,"E1019.MirrorCS"),sQuery(id+"F0.wireOp",EDGE,"E1020.MirrorCS"),sQuery(id+"F0.wireOp",EDGE,"E1021.MirrorCS"),sQuery(id+"F0.wireOp",EDGE,"E1022.MirrorCS"),sQuery(id+"F0.wireOp",EDGE,"E1023.MirrorCS"),sQuery(id+"F0.wireOp",EDGE,"E1024.MirrorCS"),sQuery(id+"F0.wireOp",EDGE,"E1025.MirrorCS"),sQuery(id+"F0.wireOp",EDGE,"E1026.MirrorCS"),sQuery(id+"F0.wireOp",EDGE,"E1027.MirrorCS"),sQuery(id+"F0.wireOp",EDGE,"E1028.MirrorCS"),sQuery(id+"F0.wireOp",EDGE,"E1029.MirrorCS"),sQuery(id+"F0.wireOp",EDGE,"E1030.MirrorCS"),sQuery(id+"F0.wireOp",EDGE,"E1031.MirrorCS"),sQuery(id+"F0.wireOp",EDGE,"E1032.MirrorCS"),sQuery(id+"F0.wireOp",EDGE,"77a35cee-5665-440d-8739-2c19d19630c1661.MirrorCS"),sQuery(id+"F0.wireOp",EDGE,"E1033.MirrorCS"),sQuery(id+"F0.wireOp",EDGE,"E1034.MirrorCS"),sQuery(id+"F0.wireOp",EDGE,"E1035.MirrorCS"),sQuery(id+"F0.wireOp",EDGE,"E1036.MirrorCS"),sQuery(id+"F0.wireOp",EDGE,"E1037.MirrorCS"),sQuery(id+"F0.wireOp",EDGE,"E1038.MirrorCS"),sQuery(id+"F0.wireOp",EDGE,"E1039.MirrorCS"),sQuery(id+"F0.wireOp",EDGE,"E1040.MirrorCS"),sQuery(id+"F0.wireOp",EDGE,"E1041.MirrorCS"),sQuery(id+"F0.wireOp",EDGE,"E1042.MirrorCS"),sQuery(id+"F0.wireOp",EDGE,"E1043.MirrorCS"),sQuery(id+"F0.wireOp",EDGE,"E1044.MirrorCS"),sQuery(id+"F0.wireOp",EDGE,"E1045.MirrorCS"),sQuery(id+"F0.wireOp",EDGE,"E1046.MirrorCS"),sQuery(id+"F0.wireOp",EDGE,"E5509.MirrorCS"),sQuery(id+"F0.wireOp",EDGE,"E1047.MirrorCS"),sQuery(id+"F0.wireOp",EDGE,"E1048.MirrorCS"),sQuery(id+"F0.wireOp",EDGE,"E1049.MirrorCS"),sQuery(id+"F0.wireOp",EDGE,"E1050.MirrorCS"),sQuery(id+"F0.wireOp",EDGE,"E1051.MirrorCS"),sQuery(id+"F0.wireOp",EDGE,"E1052.MirrorCS"),sQuery(id+"F0.wireOp",EDGE,"E5516.MirrorCS"),sQuery(id+"F0.wireOp",EDGE,"E1053.MirrorCS"),sQuery(id+"F0.wireOp",EDGE,"E5520.MirrorCS"),sQuery(id+"F0.wireOp",EDGE,"E1054.MirrorCS"),sQuery(id+"F0.wireOp",EDGE,"E1055.MirrorCS"),sQuery(id+"F0.wireOp",EDGE,"E1056.MirrorCS"),sQuery(id+"F0.wireOp",EDGE,"E1057.MirrorCS"),sQuery(id+"F0.wireOp",EDGE,"E1058.MirrorCS"),sQuery(id+"F0.wireOp",EDGE,"E1059.MirrorCS"),sQuery(id+"F0.wireOp",EDGE,"E1060.MirrorCS"),sQuery(id+"F0.wireOp",EDGE,"E5528.MirrorCS"),sQuery(id+"F0.wireOp",EDGE,"E1061.MirrorCS"),sQuery(id+"F0.wireOp",EDGE,"E1062.MirrorCS"),sQuery(id+"F0.wireOp",EDGE,"E1063.MirrorCS"),sQuery(id+"F0.wireOp",EDGE,"E1064.MirrorCS"),sQuery(id+"F0.wireOp",EDGE,"E1065.MirrorCS"),sQuery(id+"F0.wireOp",EDGE,"E1066.MirrorCS"),sQuery(id+"F0.wireOp",EDGE,"E52105.MirrorCS"),sQuery(id+"F0.wireOp",EDGE,"E1067.MirrorCS"),sQuery(id+"F0.wireOp",EDGE,"E1068.MirrorCS"),sQuery(id+"F0.wireOp",EDGE,"E1069.MirrorCS"),sQuery(id+"F0.wireOp",EDGE,"E1070.MirrorCS"),sQuery(id+"F0.wireOp",EDGE,"E1071.MirrorCS"),sQuery(id+"F0.wireOp",EDGE,"E1072.MirrorCS"),sQuery(id+"F0.wireOp",EDGE,"E1073.MirrorCS"),sQuery(id+"F0.wireOp",EDGE,"E1074.MirrorCS"),sQuery(id+"F0.wireOp",EDGE,"E1075.MirrorCS"),sQuery(id+"F0.wireOp",EDGE,"E1076.MirrorCS"),sQuery(id+"F0.wireOp",EDGE,"E1077.MirrorCS"),sQuery(id+"F0.wireOp",EDGE,"E1078.MirrorCS"),sQuery(id+"F0.wireOp",EDGE,"E1079.MirrorCS"),sQuery(id+"F0.wireOp",EDGE,"E1080.MirrorCS"),sQuery(id+"F0.wireOp",EDGE,"E1081.MirrorCS"),sQuery(id+"F0.wireOp",EDGE,"E1082.MirrorCS"),sQuery(id+"F0.wireOp",EDGE,"E1083.MirrorCS"),sQuery(id+"F0.wireOp",EDGE,"E1084.MirrorCS"),sQuery(id+"F0.wireOp",EDGE,"E1085.MirrorCS"),sQuery(id+"F0.wireOp",EDGE,"E1086.MirrorCS"),sQuery(id+"F0.wireOp",EDGE,"E1087.MirrorCS"),sQuery(id+"F0.wireOp",EDGE,"E1088.MirrorCS"),sQuery(id+"F0.wireOp",EDGE,"E1089.MirrorCS"),sQuery(id+"F0.wireOp",EDGE,"E5541.MirrorCS"),sQuery(id+"F0.wireOp",EDGE,"E1090.MirrorCS"),sQuery(id+"F0.wireOp",EDGE,"E1091.MirrorCS"),sQuery(id+"F0.wireOp",EDGE,"E1092.MirrorCS"),sQuery(id+"F0.wireOp",EDGE,"E1093.MirrorCS"),sQuery(id+"F0.wireOp",EDGE,"E1094.MirrorCS"),sQuery(id+"F0.wireOp",EDGE,"E1095.MirrorCS"),sQuery(id+"F0.wireOp",EDGE,"E1096.MirrorCS"),sQuery(id+"F0.wireOp",EDGE,"E1097.MirrorCS"),sQuery(id+"F0.wireOp",EDGE,"E1098.MirrorCS"),sQuery(id+"F0.wireOp",EDGE,"E1099.MirrorCS"),sQuery(id+"F0.wireOp",EDGE,"E1100.MirrorCS"),sQuery(id+"F0.wireOp",EDGE,"E1101.MirrorCS"),sQuery(id+"F0.wireOp",EDGE,"E1102.MirrorCS"),sQuery(id+"F0.wireOp",EDGE,"E1103.MirrorCS"),sQuery(id+"F0.wireOp",EDGE,"E1104.MirrorCS"),sQuery(id+"F0.wireOp",EDGE,"E1105.MirrorCS"),sQuery(id+"F0.wireOp",EDGE,"E1106.MirrorCS"),sQuery(id+"F0.wireOp",EDGE,"E1107.MirrorCS"),sQuery(id+"F0.wireOp",EDGE,"E1108.MirrorCS"),sQuery(id+"F0.wireOp",EDGE,"E1109.MirrorCS"),sQuery(id+"F0.wireOp",EDGE,"E1110.MirrorCS"),sQuery(id+"F0.wireOp",EDGE,"E1111.MirrorCS"),sQuery(id+"F0.wireOp",EDGE,"E1112.MirrorCS"),sQuery(id+"F0.wireOp",EDGE,"E1113.MirrorCS"),sQuery(id+"F0.wireOp",EDGE,"E1114.MirrorCS"),sQuery(id+"F0.wireOp",EDGE,"E1115.MirrorCS"),sQuery(id+"F0.wireOp",EDGE,"E1116.MirrorCS"),sQuery(id+"F0.wireOp",EDGE,"E1117.MirrorCS"),sQuery(id+"F0.wireOp",EDGE,"E1118.MirrorCS"),sQuery(id+"F0.wireOp",EDGE,"E1119.MirrorCS"),sQuery(id+"F0.wireOp",EDGE,"E1120.MirrorCS"),sQuery(id+"F0.wireOp",EDGE,"E1121.MirrorCS"),sQuery(id+"F0.wireOp",EDGE,"E52168.MirrorCS"),sQuery(id+"F0.wireOp",EDGE,"E1122.MirrorCS"),sQuery(id+"F0.wireOp",EDGE,"E1123.MirrorCS"),sQuery(id+"F0.wireOp",EDGE,"E1124.MirrorCS"),sQuery(id+"F0.wireOp",EDGE,"E5572.MirrorCS"),sQuery(id+"F0.wireOp",EDGE,"E1125.MirrorCS"),sQuery(id+"F0.wireOp",EDGE,"E1126.MirrorCS"),sQuery(id+"F0.wireOp",EDGE,"E1127.MirrorCS"),sQuery(id+"F0.wireOp",EDGE,"E1128.MirrorCS"),sQuery(id+"F0.wireOp",EDGE,"E1129.MirrorCS"),sQuery(id+"F0.wireOp",EDGE,"E1130.MirrorCS"),sQuery(id+"F0.wireOp",EDGE,"E1131.MirrorCS"),sQuery(id+"F0.wireOp",EDGE,"E1132.MirrorCS"),sQuery(id+"F0.wireOp",EDGE,"E1133.MirrorCS"),sQuery(id+"F0.wireOp",EDGE,"E1134.MirrorCS"),sQuery(id+"F0.wireOp",EDGE,"E5583.MirrorCS"),sQuery(id+"F0.wireOp",EDGE,"E5584.MirrorCS"),sQuery(id+"F0.wireOp",EDGE,"E1135.MirrorCS"),sQuery(id+"F0.wireOp",EDGE,"E1136.MirrorCS"),sQuery(id+"F0.wireOp",EDGE,"E1137.MirrorCS"),sQuery(id+"F0.wireOp",EDGE,"E1138.MirrorCS"),sQuery(id+"F0.wireOp",EDGE,"E52190.MirrorCS"),sQuery(id+"F0.wireOp",EDGE,"E1139.MirrorCS"),sQuery(id+"F0.wireOp",EDGE,"E1140.MirrorCS"),sQuery(id+"F0.wireOp",EDGE,"E1141.MirrorCS"),sQuery(id+"F0.wireOp",EDGE,"E1142.MirrorCS"),sQuery(id+"F0.wireOp",EDGE,"E1143.MirrorCS"),sQuery(id+"F0.wireOp",EDGE,"E1144.MirrorCS"),sQuery(id+"F0.wireOp",EDGE,"E1145.MirrorCS"),sQuery(id+"F0.wireOp",EDGE,"E52198.MirrorCS"),sQuery(id+"F0.wireOp",EDGE,"E1146.MirrorCS"),sQuery(id+"F0.wireOp",EDGE,"E1147.MirrorCS"),sQuery(id+"F0.wireOp",EDGE,"E1148.MirrorCS"),sQuery(id+"F0.wireOp",EDGE,"E1149.MirrorCS"),sQuery(id+"F0.wireOp",EDGE,"E1150.MirrorCS"),sQuery(id+"F0.wireOp",EDGE,"E1151.MirrorCS"),sQuery(id+"F0.wireOp",EDGE,"E1152.MirrorCS"),sQuery(id+"F0.wireOp",EDGE,"E1153.MirrorCS"),sQuery(id+"F0.wireOp",EDGE,"E1154.MirrorCS"),sQuery(id+"F0.wireOp",EDGE,"E1155.MirrorCS"),sQuery(id+"F0.wireOp",EDGE,"E52209.MirrorCS"),sQuery(id+"F0.wireOp",EDGE,"E5590.MirrorCS"),sQuery(id+"F0.wireOp",EDGE,"E1156.MirrorCS"),sQuery(id+"F0.wireOp",EDGE,"E1157.MirrorCS"),sQuery(id+"F0.wireOp",EDGE,"E1158.MirrorCS"),sQuery(id+"F0.wireOp",EDGE,"E1159.MirrorCS"),sQuery(id+"F0.wireOp",EDGE,"E1160.MirrorCS"),sQuery(id+"F0.wireOp",EDGE,"E1161.MirrorCS"),sQuery(id+"F0.wireOp",EDGE,"E1162.MirrorCS"),sQuery(id+"F0.wireOp",EDGE,"E5598.MirrorCS"),sQuery(id+"F0.wireOp",EDGE,"E1163.MirrorCS"),sQuery(id+"F0.wireOp",EDGE,"E1164.MirrorCS"),sQuery(id+"F0.wireOp",EDGE,"E1165.MirrorCS"),sQuery(id+"F0.wireOp",EDGE,"E1166.MirrorCS"),sQuery(id+"F0.wireOp",EDGE,"E1167.MirrorCS"),sQuery(id+"F0.wireOp",EDGE,"E1168.MirrorCS"),sQuery(id+"F0.wireOp",EDGE,"E1169.MirrorCS"),sQuery(id+"F0.wireOp",EDGE,"E1170.MirrorCS"),sQuery(id+"F0.wireOp",EDGE,"E1171.MirrorCS"),sQuery(id+"F0.wireOp",EDGE,"E5609.MirrorCS"),sQuery(id+"F0.wireOp",EDGE,"E1172.MirrorCS"),sQuery(id+"F0.wireOp",EDGE,"E1173.MirrorCS"),sQuery(id+"F0.wireOp",EDGE,"E1174.MirrorCS"),sQuery(id+"F0.wireOp",EDGE,"E1175.MirrorCS"),sQuery(id+"F0.wireOp",EDGE,"E1176.MirrorCS"),sQuery(id+"F0.wireOp",EDGE,"E1177.MirrorCS"),sQuery(id+"F0.wireOp",EDGE,"E1178.MirrorCS"),sQuery(id+"F0.wireOp",EDGE,"E1179.MirrorCS"),sQuery(id+"F0.wireOp",EDGE,"E1180.MirrorCS"),sQuery(id+"F0.wireOp",EDGE,"E1181.MirrorCS"),sQuery(id+"F0.wireOp",EDGE,"E1182.MirrorCS"),sQuery(id+"F0.wireOp",EDGE,"E1183.MirrorCS"),sQuery(id+"F0.wireOp",EDGE,"E1184.MirrorCS"),sQuery(id+"F0.wireOp",EDGE,"E1185.MirrorCS"),sQuery(id+"F0.wireOp",EDGE,"E1186.MirrorCS"),sQuery(id+"F0.wireOp",EDGE,"E1187.MirrorCS"),sQuery(id+"F0.wireOp",EDGE,"E1188.MirrorCS"),sQuery(id+"F0.wireOp",EDGE,"E1189.MirrorCS"),sQuery(id+"F0.wireOp",EDGE,"E1190.MirrorCS"),sQuery(id+"F0.wireOp",EDGE,"E1191.MirrorCS"),sQuery(id+"F0.wireOp",EDGE,"E1192.MirrorCS"),sQuery(id+"F0.wireOp",EDGE,"E1193.MirrorCS"),sQuery(id+"F0.wireOp",EDGE,"E1194.MirrorCS"),sQuery(id+"F0.wireOp",EDGE,"E1195.MirrorCS"),sQuery(id+"F0.wireOp",EDGE,"E5635.MirrorCS"),sQuery(id+"F0.wireOp",EDGE,"E1196.MirrorCS"),sQuery(id+"F0.wireOp",EDGE,"E1197.MirrorCS"),sQuery(id+"F0.wireOp",EDGE,"E1198.MirrorCS"),sQuery(id+"F0.wireOp",EDGE,"E1199.MirrorCS"),sQuery(id+"F0.wireOp",EDGE,"E1200.MirrorCS"),sQuery(id+"F0.wireOp",EDGE,"E1201.MirrorCS"),sQuery(id+"F0.wireOp",EDGE,"E1202.MirrorCS"),sQuery(id+"F0.wireOp",EDGE,"E5646.MirrorCS"),sQuery(id+"F0.wireOp",EDGE,"E1203.MirrorCS"),sQuery(id+"F0.wireOp",EDGE,"E5648.MirrorCS"),sQuery(id+"F0.wireOp",EDGE,"E5650.MirrorCS"),sQuery(id+"F0.wireOp",EDGE,"E1205.MirrorCS"),sQuery(id+"F0.wireOp",EDGE,"E1206.MirrorCS"),sQuery(id+"F0.wireOp",EDGE,"E1207.MirrorCS"),sQuery(id+"F0.wireOp",EDGE,"E1208.MirrorCS"),sQuery(id+"F0.wireOp",EDGE,"E5656.MirrorCS"),sQuery(id+"F0.wireOp",EDGE,"E1209.MirrorCS"),sQuery(id+"F0.wireOp",EDGE,"E5658.MirrorCS"),sQuery(id+"F0.wireOp",EDGE,"E1210.MirrorCS"),sQuery(id+"F0.wireOp",EDGE,"E1211.MirrorCS"),sQuery(id+"F0.wireOp",EDGE,"E5661.MirrorCS"),sQuery(id+"F0.wireOp",EDGE,"E1212.MirrorCS"),sQuery(id+"F0.wireOp",EDGE,"E1213.MirrorCS"),sQuery(id+"F0.wireOp",EDGE,"E1214.MirrorCS"),sQuery(id+"F0.wireOp",EDGE,"E1215.MirrorCS"),sQuery(id+"F0.wireOp",EDGE,"E1216.MirrorCS"),sQuery(id+"F0.wireOp",EDGE,"E1217.MirrorCS"),sQuery(id+"F0.wireOp",EDGE,"E1218.MirrorCS"),sQuery(id+"F0.wireOp",EDGE,"E1219.MirrorCS"),sQuery(id+"F0.wireOp",EDGE,"E1220.MirrorCS"),sQuery(id+"F0.wireOp",EDGE,"E1221.MirrorCS"),sQuery(id+"F0.wireOp",EDGE,"E1222.MirrorCS"),sQuery(id+"F0.wireOp",EDGE,"E1223.MirrorCS"),sQuery(id+"F0.wireOp",EDGE,"E1224.MirrorCS"),sQuery(id+"F0.wireOp",EDGE,"E1225.MirrorCS"),sQuery(id+"F0.wireOp",EDGE,"E1226.MirrorCS"),sQuery(id+"F0.wireOp",EDGE,"E1227.MirrorCS"),sQuery(id+"F0.wireOp",EDGE,"E1228.MirrorCS"),sQuery(id+"F0.wireOp",EDGE,"E1229.MirrorCS"),sQuery(id+"F0.wireOp",EDGE,"E1230.MirrorCS"),sQuery(id+"F0.wireOp",EDGE,"E1231.MirrorCS"),sQuery(id+"F0.wireOp",EDGE,"E1232.MirrorCS"),sQuery(id+"F0.wireOp",EDGE,"E1233.MirrorCS"),sQuery(id+"F0.wireOp",EDGE,"E1234.MirrorCS"),sQuery(id+"F0.wireOp",EDGE,"E1235.MirrorCS"),sQuery(id+"F0.wireOp",EDGE,"E1236.MirrorCS"),sQuery(id+"F0.wireOp",EDGE,"E5688.MirrorCS"),sQuery(id+"F0.wireOp",EDGE,"E5689.MirrorCS"),sQuery(id+"F0.wireOp",EDGE,"E1237.MirrorCS"),sQuery(id+"F0.wireOp",EDGE,"E1238.MirrorCS"),sQuery(id+"F0.wireOp",EDGE,"E1239.MirrorCS"),sQuery(id+"F0.wireOp",EDGE,"E1240.MirrorCS"),sQuery(id+"F0.wireOp",EDGE,"E5694.MirrorCS"),sQuery(id+"F0.wireOp",EDGE,"E1241.MirrorCS"),sQuery(id+"F0.wireOp",EDGE,"E1242.MirrorCS"),sQuery(id+"F0.wireOp",EDGE,"E5698.MirrorCS"),sQuery(id+"F0.wireOp",EDGE,"E1243.MirrorCS"),sQuery(id+"F0.wireOp",EDGE,"E1244.MirrorCS"),sQuery(id+"F0.wireOp",EDGE,"E1276.MirrorCS"),sQuery(id+"F0.wireOp",EDGE,"E1279.MirrorCS"),sQuery(id+"F0.wireOp",EDGE,"E1286.MirrorCS"),sQuery(id+"F0.wireOp",EDGE,"E1293.MirrorCS"),sQuery(id+"F0.wireOp",EDGE,"E1383"),sQuery(id+"F0.wireOp",EDGE,"E1384")])],"isStart":false});
            var sketch = newSketch(context, id + "F1", { "sketchPlane" : qUnion([Q0])});
            skSolve(sketch);
        }
        {
            var Q0;
            Q0=makeQuery(id+"F0.imprint","IMPRINT",FACE,{"disambiguationData":[TD([[makeQuery(id+"F0.imprint","IMPRINT",EDGE,{"derivedFrom":sQuery(id+"F0.wireOp",EDGE,"E2.2.0.0")}),-1.0]])]});
            var Q1;
            Q1=makeQuery(id+"F0.imprint","IMPRINT",FACE,{"disambiguationData":[TD([[makeQuery(id+"F0.imprint","IMPRINT",EDGE,{"derivedFrom":sQuery(id+"F0.wireOp",EDGE,"E2.2.0.0")}),-1.0]])]});
            extrude(context, id + "F2", {"entities" : qUnion([Q0, Q1]), "depth" : 25.4 * mm});
        }
    });
